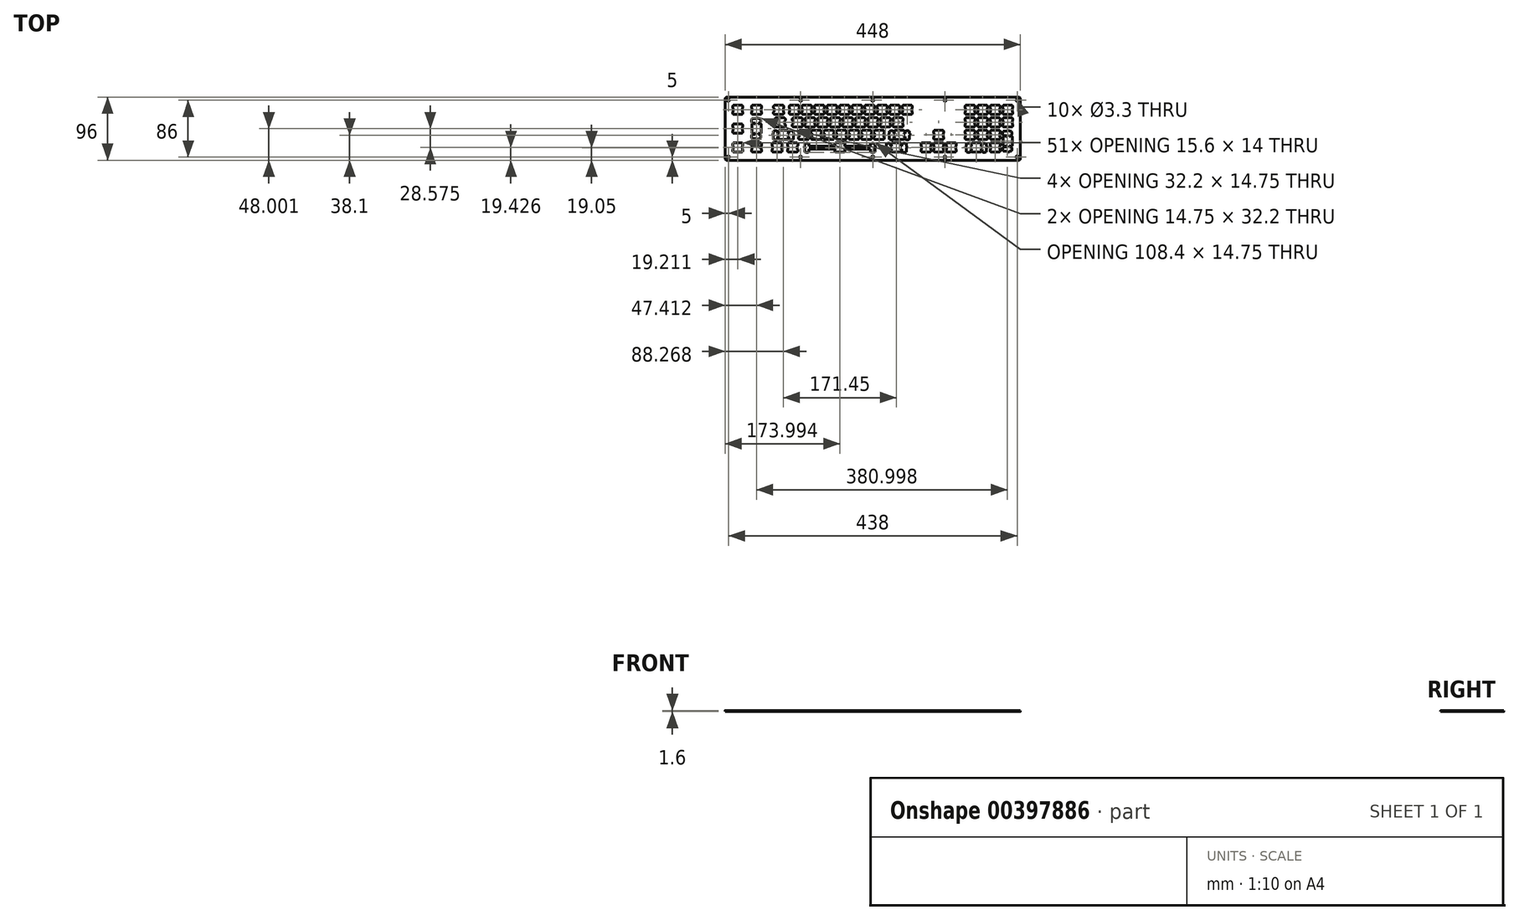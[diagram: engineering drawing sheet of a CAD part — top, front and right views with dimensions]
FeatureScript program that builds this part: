
annotation { "Feature Type Name" : "Feature", "Feature Type Description" : "" }
export const myFeature = defineFeature(function(context is Context, id is Id, definition is map)
    precondition{}
    {
        {
            var Q0;
            Q0=qCreatedBy(makeId("Top.planeOp"),FACE);
            var sketch = newSketch(context, id + "F0", { "sketchPlane" : qUnion([Q0])});
            skLineSegment(sketch, "E0", {"start": v(-224.31, 48.1) * mm, "end": v(224.31, 48.1) * mm});
            skLineSegment(sketch, "E1", {"start": v(224.31, 48.1) * mm, "end": v(224.31, -48.1) * mm});
            skLineSegment(sketch, "E2", {"start": v(224.31, -48.1) * mm, "end": v(-224.31, -48.1) * mm});
            skLineSegment(sketch, "E3", {"start": v(-224.31, -48.1) * mm, "end": v(-224.31, 48.1) * mm});
            skLineSegment(sketch, "E4", {"start": v(-57, -21.57) * mm, "end": v(-57, -22.58) * mm});
            skLineSegment(sketch, "E5", {"start": v(-57, -22.58) * mm, "end": v(-57.8, -22.58) * mm});
            skLineSegment(sketch, "E6", {"start": v(-57.8, -22.58) * mm, "end": v(-57.8, -25.67) * mm});
            skLineSegment(sketch, "E7", {"start": v(-57.8, -25.67) * mm, "end": v(-57, -25.67) * mm});
            skLineSegment(sketch, "E8", {"start": v(-57, -25.67) * mm, "end": v(-57, -26.28) * mm});
            skLineSegment(sketch, "E9", {"start": v(-57, -26.28) * mm, "end": v(-96.68, -26.28) * mm});
            skLineSegment(sketch, "E10", {"start": v(-96.68, -26.28) * mm, "end": v(-96.68, -23.05) * mm});
            skLineSegment(sketch, "E11", {"start": v(-96.68, -23.05) * mm, "end": v(-98.36, -23.05) * mm});
            skLineSegment(sketch, "E12", {"start": v(-98.36, -23.05) * mm, "end": v(-98.36, -22.12) * mm});
            skLineSegment(sketch, "E13", {"start": v(-98.36, -22.12) * mm, "end": v(-101.66, -22.12) * mm});
            skLineSegment(sketch, "E14", {"start": v(-101.66, -22.12) * mm, "end": v(-101.66, -23.05) * mm});
            skLineSegment(sketch, "E15", {"start": v(-101.66, -23.05) * mm, "end": v(-103.33, -23.05) * mm});
            skLineSegment(sketch, "E16", {"start": v(-103.33, -23.05) * mm, "end": v(-103.33, -26.28) * mm});
            skLineSegment(sketch, "E17", {"start": v(-103.33, -26.28) * mm, "end": v(-104.2, -26.28) * mm});
            skLineSegment(sketch, "E18", {"start": v(-104.2, -26.28) * mm, "end": v(-104.2, -29.08) * mm});
            skLineSegment(sketch, "E19", {"start": v(-104.2, -29.08) * mm, "end": v(-103.33, -29.08) * mm});
            skLineSegment(sketch, "E20", {"start": v(-103.33, -29.08) * mm, "end": v(-103.33, -35.35) * mm});
            skLineSegment(sketch, "E21", {"start": v(-103.33, -35.35) * mm, "end": v(-101.66, -35.35) * mm});
            skLineSegment(sketch, "E22", {"start": v(-101.66, -35.35) * mm, "end": v(-101.66, -36.33) * mm});
            skLineSegment(sketch, "E23", {"start": v(-101.66, -36.33) * mm, "end": v(-98.36, -36.33) * mm});
            skLineSegment(sketch, "E24", {"start": v(-98.36, -36.33) * mm, "end": v(-98.36, -35.35) * mm});
            skLineSegment(sketch, "E25", {"start": v(-98.36, -35.35) * mm, "end": v(-96.68, -35.35) * mm});
            skLineSegment(sketch, "E26", {"start": v(-96.68, -35.35) * mm, "end": v(-96.68, -30.88) * mm});
            skLineSegment(sketch, "E27", {"start": v(-96.68, -30.88) * mm, "end": v(-57, -30.88) * mm});
            skLineSegment(sketch, "E28", {"start": v(-57, -30.88) * mm, "end": v(-57, -31.47) * mm});
            skLineSegment(sketch, "E29", {"start": v(-57, -31.47) * mm, "end": v(-57.8, -31.47) * mm});
            skLineSegment(sketch, "E30", {"start": v(-57.8, -31.47) * mm, "end": v(-57.8, -34.58) * mm});
            skLineSegment(sketch, "E31", {"start": v(-57.8, -34.58) * mm, "end": v(-57, -34.58) * mm});
            skLineSegment(sketch, "E32", {"start": v(-57, -34.58) * mm, "end": v(-57, -35.57) * mm});
            skLineSegment(sketch, "E33", {"start": v(-57, -35.57) * mm, "end": v(-43, -35.57) * mm});
            skLineSegment(sketch, "E34", {"start": v(-43, -35.57) * mm, "end": v(-43, -34.58) * mm});
            skLineSegment(sketch, "E35", {"start": v(-43, -34.58) * mm, "end": v(-42.2, -34.58) * mm});
            skLineSegment(sketch, "E36", {"start": v(-42.2, -34.58) * mm, "end": v(-42.2, -31.47) * mm});
            skLineSegment(sketch, "E37", {"start": v(-42.2, -31.47) * mm, "end": v(-43, -31.47) * mm});
            skLineSegment(sketch, "E38", {"start": v(-43, -31.47) * mm, "end": v(-43, -30.88) * mm});
            skLineSegment(sketch, "E39", {"start": v(-43, -30.88) * mm, "end": v(-3.33, -30.88) * mm});
            skLineSegment(sketch, "E40", {"start": v(-3.33, -30.88) * mm, "end": v(-3.33, -35.35) * mm});
            skLineSegment(sketch, "E41", {"start": v(-3.33, -35.35) * mm, "end": v(-1.66, -35.35) * mm});
            skLineSegment(sketch, "E42", {"start": v(-1.66, -35.35) * mm, "end": v(-1.66, -36.33) * mm});
            skLineSegment(sketch, "E43", {"start": v(-1.66, -36.33) * mm, "end": v(1.64, -36.33) * mm});
            skLineSegment(sketch, "E44", {"start": v(1.64, -36.33) * mm, "end": v(1.64, -35.35) * mm});
            skLineSegment(sketch, "E45", {"start": v(1.64, -35.35) * mm, "end": v(3.32, -35.35) * mm});
            skLineSegment(sketch, "E46", {"start": v(3.32, -35.35) * mm, "end": v(3.32, -29.08) * mm});
            skLineSegment(sketch, "E47", {"start": v(3.32, -29.08) * mm, "end": v(4.2, -29.08) * mm});
            skLineSegment(sketch, "E48", {"start": v(4.2, -29.08) * mm, "end": v(4.2, -26.28) * mm});
            skLineSegment(sketch, "E49", {"start": v(4.2, -26.28) * mm, "end": v(3.32, -26.28) * mm});
            skLineSegment(sketch, "E50", {"start": v(3.32, -26.28) * mm, "end": v(3.32, -23.05) * mm});
            skLineSegment(sketch, "E51", {"start": v(3.32, -23.05) * mm, "end": v(1.64, -23.05) * mm});
            skLineSegment(sketch, "E52", {"start": v(1.64, -23.05) * mm, "end": v(1.64, -22.12) * mm});
            skLineSegment(sketch, "E53", {"start": v(1.64, -22.12) * mm, "end": v(-1.66, -22.12) * mm});
            skLineSegment(sketch, "E54", {"start": v(-1.66, -22.12) * mm, "end": v(-1.66, -23.05) * mm});
            skLineSegment(sketch, "E55", {"start": v(-1.66, -23.05) * mm, "end": v(-3.33, -23.05) * mm});
            skLineSegment(sketch, "E56", {"start": v(-3.33, -23.05) * mm, "end": v(-3.33, -26.28) * mm});
            skLineSegment(sketch, "E57", {"start": v(-3.33, -26.28) * mm, "end": v(-43, -26.28) * mm});
            skLineSegment(sketch, "E58", {"start": v(-43, -26.28) * mm, "end": v(-43, -25.67) * mm});
            skLineSegment(sketch, "E59", {"start": v(-43, -25.67) * mm, "end": v(-42.2, -25.67) * mm});
            skLineSegment(sketch, "E60", {"start": v(-42.2, -25.67) * mm, "end": v(-42.2, -22.58) * mm});
            skLineSegment(sketch, "E61", {"start": v(-42.2, -22.58) * mm, "end": v(-43, -22.58) * mm});
            skLineSegment(sketch, "E62", {"start": v(-43, -22.58) * mm, "end": v(-43, -21.57) * mm});
            skLineSegment(sketch, "E63", {"start": v(-43, -21.57) * mm, "end": v(-57, -21.57) * mm});
            skLineSegment(sketch, "E64", {"start": v(28.72, -21.57) * mm, "end": v(28.72, -22.58) * mm});
            skLineSegment(sketch, "E65", {"start": v(28.72, -22.58) * mm, "end": v(27.92, -22.58) * mm});
            skLineSegment(sketch, "E66", {"start": v(27.92, -22.58) * mm, "end": v(27.92, -25.67) * mm});
            skLineSegment(sketch, "E67", {"start": v(27.92, -25.67) * mm, "end": v(28.72, -25.67) * mm});
            skLineSegment(sketch, "E68", {"start": v(28.72, -25.67) * mm, "end": v(28.72, -26.28) * mm});
            skLineSegment(sketch, "E69", {"start": v(28.72, -26.28) * mm, "end": v(27.14, -26.28) * mm});
            skLineSegment(sketch, "E70", {"start": v(27.14, -26.28) * mm, "end": v(27.14, -23.05) * mm});
            skLineSegment(sketch, "E71", {"start": v(27.14, -23.05) * mm, "end": v(25.47, -23.05) * mm});
            skLineSegment(sketch, "E72", {"start": v(25.47, -23.05) * mm, "end": v(25.47, -22.12) * mm});
            skLineSegment(sketch, "E73", {"start": v(25.47, -22.12) * mm, "end": v(22.17, -22.12) * mm});
            skLineSegment(sketch, "E74", {"start": v(22.17, -22.12) * mm, "end": v(22.17, -23.05) * mm});
            skLineSegment(sketch, "E75", {"start": v(22.17, -23.05) * mm, "end": v(20.5, -23.05) * mm});
            skLineSegment(sketch, "E76", {"start": v(20.5, -23.05) * mm, "end": v(20.5, -26.28) * mm});
            skLineSegment(sketch, "E77", {"start": v(20.5, -26.28) * mm, "end": v(19.62, -26.28) * mm});
            skLineSegment(sketch, "E78", {"start": v(19.62, -26.28) * mm, "end": v(19.62, -29.08) * mm});
            skLineSegment(sketch, "E79", {"start": v(19.62, -29.08) * mm, "end": v(20.5, -29.08) * mm});
            skLineSegment(sketch, "E80", {"start": v(20.5, -29.08) * mm, "end": v(20.5, -35.35) * mm});
            skLineSegment(sketch, "E81", {"start": v(20.5, -35.35) * mm, "end": v(22.17, -35.35) * mm});
            skLineSegment(sketch, "E82", {"start": v(22.17, -35.35) * mm, "end": v(22.17, -36.33) * mm});
            skLineSegment(sketch, "E83", {"start": v(22.17, -36.33) * mm, "end": v(25.47, -36.33) * mm});
            skLineSegment(sketch, "E84", {"start": v(25.47, -36.33) * mm, "end": v(25.47, -35.35) * mm});
            skLineSegment(sketch, "E85", {"start": v(25.47, -35.35) * mm, "end": v(27.14, -35.35) * mm});
            skLineSegment(sketch, "E86", {"start": v(27.14, -35.35) * mm, "end": v(27.14, -30.88) * mm});
            skLineSegment(sketch, "E87", {"start": v(27.14, -30.88) * mm, "end": v(28.72, -30.88) * mm});
            skLineSegment(sketch, "E88", {"start": v(28.72, -30.88) * mm, "end": v(28.72, -31.47) * mm});
            skLineSegment(sketch, "E89", {"start": v(28.72, -31.47) * mm, "end": v(27.92, -31.47) * mm});
            skLineSegment(sketch, "E90", {"start": v(27.92, -31.47) * mm, "end": v(27.92, -34.58) * mm});
            skLineSegment(sketch, "E91", {"start": v(27.92, -34.58) * mm, "end": v(28.72, -34.58) * mm});
            skLineSegment(sketch, "E92", {"start": v(28.72, -34.58) * mm, "end": v(28.72, -35.57) * mm});
            skLineSegment(sketch, "E93", {"start": v(28.72, -35.57) * mm, "end": v(42.72, -35.57) * mm});
            skLineSegment(sketch, "E94", {"start": v(42.72, -35.57) * mm, "end": v(42.72, -34.58) * mm});
            skLineSegment(sketch, "E95", {"start": v(42.72, -34.58) * mm, "end": v(43.52, -34.58) * mm});
            skLineSegment(sketch, "E96", {"start": v(43.52, -34.58) * mm, "end": v(43.52, -31.47) * mm});
            skLineSegment(sketch, "E97", {"start": v(43.52, -31.47) * mm, "end": v(42.72, -31.47) * mm});
            skLineSegment(sketch, "E98", {"start": v(42.72, -31.47) * mm, "end": v(42.72, -30.88) * mm});
            skLineSegment(sketch, "E99", {"start": v(42.72, -30.88) * mm, "end": v(44.3, -30.88) * mm});
            skLineSegment(sketch, "E100", {"start": v(44.3, -30.88) * mm, "end": v(44.3, -35.35) * mm});
            skLineSegment(sketch, "E101", {"start": v(44.3, -35.35) * mm, "end": v(45.97, -35.35) * mm});
            skLineSegment(sketch, "E102", {"start": v(45.97, -35.35) * mm, "end": v(45.97, -36.33) * mm});
            skLineSegment(sketch, "E103", {"start": v(45.97, -36.33) * mm, "end": v(49.27, -36.33) * mm});
            skLineSegment(sketch, "E104", {"start": v(49.27, -36.33) * mm, "end": v(49.27, -35.35) * mm});
            skLineSegment(sketch, "E105", {"start": v(49.27, -35.35) * mm, "end": v(50.94, -35.35) * mm});
            skLineSegment(sketch, "E106", {"start": v(50.94, -35.35) * mm, "end": v(50.94, -29.08) * mm});
            skLineSegment(sketch, "E107", {"start": v(50.94, -29.08) * mm, "end": v(51.82, -29.08) * mm});
            skLineSegment(sketch, "E108", {"start": v(51.82, -29.08) * mm, "end": v(51.82, -26.28) * mm});
            skLineSegment(sketch, "E109", {"start": v(51.82, -26.28) * mm, "end": v(50.94, -26.28) * mm});
            skLineSegment(sketch, "E110", {"start": v(50.94, -26.28) * mm, "end": v(50.94, -23.05) * mm});
            skLineSegment(sketch, "E111", {"start": v(50.94, -23.05) * mm, "end": v(49.27, -23.05) * mm});
            skLineSegment(sketch, "E112", {"start": v(49.27, -23.05) * mm, "end": v(49.27, -22.12) * mm});
            skLineSegment(sketch, "E113", {"start": v(49.27, -22.12) * mm, "end": v(45.97, -22.12) * mm});
            skLineSegment(sketch, "E114", {"start": v(45.97, -22.12) * mm, "end": v(45.97, -23.05) * mm});
            skLineSegment(sketch, "E115", {"start": v(45.97, -23.05) * mm, "end": v(44.3, -23.05) * mm});
            skLineSegment(sketch, "E116", {"start": v(44.3, -23.05) * mm, "end": v(44.3, -26.28) * mm});
            skLineSegment(sketch, "E117", {"start": v(44.3, -26.28) * mm, "end": v(42.72, -26.28) * mm});
            skLineSegment(sketch, "E118", {"start": v(42.72, -26.28) * mm, "end": v(42.72, -25.67) * mm});
            skLineSegment(sketch, "E119", {"start": v(42.72, -25.67) * mm, "end": v(43.52, -25.67) * mm});
            skLineSegment(sketch, "E120", {"start": v(43.52, -25.67) * mm, "end": v(43.52, -22.58) * mm});
            skLineSegment(sketch, "E121", {"start": v(43.52, -22.58) * mm, "end": v(42.72, -22.58) * mm});
            skLineSegment(sketch, "E122", {"start": v(42.72, -22.58) * mm, "end": v(42.72, -21.57) * mm});
            skLineSegment(sketch, "E123", {"start": v(42.72, -21.57) * mm, "end": v(28.72, -21.57) * mm});
            skLineSegment(sketch, "E124", {"start": v(150.16, -21.57) * mm, "end": v(150.16, -22.58) * mm});
            skLineSegment(sketch, "E125", {"start": v(150.16, -22.58) * mm, "end": v(149.36, -22.58) * mm});
            skLineSegment(sketch, "E126", {"start": v(149.36, -22.58) * mm, "end": v(149.36, -25.67) * mm});
            skLineSegment(sketch, "E127", {"start": v(149.36, -25.67) * mm, "end": v(150.16, -25.67) * mm});
            skLineSegment(sketch, "E128", {"start": v(150.16, -25.67) * mm, "end": v(150.16, -26.28) * mm});
            skLineSegment(sketch, "E129", {"start": v(150.16, -26.28) * mm, "end": v(148.59, -26.28) * mm});
            skLineSegment(sketch, "E130", {"start": v(148.59, -26.28) * mm, "end": v(148.59, -23.05) * mm});
            skLineSegment(sketch, "E131", {"start": v(148.59, -23.05) * mm, "end": v(146.91, -23.05) * mm});
            skLineSegment(sketch, "E132", {"start": v(146.91, -23.05) * mm, "end": v(146.91, -22.12) * mm});
            skLineSegment(sketch, "E133", {"start": v(146.91, -22.12) * mm, "end": v(143.61, -22.12) * mm});
            skLineSegment(sketch, "E134", {"start": v(143.61, -22.12) * mm, "end": v(143.61, -23.05) * mm});
            skLineSegment(sketch, "E135", {"start": v(143.61, -23.05) * mm, "end": v(141.94, -23.05) * mm});
            skLineSegment(sketch, "E136", {"start": v(141.94, -23.05) * mm, "end": v(141.94, -26.28) * mm});
            skLineSegment(sketch, "E137", {"start": v(141.94, -26.28) * mm, "end": v(141.06, -26.28) * mm});
            skLineSegment(sketch, "E138", {"start": v(141.06, -26.28) * mm, "end": v(141.06, -29.08) * mm});
            skLineSegment(sketch, "E139", {"start": v(141.06, -29.08) * mm, "end": v(141.94, -29.08) * mm});
            skLineSegment(sketch, "E140", {"start": v(141.94, -29.08) * mm, "end": v(141.94, -35.35) * mm});
            skLineSegment(sketch, "E141", {"start": v(141.94, -35.35) * mm, "end": v(143.61, -35.35) * mm});
            skLineSegment(sketch, "E142", {"start": v(143.61, -35.35) * mm, "end": v(143.61, -36.33) * mm});
            skLineSegment(sketch, "E143", {"start": v(143.61, -36.33) * mm, "end": v(146.91, -36.33) * mm});
            skLineSegment(sketch, "E144", {"start": v(146.91, -36.33) * mm, "end": v(146.91, -35.35) * mm});
            skLineSegment(sketch, "E145", {"start": v(146.91, -35.35) * mm, "end": v(148.59, -35.35) * mm});
            skLineSegment(sketch, "E146", {"start": v(148.59, -35.35) * mm, "end": v(148.59, -30.88) * mm});
            skLineSegment(sketch, "E147", {"start": v(148.59, -30.88) * mm, "end": v(150.16, -30.88) * mm});
            skLineSegment(sketch, "E148", {"start": v(150.16, -30.88) * mm, "end": v(150.16, -31.47) * mm});
            skLineSegment(sketch, "E149", {"start": v(150.16, -31.47) * mm, "end": v(149.36, -31.47) * mm});
            skLineSegment(sketch, "E150", {"start": v(149.36, -31.47) * mm, "end": v(149.36, -34.58) * mm});
            skLineSegment(sketch, "E151", {"start": v(149.36, -34.58) * mm, "end": v(150.16, -34.58) * mm});
            skLineSegment(sketch, "E152", {"start": v(150.16, -34.58) * mm, "end": v(150.16, -35.57) * mm});
            skLineSegment(sketch, "E153", {"start": v(150.16, -35.57) * mm, "end": v(164.16, -35.57) * mm});
            skLineSegment(sketch, "E154", {"start": v(164.16, -35.57) * mm, "end": v(164.16, -34.58) * mm});
            skLineSegment(sketch, "E155", {"start": v(164.16, -34.58) * mm, "end": v(164.96, -34.58) * mm});
            skLineSegment(sketch, "E156", {"start": v(164.96, -34.58) * mm, "end": v(164.96, -31.47) * mm});
            skLineSegment(sketch, "E157", {"start": v(164.96, -31.47) * mm, "end": v(164.16, -31.47) * mm});
            skLineSegment(sketch, "E158", {"start": v(164.16, -31.47) * mm, "end": v(164.16, -30.88) * mm});
            skLineSegment(sketch, "E159", {"start": v(164.16, -30.88) * mm, "end": v(165.74, -30.88) * mm});
            skLineSegment(sketch, "E160", {"start": v(165.74, -30.88) * mm, "end": v(165.74, -35.35) * mm});
            skLineSegment(sketch, "E161", {"start": v(165.74, -35.35) * mm, "end": v(167.41, -35.35) * mm});
            skLineSegment(sketch, "E162", {"start": v(167.41, -35.35) * mm, "end": v(167.41, -36.33) * mm});
            skLineSegment(sketch, "E163", {"start": v(167.41, -36.33) * mm, "end": v(170.71, -36.33) * mm});
            skLineSegment(sketch, "E164", {"start": v(170.71, -36.33) * mm, "end": v(170.71, -35.35) * mm});
            skLineSegment(sketch, "E165", {"start": v(170.71, -35.35) * mm, "end": v(172.39, -35.35) * mm});
            skLineSegment(sketch, "E166", {"start": v(172.39, -35.35) * mm, "end": v(172.39, -29.08) * mm});
            skLineSegment(sketch, "E167", {"start": v(172.39, -29.08) * mm, "end": v(173.26, -29.08) * mm});
            skLineSegment(sketch, "E168", {"start": v(173.26, -29.08) * mm, "end": v(173.26, -26.28) * mm});
            skLineSegment(sketch, "E169", {"start": v(173.26, -26.28) * mm, "end": v(172.39, -26.28) * mm});
            skLineSegment(sketch, "E170", {"start": v(172.39, -26.28) * mm, "end": v(172.39, -23.05) * mm});
            skLineSegment(sketch, "E171", {"start": v(172.39, -23.05) * mm, "end": v(170.71, -23.05) * mm});
            skLineSegment(sketch, "E172", {"start": v(170.71, -23.05) * mm, "end": v(170.71, -22.12) * mm});
            skLineSegment(sketch, "E173", {"start": v(170.71, -22.12) * mm, "end": v(167.41, -22.12) * mm});
            skLineSegment(sketch, "E174", {"start": v(167.41, -22.12) * mm, "end": v(167.41, -23.05) * mm});
            skLineSegment(sketch, "E175", {"start": v(167.41, -23.05) * mm, "end": v(165.74, -23.05) * mm});
            skLineSegment(sketch, "E176", {"start": v(165.74, -23.05) * mm, "end": v(165.74, -26.28) * mm});
            skLineSegment(sketch, "E177", {"start": v(165.74, -26.28) * mm, "end": v(164.16, -26.28) * mm});
            skLineSegment(sketch, "E178", {"start": v(164.16, -26.28) * mm, "end": v(164.16, -25.67) * mm});
            skLineSegment(sketch, "E179", {"start": v(164.16, -25.67) * mm, "end": v(164.96, -25.67) * mm});
            skLineSegment(sketch, "E180", {"start": v(164.96, -25.67) * mm, "end": v(164.96, -22.58) * mm});
            skLineSegment(sketch, "E181", {"start": v(164.96, -22.58) * mm, "end": v(164.16, -22.58) * mm});
            skLineSegment(sketch, "E182", {"start": v(164.16, -22.58) * mm, "end": v(164.16, -21.57) * mm});
            skLineSegment(sketch, "E183", {"start": v(164.16, -21.57) * mm, "end": v(150.16, -21.57) * mm});
            skLineSegment(sketch, "E184", {"start": v(-211.79, -21.57) * mm, "end": v(-211.79, -22.58) * mm});
            skLineSegment(sketch, "E185", {"start": v(-211.79, -22.58) * mm, "end": v(-212.59, -22.58) * mm});
            skLineSegment(sketch, "E186", {"start": v(-212.59, -22.58) * mm, "end": v(-212.59, -25.67) * mm});
            skLineSegment(sketch, "E187", {"start": v(-212.59, -25.67) * mm, "end": v(-211.79, -25.67) * mm});
            skLineSegment(sketch, "E188", {"start": v(-211.79, -25.67) * mm, "end": v(-211.79, -31.47) * mm});
            skLineSegment(sketch, "E189", {"start": v(-211.79, -31.47) * mm, "end": v(-212.59, -31.47) * mm});
            skLineSegment(sketch, "E190", {"start": v(-212.59, -31.47) * mm, "end": v(-212.59, -34.58) * mm});
            skLineSegment(sketch, "E191", {"start": v(-212.59, -34.58) * mm, "end": v(-211.79, -34.58) * mm});
            skLineSegment(sketch, "E192", {"start": v(-211.79, -34.58) * mm, "end": v(-211.79, -35.57) * mm});
            skLineSegment(sketch, "E193", {"start": v(-211.79, -35.57) * mm, "end": v(-197.79, -35.57) * mm});
            skLineSegment(sketch, "E194", {"start": v(-197.79, -35.57) * mm, "end": v(-197.79, -34.58) * mm});
            skLineSegment(sketch, "E195", {"start": v(-197.79, -34.58) * mm, "end": v(-197, -34.58) * mm});
            skLineSegment(sketch, "E196", {"start": v(-197, -34.58) * mm, "end": v(-197, -31.47) * mm});
            skLineSegment(sketch, "E197", {"start": v(-197, -31.47) * mm, "end": v(-197.79, -31.47) * mm});
            skLineSegment(sketch, "E198", {"start": v(-197.79, -31.47) * mm, "end": v(-197.79, -25.67) * mm});
            skLineSegment(sketch, "E199", {"start": v(-197.79, -25.67) * mm, "end": v(-197, -25.67) * mm});
            skLineSegment(sketch, "E200", {"start": v(-197, -25.67) * mm, "end": v(-197, -22.58) * mm});
            skLineSegment(sketch, "E201", {"start": v(-197, -22.58) * mm, "end": v(-197.79, -22.58) * mm});
            skLineSegment(sketch, "E202", {"start": v(-197.79, -22.58) * mm, "end": v(-197.79, -21.57) * mm});
            skLineSegment(sketch, "E203", {"start": v(-197.79, -21.57) * mm, "end": v(-211.79, -21.57) * mm});
            skLineSegment(sketch, "E204", {"start": v(-183.21, -21.57) * mm, "end": v(-183.21, -22.58) * mm});
            skLineSegment(sketch, "E205", {"start": v(-183.21, -22.58) * mm, "end": v(-184.01, -22.58) * mm});
            skLineSegment(sketch, "E206", {"start": v(-184.01, -22.58) * mm, "end": v(-184.01, -25.67) * mm});
            skLineSegment(sketch, "E207", {"start": v(-184.01, -25.67) * mm, "end": v(-183.21, -25.67) * mm});
            skLineSegment(sketch, "E208", {"start": v(-183.21, -25.67) * mm, "end": v(-183.21, -31.47) * mm});
            skLineSegment(sketch, "E209", {"start": v(-183.21, -31.47) * mm, "end": v(-184.01, -31.47) * mm});
            skLineSegment(sketch, "E210", {"start": v(-184.01, -31.47) * mm, "end": v(-184.01, -34.58) * mm});
            skLineSegment(sketch, "E211", {"start": v(-184.01, -34.58) * mm, "end": v(-183.21, -34.58) * mm});
            skLineSegment(sketch, "E212", {"start": v(-183.21, -34.58) * mm, "end": v(-183.21, -35.57) * mm});
            skLineSegment(sketch, "E213", {"start": v(-183.21, -35.57) * mm, "end": v(-169.21, -35.57) * mm});
            skLineSegment(sketch, "E214", {"start": v(-169.21, -35.57) * mm, "end": v(-169.21, -34.58) * mm});
            skLineSegment(sketch, "E215", {"start": v(-169.21, -34.58) * mm, "end": v(-168.41, -34.58) * mm});
            skLineSegment(sketch, "E216", {"start": v(-168.41, -34.58) * mm, "end": v(-168.41, -31.47) * mm});
            skLineSegment(sketch, "E217", {"start": v(-168.41, -31.47) * mm, "end": v(-169.21, -31.47) * mm});
            skLineSegment(sketch, "E218", {"start": v(-169.21, -31.47) * mm, "end": v(-169.21, -25.67) * mm});
            skLineSegment(sketch, "E219", {"start": v(-169.21, -25.67) * mm, "end": v(-168.41, -25.67) * mm});
            skLineSegment(sketch, "E220", {"start": v(-168.41, -25.67) * mm, "end": v(-168.41, -22.58) * mm});
            skLineSegment(sketch, "E221", {"start": v(-168.41, -22.58) * mm, "end": v(-169.21, -22.58) * mm});
            skLineSegment(sketch, "E222", {"start": v(-169.21, -22.58) * mm, "end": v(-169.21, -21.57) * mm});
            skLineSegment(sketch, "E223", {"start": v(-169.21, -21.57) * mm, "end": v(-183.21, -21.57) * mm});
            skLineSegment(sketch, "E224", {"start": v(-152.26, -21.57) * mm, "end": v(-152.26, -22.58) * mm});
            skLineSegment(sketch, "E225", {"start": v(-152.26, -22.58) * mm, "end": v(-153.06, -22.58) * mm});
            skLineSegment(sketch, "E226", {"start": v(-153.06, -22.58) * mm, "end": v(-153.06, -25.67) * mm});
            skLineSegment(sketch, "E227", {"start": v(-153.06, -25.67) * mm, "end": v(-152.26, -25.67) * mm});
            skLineSegment(sketch, "E228", {"start": v(-152.26, -25.67) * mm, "end": v(-152.26, -31.47) * mm});
            skLineSegment(sketch, "E229", {"start": v(-152.26, -31.47) * mm, "end": v(-153.06, -31.47) * mm});
            skLineSegment(sketch, "E230", {"start": v(-153.06, -31.47) * mm, "end": v(-153.06, -34.58) * mm});
            skLineSegment(sketch, "E231", {"start": v(-153.06, -34.58) * mm, "end": v(-152.26, -34.58) * mm});
            skLineSegment(sketch, "E232", {"start": v(-152.26, -34.58) * mm, "end": v(-152.26, -35.57) * mm});
            skLineSegment(sketch, "E233", {"start": v(-152.26, -35.57) * mm, "end": v(-138.26, -35.57) * mm});
            skLineSegment(sketch, "E234", {"start": v(-138.26, -35.57) * mm, "end": v(-138.26, -34.58) * mm});
            skLineSegment(sketch, "E235", {"start": v(-138.26, -34.58) * mm, "end": v(-137.46, -34.58) * mm});
            skLineSegment(sketch, "E236", {"start": v(-137.46, -34.58) * mm, "end": v(-137.46, -31.47) * mm});
            skLineSegment(sketch, "E237", {"start": v(-137.46, -31.47) * mm, "end": v(-138.26, -31.47) * mm});
            skLineSegment(sketch, "E238", {"start": v(-138.26, -31.47) * mm, "end": v(-138.26, -25.67) * mm});
            skLineSegment(sketch, "E239", {"start": v(-138.26, -25.67) * mm, "end": v(-137.46, -25.67) * mm});
            skLineSegment(sketch, "E240", {"start": v(-137.46, -25.67) * mm, "end": v(-137.46, -22.58) * mm});
            skLineSegment(sketch, "E241", {"start": v(-137.46, -22.58) * mm, "end": v(-138.26, -22.58) * mm});
            skLineSegment(sketch, "E242", {"start": v(-138.26, -22.58) * mm, "end": v(-138.26, -21.57) * mm});
            skLineSegment(sketch, "E243", {"start": v(-138.26, -21.57) * mm, "end": v(-152.26, -21.57) * mm});
            skLineSegment(sketch, "E244", {"start": v(-128.45, -21.57) * mm, "end": v(-128.45, -22.58) * mm});
            skLineSegment(sketch, "E245", {"start": v(-128.45, -22.58) * mm, "end": v(-129.24, -22.58) * mm});
            skLineSegment(sketch, "E246", {"start": v(-129.24, -22.58) * mm, "end": v(-129.24, -25.67) * mm});
            skLineSegment(sketch, "E247", {"start": v(-129.24, -25.67) * mm, "end": v(-128.45, -25.67) * mm});
            skLineSegment(sketch, "E248", {"start": v(-128.45, -25.67) * mm, "end": v(-128.45, -31.47) * mm});
            skLineSegment(sketch, "E249", {"start": v(-128.45, -31.47) * mm, "end": v(-129.24, -31.47) * mm});
            skLineSegment(sketch, "E250", {"start": v(-129.24, -31.47) * mm, "end": v(-129.24, -34.58) * mm});
            skLineSegment(sketch, "E251", {"start": v(-129.24, -34.58) * mm, "end": v(-128.45, -34.58) * mm});
            skLineSegment(sketch, "E252", {"start": v(-128.45, -34.58) * mm, "end": v(-128.45, -35.57) * mm});
            skLineSegment(sketch, "E253", {"start": v(-128.45, -35.57) * mm, "end": v(-114.44, -35.57) * mm});
            skLineSegment(sketch, "E254", {"start": v(-114.44, -35.57) * mm, "end": v(-114.44, -34.58) * mm});
            skLineSegment(sketch, "E255", {"start": v(-114.44, -34.58) * mm, "end": v(-113.65, -34.58) * mm});
            skLineSegment(sketch, "E256", {"start": v(-113.65, -34.58) * mm, "end": v(-113.65, -31.47) * mm});
            skLineSegment(sketch, "E257", {"start": v(-113.65, -31.47) * mm, "end": v(-114.44, -31.47) * mm});
            skLineSegment(sketch, "E258", {"start": v(-114.44, -31.47) * mm, "end": v(-114.44, -25.67) * mm});
            skLineSegment(sketch, "E259", {"start": v(-114.44, -25.67) * mm, "end": v(-113.65, -25.67) * mm});
            skLineSegment(sketch, "E260", {"start": v(-113.65, -25.67) * mm, "end": v(-113.65, -22.58) * mm});
            skLineSegment(sketch, "E261", {"start": v(-113.65, -22.58) * mm, "end": v(-114.44, -22.58) * mm});
            skLineSegment(sketch, "E262", {"start": v(-114.44, -22.58) * mm, "end": v(-114.44, -21.57) * mm});
            skLineSegment(sketch, "E263", {"start": v(-114.44, -21.57) * mm, "end": v(-128.45, -21.57) * mm});
            skLineSegment(sketch, "E264", {"start": v(73.96, -21.57) * mm, "end": v(73.96, -22.58) * mm});
            skLineSegment(sketch, "E265", {"start": v(73.96, -22.58) * mm, "end": v(73.16, -22.58) * mm});
            skLineSegment(sketch, "E266", {"start": v(73.16, -22.58) * mm, "end": v(73.16, -25.67) * mm});
            skLineSegment(sketch, "E267", {"start": v(73.16, -25.67) * mm, "end": v(73.96, -25.67) * mm});
            skLineSegment(sketch, "E268", {"start": v(73.96, -25.67) * mm, "end": v(73.96, -31.47) * mm});
            skLineSegment(sketch, "E269", {"start": v(73.96, -31.47) * mm, "end": v(73.16, -31.47) * mm});
            skLineSegment(sketch, "E270", {"start": v(73.16, -31.47) * mm, "end": v(73.16, -34.58) * mm});
            skLineSegment(sketch, "E271", {"start": v(73.16, -34.58) * mm, "end": v(73.96, -34.58) * mm});
            skLineSegment(sketch, "E272", {"start": v(73.96, -34.58) * mm, "end": v(73.96, -35.57) * mm});
            skLineSegment(sketch, "E273", {"start": v(73.96, -35.57) * mm, "end": v(87.96, -35.57) * mm});
            skLineSegment(sketch, "E274", {"start": v(87.96, -35.57) * mm, "end": v(87.96, -34.58) * mm});
            skLineSegment(sketch, "E275", {"start": v(87.96, -34.58) * mm, "end": v(88.76, -34.58) * mm});
            skLineSegment(sketch, "E276", {"start": v(88.76, -34.58) * mm, "end": v(88.76, -31.47) * mm});
            skLineSegment(sketch, "E277", {"start": v(88.76, -31.47) * mm, "end": v(87.96, -31.47) * mm});
            skLineSegment(sketch, "E278", {"start": v(87.96, -31.47) * mm, "end": v(87.96, -25.67) * mm});
            skLineSegment(sketch, "E279", {"start": v(87.96, -25.67) * mm, "end": v(88.76, -25.67) * mm});
            skLineSegment(sketch, "E280", {"start": v(88.76, -25.67) * mm, "end": v(88.76, -22.58) * mm});
            skLineSegment(sketch, "E281", {"start": v(88.76, -22.58) * mm, "end": v(87.96, -22.58) * mm});
            skLineSegment(sketch, "E282", {"start": v(87.96, -22.58) * mm, "end": v(87.96, -21.57) * mm});
            skLineSegment(sketch, "E283", {"start": v(87.96, -21.57) * mm, "end": v(73.96, -21.57) * mm});
            skLineSegment(sketch, "E284", {"start": v(93.01, -21.57) * mm, "end": v(93.01, -22.58) * mm});
            skLineSegment(sketch, "E285", {"start": v(93.01, -22.58) * mm, "end": v(92.21, -22.58) * mm});
            skLineSegment(sketch, "E286", {"start": v(92.21, -22.58) * mm, "end": v(92.21, -25.67) * mm});
            skLineSegment(sketch, "E287", {"start": v(92.21, -25.67) * mm, "end": v(93.01, -25.67) * mm});
            skLineSegment(sketch, "E288", {"start": v(93.01, -25.67) * mm, "end": v(93.01, -31.47) * mm});
            skLineSegment(sketch, "E289", {"start": v(93.01, -31.47) * mm, "end": v(92.21, -31.47) * mm});
            skLineSegment(sketch, "E290", {"start": v(92.21, -31.47) * mm, "end": v(92.21, -34.58) * mm});
            skLineSegment(sketch, "E291", {"start": v(92.21, -34.58) * mm, "end": v(93.01, -34.58) * mm});
            skLineSegment(sketch, "E292", {"start": v(93.01, -34.58) * mm, "end": v(93.01, -35.57) * mm});
            skLineSegment(sketch, "E293", {"start": v(93.01, -35.57) * mm, "end": v(107.01, -35.57) * mm});
            skLineSegment(sketch, "E294", {"start": v(107.01, -35.57) * mm, "end": v(107.01, -34.58) * mm});
            skLineSegment(sketch, "E295", {"start": v(107.01, -34.58) * mm, "end": v(107.81, -34.58) * mm});
            skLineSegment(sketch, "E296", {"start": v(107.81, -34.58) * mm, "end": v(107.81, -31.47) * mm});
            skLineSegment(sketch, "E297", {"start": v(107.81, -31.47) * mm, "end": v(107.01, -31.47) * mm});
            skLineSegment(sketch, "E298", {"start": v(107.01, -31.47) * mm, "end": v(107.01, -25.67) * mm});
            skLineSegment(sketch, "E299", {"start": v(107.01, -25.67) * mm, "end": v(107.81, -25.67) * mm});
            skLineSegment(sketch, "E300", {"start": v(107.81, -25.67) * mm, "end": v(107.81, -22.58) * mm});
            skLineSegment(sketch, "E301", {"start": v(107.81, -22.58) * mm, "end": v(107.01, -22.58) * mm});
            skLineSegment(sketch, "E302", {"start": v(107.01, -22.58) * mm, "end": v(107.01, -21.57) * mm});
            skLineSegment(sketch, "E303", {"start": v(107.01, -21.57) * mm, "end": v(93.01, -21.57) * mm});
            skLineSegment(sketch, "E304", {"start": v(112.06, -21.57) * mm, "end": v(112.06, -22.58) * mm});
            skLineSegment(sketch, "E305", {"start": v(112.06, -22.58) * mm, "end": v(111.26, -22.58) * mm});
            skLineSegment(sketch, "E306", {"start": v(111.26, -22.58) * mm, "end": v(111.26, -25.67) * mm});
            skLineSegment(sketch, "E307", {"start": v(111.26, -25.67) * mm, "end": v(112.06, -25.67) * mm});
            skLineSegment(sketch, "E308", {"start": v(112.06, -25.67) * mm, "end": v(112.06, -31.47) * mm});
            skLineSegment(sketch, "E309", {"start": v(112.06, -31.47) * mm, "end": v(111.26, -31.47) * mm});
            skLineSegment(sketch, "E310", {"start": v(111.26, -31.47) * mm, "end": v(111.26, -34.58) * mm});
            skLineSegment(sketch, "E311", {"start": v(111.26, -34.58) * mm, "end": v(112.06, -34.58) * mm});
            skLineSegment(sketch, "E312", {"start": v(112.06, -34.58) * mm, "end": v(112.06, -35.57) * mm});
            skLineSegment(sketch, "E313", {"start": v(112.06, -35.57) * mm, "end": v(126.06, -35.57) * mm});
            skLineSegment(sketch, "E314", {"start": v(126.06, -35.57) * mm, "end": v(126.06, -34.58) * mm});
            skLineSegment(sketch, "E315", {"start": v(126.06, -34.58) * mm, "end": v(126.86, -34.58) * mm});
            skLineSegment(sketch, "E316", {"start": v(126.86, -34.58) * mm, "end": v(126.86, -31.47) * mm});
            skLineSegment(sketch, "E317", {"start": v(126.86, -31.47) * mm, "end": v(126.06, -31.47) * mm});
            skLineSegment(sketch, "E318", {"start": v(126.06, -31.47) * mm, "end": v(126.06, -25.67) * mm});
            skLineSegment(sketch, "E319", {"start": v(126.06, -25.67) * mm, "end": v(126.86, -25.67) * mm});
            skLineSegment(sketch, "E320", {"start": v(126.86, -25.67) * mm, "end": v(126.86, -22.58) * mm});
            skLineSegment(sketch, "E321", {"start": v(126.86, -22.58) * mm, "end": v(126.06, -22.58) * mm});
            skLineSegment(sketch, "E322", {"start": v(126.06, -22.58) * mm, "end": v(126.06, -21.57) * mm});
            skLineSegment(sketch, "E323", {"start": v(126.06, -21.57) * mm, "end": v(112.06, -21.57) * mm});
            skLineSegment(sketch, "E324", {"start": v(178.74, -21.57) * mm, "end": v(178.74, -22.58) * mm});
            skLineSegment(sketch, "E325", {"start": v(178.74, -22.58) * mm, "end": v(177.94, -22.58) * mm});
            skLineSegment(sketch, "E326", {"start": v(177.94, -22.58) * mm, "end": v(177.94, -25.67) * mm});
            skLineSegment(sketch, "E327", {"start": v(177.94, -25.67) * mm, "end": v(178.74, -25.67) * mm});
            skLineSegment(sketch, "E328", {"start": v(178.74, -25.67) * mm, "end": v(178.74, -31.47) * mm});
            skLineSegment(sketch, "E329", {"start": v(178.74, -31.47) * mm, "end": v(177.94, -31.47) * mm});
            skLineSegment(sketch, "E330", {"start": v(177.94, -31.47) * mm, "end": v(177.94, -34.58) * mm});
            skLineSegment(sketch, "E331", {"start": v(177.94, -34.58) * mm, "end": v(178.74, -34.58) * mm});
            skLineSegment(sketch, "E332", {"start": v(178.74, -34.58) * mm, "end": v(178.74, -35.57) * mm});
            skLineSegment(sketch, "E333", {"start": v(178.74, -35.57) * mm, "end": v(192.74, -35.57) * mm});
            skLineSegment(sketch, "E334", {"start": v(192.74, -35.57) * mm, "end": v(192.74, -34.58) * mm});
            skLineSegment(sketch, "E335", {"start": v(192.74, -34.58) * mm, "end": v(193.54, -34.58) * mm});
            skLineSegment(sketch, "E336", {"start": v(193.54, -34.58) * mm, "end": v(193.54, -31.47) * mm});
            skLineSegment(sketch, "E337", {"start": v(193.54, -31.47) * mm, "end": v(192.74, -31.47) * mm});
            skLineSegment(sketch, "E338", {"start": v(192.74, -31.47) * mm, "end": v(192.74, -25.67) * mm});
            skLineSegment(sketch, "E339", {"start": v(192.74, -25.67) * mm, "end": v(193.54, -25.67) * mm});
            skLineSegment(sketch, "E340", {"start": v(193.54, -25.67) * mm, "end": v(193.54, -22.58) * mm});
            skLineSegment(sketch, "E341", {"start": v(193.54, -22.58) * mm, "end": v(192.74, -22.58) * mm});
            skLineSegment(sketch, "E342", {"start": v(192.74, -22.58) * mm, "end": v(192.74, -21.57) * mm});
            skLineSegment(sketch, "E343", {"start": v(192.74, -21.57) * mm, "end": v(178.74, -21.57) * mm});
            skLineSegment(sketch, "E344", {"start": v(204.29, -2.95) * mm, "end": v(204.29, -3.82) * mm});
            skLineSegment(sketch, "E345", {"start": v(204.29, -3.82) * mm, "end": v(198.02, -3.82) * mm});
            skLineSegment(sketch, "E346", {"start": v(198.02, -3.82) * mm, "end": v(198.02, -5.5) * mm});
            skLineSegment(sketch, "E347", {"start": v(198.02, -5.5) * mm, "end": v(197.04, -5.5) * mm});
            skLineSegment(sketch, "E348", {"start": v(197.04, -5.5) * mm, "end": v(197.04, -8.8) * mm});
            skLineSegment(sketch, "E349", {"start": v(197.04, -8.8) * mm, "end": v(198.02, -8.8) * mm});
            skLineSegment(sketch, "E350", {"start": v(198.02, -8.8) * mm, "end": v(198.02, -10.47) * mm});
            skLineSegment(sketch, "E351", {"start": v(198.02, -10.47) * mm, "end": v(202.49, -10.47) * mm});
            skLineSegment(sketch, "E352", {"start": v(202.49, -10.47) * mm, "end": v(202.49, -12.05) * mm});
            skLineSegment(sketch, "E353", {"start": v(202.49, -12.05) * mm, "end": v(201.89, -12.05) * mm});
            skLineSegment(sketch, "E354", {"start": v(201.89, -12.05) * mm, "end": v(201.89, -11.25) * mm});
            skLineSegment(sketch, "E355", {"start": v(201.89, -11.25) * mm, "end": v(198.79, -11.25) * mm});
            skLineSegment(sketch, "E356", {"start": v(198.79, -11.25) * mm, "end": v(198.79, -12.05) * mm});
            skLineSegment(sketch, "E357", {"start": v(198.79, -12.05) * mm, "end": v(197.79, -12.05) * mm});
            skLineSegment(sketch, "E358", {"start": v(197.79, -12.05) * mm, "end": v(197.79, -26.05) * mm});
            skLineSegment(sketch, "E359", {"start": v(197.79, -26.05) * mm, "end": v(198.79, -26.05) * mm});
            skLineSegment(sketch, "E360", {"start": v(198.79, -26.05) * mm, "end": v(198.79, -26.85) * mm});
            skLineSegment(sketch, "E361", {"start": v(198.79, -26.85) * mm, "end": v(201.89, -26.85) * mm});
            skLineSegment(sketch, "E362", {"start": v(201.89, -26.85) * mm, "end": v(201.89, -26.05) * mm});
            skLineSegment(sketch, "E363", {"start": v(201.89, -26.05) * mm, "end": v(202.49, -26.05) * mm});
            skLineSegment(sketch, "E364", {"start": v(202.49, -26.05) * mm, "end": v(202.49, -27.62) * mm});
            skLineSegment(sketch, "E365", {"start": v(202.49, -27.62) * mm, "end": v(198.02, -27.62) * mm});
            skLineSegment(sketch, "E366", {"start": v(198.02, -27.62) * mm, "end": v(198.02, -29.3) * mm});
            skLineSegment(sketch, "E367", {"start": v(198.02, -29.3) * mm, "end": v(197.04, -29.3) * mm});
            skLineSegment(sketch, "E368", {"start": v(197.04, -29.3) * mm, "end": v(197.04, -32.6) * mm});
            skLineSegment(sketch, "E369", {"start": v(197.04, -32.6) * mm, "end": v(198.02, -32.6) * mm});
            skLineSegment(sketch, "E370", {"start": v(198.02, -32.6) * mm, "end": v(198.02, -34.27) * mm});
            skLineSegment(sketch, "E371", {"start": v(198.02, -34.27) * mm, "end": v(204.29, -34.27) * mm});
            skLineSegment(sketch, "E372", {"start": v(204.29, -34.27) * mm, "end": v(204.29, -35.15) * mm});
            skLineSegment(sketch, "E373", {"start": v(204.29, -35.15) * mm, "end": v(207.09, -35.15) * mm});
            skLineSegment(sketch, "E374", {"start": v(207.09, -35.15) * mm, "end": v(207.09, -34.27) * mm});
            skLineSegment(sketch, "E375", {"start": v(207.09, -34.27) * mm, "end": v(210.32, -34.27) * mm});
            skLineSegment(sketch, "E376", {"start": v(210.32, -34.27) * mm, "end": v(210.32, -32.6) * mm});
            skLineSegment(sketch, "E377", {"start": v(210.32, -32.6) * mm, "end": v(211.24, -32.6) * mm});
            skLineSegment(sketch, "E378", {"start": v(211.24, -32.6) * mm, "end": v(211.24, -29.3) * mm});
            skLineSegment(sketch, "E379", {"start": v(211.24, -29.3) * mm, "end": v(210.32, -29.3) * mm});
            skLineSegment(sketch, "E380", {"start": v(210.32, -29.3) * mm, "end": v(210.32, -27.62) * mm});
            skLineSegment(sketch, "E381", {"start": v(210.32, -27.62) * mm, "end": v(207.09, -27.62) * mm});
            skLineSegment(sketch, "E382", {"start": v(207.09, -27.62) * mm, "end": v(207.09, -26.05) * mm});
            skLineSegment(sketch, "E383", {"start": v(207.09, -26.05) * mm, "end": v(207.69, -26.05) * mm});
            skLineSegment(sketch, "E384", {"start": v(207.69, -26.05) * mm, "end": v(207.69, -26.85) * mm});
            skLineSegment(sketch, "E385", {"start": v(207.69, -26.85) * mm, "end": v(210.79, -26.85) * mm});
            skLineSegment(sketch, "E386", {"start": v(210.79, -26.85) * mm, "end": v(210.79, -26.05) * mm});
            skLineSegment(sketch, "E387", {"start": v(210.79, -26.05) * mm, "end": v(211.79, -26.05) * mm});
            skLineSegment(sketch, "E388", {"start": v(211.79, -26.05) * mm, "end": v(211.79, -12.05) * mm});
            skLineSegment(sketch, "E389", {"start": v(211.79, -12.05) * mm, "end": v(210.79, -12.05) * mm});
            skLineSegment(sketch, "E390", {"start": v(210.79, -12.05) * mm, "end": v(210.79, -11.25) * mm});
            skLineSegment(sketch, "E391", {"start": v(210.79, -11.25) * mm, "end": v(207.69, -11.25) * mm});
            skLineSegment(sketch, "E392", {"start": v(207.69, -11.25) * mm, "end": v(207.69, -12.05) * mm});
            skLineSegment(sketch, "E393", {"start": v(207.69, -12.05) * mm, "end": v(207.09, -12.05) * mm});
            skLineSegment(sketch, "E394", {"start": v(207.09, -12.05) * mm, "end": v(207.09, -10.47) * mm});
            skLineSegment(sketch, "E395", {"start": v(207.09, -10.47) * mm, "end": v(210.32, -10.47) * mm});
            skLineSegment(sketch, "E396", {"start": v(210.32, -10.47) * mm, "end": v(210.32, -8.8) * mm});
            skLineSegment(sketch, "E397", {"start": v(210.32, -8.8) * mm, "end": v(211.24, -8.8) * mm});
            skLineSegment(sketch, "E398", {"start": v(211.24, -8.8) * mm, "end": v(211.24, -5.5) * mm});
            skLineSegment(sketch, "E399", {"start": v(211.24, -5.5) * mm, "end": v(210.32, -5.5) * mm});
            skLineSegment(sketch, "E400", {"start": v(210.32, -5.5) * mm, "end": v(210.32, -3.82) * mm});
            skLineSegment(sketch, "E401", {"start": v(210.32, -3.82) * mm, "end": v(207.09, -3.82) * mm});
            skLineSegment(sketch, "E402", {"start": v(207.09, -3.82) * mm, "end": v(207.09, -2.95) * mm});
            skLineSegment(sketch, "E403", {"start": v(207.09, -2.95) * mm, "end": v(204.29, -2.95) * mm});
            skLineSegment(sketch, "E404", {"start": v(-142.73, -2.52) * mm, "end": v(-142.73, -3.53) * mm});
            skLineSegment(sketch, "E405", {"start": v(-142.73, -3.53) * mm, "end": v(-143.53, -3.53) * mm});
            skLineSegment(sketch, "E406", {"start": v(-143.53, -3.53) * mm, "end": v(-143.53, -6.62) * mm});
            skLineSegment(sketch, "E407", {"start": v(-143.53, -6.62) * mm, "end": v(-142.73, -6.62) * mm});
            skLineSegment(sketch, "E408", {"start": v(-142.73, -6.62) * mm, "end": v(-142.73, -7.23) * mm});
            skLineSegment(sketch, "E409", {"start": v(-142.73, -7.23) * mm, "end": v(-144.3, -7.23) * mm});
            skLineSegment(sketch, "E410", {"start": v(-144.3, -7.23) * mm, "end": v(-144.3, -4) * mm});
            skLineSegment(sketch, "E411", {"start": v(-144.3, -4) * mm, "end": v(-145.98, -4) * mm});
            skLineSegment(sketch, "E412", {"start": v(-145.98, -4) * mm, "end": v(-145.98, -3.07) * mm});
            skLineSegment(sketch, "E413", {"start": v(-145.98, -3.07) * mm, "end": v(-149.28, -3.07) * mm});
            skLineSegment(sketch, "E414", {"start": v(-149.28, -3.07) * mm, "end": v(-149.28, -4) * mm});
            skLineSegment(sketch, "E415", {"start": v(-149.28, -4) * mm, "end": v(-150.96, -4) * mm});
            skLineSegment(sketch, "E416", {"start": v(-150.96, -4) * mm, "end": v(-150.96, -7.23) * mm});
            skLineSegment(sketch, "E417", {"start": v(-150.96, -7.23) * mm, "end": v(-151.83, -7.23) * mm});
            skLineSegment(sketch, "E418", {"start": v(-151.83, -7.23) * mm, "end": v(-151.83, -10.03) * mm});
            skLineSegment(sketch, "E419", {"start": v(-151.83, -10.03) * mm, "end": v(-150.96, -10.03) * mm});
            skLineSegment(sketch, "E420", {"start": v(-150.96, -10.03) * mm, "end": v(-150.96, -16.3) * mm});
            skLineSegment(sketch, "E421", {"start": v(-150.96, -16.3) * mm, "end": v(-149.28, -16.3) * mm});
            skLineSegment(sketch, "E422", {"start": v(-149.28, -16.3) * mm, "end": v(-149.28, -17.28) * mm});
            skLineSegment(sketch, "E423", {"start": v(-149.28, -17.28) * mm, "end": v(-145.98, -17.28) * mm});
            skLineSegment(sketch, "E424", {"start": v(-145.98, -17.28) * mm, "end": v(-145.98, -16.3) * mm});
            skLineSegment(sketch, "E425", {"start": v(-145.98, -16.3) * mm, "end": v(-144.3, -16.3) * mm});
            skLineSegment(sketch, "E426", {"start": v(-144.3, -16.3) * mm, "end": v(-144.3, -11.82) * mm});
            skLineSegment(sketch, "E427", {"start": v(-144.3, -11.82) * mm, "end": v(-142.73, -11.82) * mm});
            skLineSegment(sketch, "E428", {"start": v(-142.73, -11.82) * mm, "end": v(-142.73, -12.42) * mm});
            skLineSegment(sketch, "E429", {"start": v(-142.73, -12.42) * mm, "end": v(-143.53, -12.42) * mm});
            skLineSegment(sketch, "E430", {"start": v(-143.53, -12.42) * mm, "end": v(-143.53, -15.53) * mm});
            skLineSegment(sketch, "E431", {"start": v(-143.53, -15.53) * mm, "end": v(-142.73, -15.53) * mm});
            skLineSegment(sketch, "E432", {"start": v(-142.73, -15.53) * mm, "end": v(-142.73, -16.52) * mm});
            skLineSegment(sketch, "E433", {"start": v(-142.73, -16.52) * mm, "end": v(-128.73, -16.52) * mm});
            skLineSegment(sketch, "E434", {"start": v(-128.73, -16.52) * mm, "end": v(-128.73, -15.53) * mm});
            skLineSegment(sketch, "E435", {"start": v(-128.73, -15.53) * mm, "end": v(-127.93, -15.53) * mm});
            skLineSegment(sketch, "E436", {"start": v(-127.93, -15.53) * mm, "end": v(-127.93, -12.42) * mm});
            skLineSegment(sketch, "E437", {"start": v(-127.93, -12.42) * mm, "end": v(-128.73, -12.42) * mm});
            skLineSegment(sketch, "E438", {"start": v(-128.73, -12.42) * mm, "end": v(-128.73, -11.82) * mm});
            skLineSegment(sketch, "E439", {"start": v(-128.73, -11.82) * mm, "end": v(-127.16, -11.82) * mm});
            skLineSegment(sketch, "E440", {"start": v(-127.16, -11.82) * mm, "end": v(-127.16, -16.3) * mm});
            skLineSegment(sketch, "E441", {"start": v(-127.16, -16.3) * mm, "end": v(-125.48, -16.3) * mm});
            skLineSegment(sketch, "E442", {"start": v(-125.48, -16.3) * mm, "end": v(-125.48, -17.28) * mm});
            skLineSegment(sketch, "E443", {"start": v(-125.48, -17.28) * mm, "end": v(-122.18, -17.28) * mm});
            skLineSegment(sketch, "E444", {"start": v(-122.18, -17.28) * mm, "end": v(-122.18, -16.3) * mm});
            skLineSegment(sketch, "E445", {"start": v(-122.18, -16.3) * mm, "end": v(-120.5, -16.3) * mm});
            skLineSegment(sketch, "E446", {"start": v(-120.5, -16.3) * mm, "end": v(-120.5, -10.03) * mm});
            skLineSegment(sketch, "E447", {"start": v(-120.5, -10.03) * mm, "end": v(-119.63, -10.03) * mm});
            skLineSegment(sketch, "E448", {"start": v(-119.63, -10.03) * mm, "end": v(-119.63, -7.23) * mm});
            skLineSegment(sketch, "E449", {"start": v(-119.63, -7.23) * mm, "end": v(-120.5, -7.23) * mm});
            skLineSegment(sketch, "E450", {"start": v(-120.5, -7.23) * mm, "end": v(-120.5, -4) * mm});
            skLineSegment(sketch, "E451", {"start": v(-120.5, -4) * mm, "end": v(-122.18, -4) * mm});
            skLineSegment(sketch, "E452", {"start": v(-122.18, -4) * mm, "end": v(-122.18, -3.07) * mm});
            skLineSegment(sketch, "E453", {"start": v(-122.18, -3.07) * mm, "end": v(-125.48, -3.07) * mm});
            skLineSegment(sketch, "E454", {"start": v(-125.48, -3.07) * mm, "end": v(-125.48, -4) * mm});
            skLineSegment(sketch, "E455", {"start": v(-125.48, -4) * mm, "end": v(-127.16, -4) * mm});
            skLineSegment(sketch, "E456", {"start": v(-127.16, -4) * mm, "end": v(-127.16, -7.23) * mm});
            skLineSegment(sketch, "E457", {"start": v(-127.16, -7.23) * mm, "end": v(-128.73, -7.23) * mm});
            skLineSegment(sketch, "E458", {"start": v(-128.73, -7.23) * mm, "end": v(-128.73, -6.62) * mm});
            skLineSegment(sketch, "E459", {"start": v(-128.73, -6.62) * mm, "end": v(-127.93, -6.62) * mm});
            skLineSegment(sketch, "E460", {"start": v(-127.93, -6.62) * mm, "end": v(-127.93, -3.53) * mm});
            skLineSegment(sketch, "E461", {"start": v(-127.93, -3.53) * mm, "end": v(-128.73, -3.53) * mm});
            skLineSegment(sketch, "E462", {"start": v(-128.73, -3.53) * mm, "end": v(-128.73, -2.52) * mm});
            skLineSegment(sketch, "E463", {"start": v(-128.73, -2.52) * mm, "end": v(-142.73, -2.52) * mm});
            skLineSegment(sketch, "E464", {"start": v(33.48, -2.52) * mm, "end": v(33.48, -3.53) * mm});
            skLineSegment(sketch, "E465", {"start": v(33.48, -3.53) * mm, "end": v(32.68, -3.53) * mm});
            skLineSegment(sketch, "E466", {"start": v(32.68, -3.53) * mm, "end": v(32.68, -6.62) * mm});
            skLineSegment(sketch, "E467", {"start": v(32.68, -6.62) * mm, "end": v(33.48, -6.62) * mm});
            skLineSegment(sketch, "E468", {"start": v(33.48, -6.62) * mm, "end": v(33.48, -7.23) * mm});
            skLineSegment(sketch, "E469", {"start": v(33.48, -7.23) * mm, "end": v(31.9, -7.23) * mm});
            skLineSegment(sketch, "E470", {"start": v(31.9, -7.23) * mm, "end": v(31.9, -4) * mm});
            skLineSegment(sketch, "E471", {"start": v(31.9, -4) * mm, "end": v(30.23, -4) * mm});
            skLineSegment(sketch, "E472", {"start": v(30.23, -4) * mm, "end": v(30.23, -3.07) * mm});
            skLineSegment(sketch, "E473", {"start": v(30.23, -3.07) * mm, "end": v(26.93, -3.07) * mm});
            skLineSegment(sketch, "E474", {"start": v(26.93, -3.07) * mm, "end": v(26.93, -4) * mm});
            skLineSegment(sketch, "E475", {"start": v(26.93, -4) * mm, "end": v(25.26, -4) * mm});
            skLineSegment(sketch, "E476", {"start": v(25.26, -4) * mm, "end": v(25.26, -7.23) * mm});
            skLineSegment(sketch, "E477", {"start": v(25.26, -7.23) * mm, "end": v(24.38, -7.23) * mm});
            skLineSegment(sketch, "E478", {"start": v(24.38, -7.23) * mm, "end": v(24.38, -10.03) * mm});
            skLineSegment(sketch, "E479", {"start": v(24.38, -10.03) * mm, "end": v(25.26, -10.03) * mm});
            skLineSegment(sketch, "E480", {"start": v(25.26, -10.03) * mm, "end": v(25.26, -16.3) * mm});
            skLineSegment(sketch, "E481", {"start": v(25.26, -16.3) * mm, "end": v(26.93, -16.3) * mm});
            skLineSegment(sketch, "E482", {"start": v(26.93, -16.3) * mm, "end": v(26.93, -17.28) * mm});
            skLineSegment(sketch, "E483", {"start": v(26.93, -17.28) * mm, "end": v(30.23, -17.28) * mm});
            skLineSegment(sketch, "E484", {"start": v(30.23, -17.28) * mm, "end": v(30.23, -16.3) * mm});
            skLineSegment(sketch, "E485", {"start": v(30.23, -16.3) * mm, "end": v(31.9, -16.3) * mm});
            skLineSegment(sketch, "E486", {"start": v(31.9, -16.3) * mm, "end": v(31.9, -11.82) * mm});
            skLineSegment(sketch, "E487", {"start": v(31.9, -11.82) * mm, "end": v(33.48, -11.82) * mm});
            skLineSegment(sketch, "E488", {"start": v(33.48, -11.82) * mm, "end": v(33.48, -12.42) * mm});
            skLineSegment(sketch, "E489", {"start": v(33.48, -12.42) * mm, "end": v(32.68, -12.42) * mm});
            skLineSegment(sketch, "E490", {"start": v(32.68, -12.42) * mm, "end": v(32.68, -15.53) * mm});
            skLineSegment(sketch, "E491", {"start": v(32.68, -15.53) * mm, "end": v(33.48, -15.53) * mm});
            skLineSegment(sketch, "E492", {"start": v(33.48, -15.53) * mm, "end": v(33.48, -16.52) * mm});
            skLineSegment(sketch, "E493", {"start": v(33.48, -16.52) * mm, "end": v(47.48, -16.52) * mm});
            skLineSegment(sketch, "E494", {"start": v(47.48, -16.52) * mm, "end": v(47.48, -15.53) * mm});
            skLineSegment(sketch, "E495", {"start": v(47.48, -15.53) * mm, "end": v(48.28, -15.53) * mm});
            skLineSegment(sketch, "E496", {"start": v(48.28, -15.53) * mm, "end": v(48.28, -12.42) * mm});
            skLineSegment(sketch, "E497", {"start": v(48.28, -12.42) * mm, "end": v(47.48, -12.42) * mm});
            skLineSegment(sketch, "E498", {"start": v(47.48, -12.42) * mm, "end": v(47.48, -11.82) * mm});
            skLineSegment(sketch, "E499", {"start": v(47.48, -11.82) * mm, "end": v(49.06, -11.82) * mm});
            skLineSegment(sketch, "E500", {"start": v(49.06, -11.82) * mm, "end": v(49.06, -16.3) * mm});
            skLineSegment(sketch, "E501", {"start": v(49.06, -16.3) * mm, "end": v(50.73, -16.3) * mm});
            skLineSegment(sketch, "E502", {"start": v(50.73, -16.3) * mm, "end": v(50.73, -17.28) * mm});
            skLineSegment(sketch, "E503", {"start": v(50.73, -17.28) * mm, "end": v(54.03, -17.28) * mm});
            skLineSegment(sketch, "E504", {"start": v(54.03, -17.28) * mm, "end": v(54.03, -16.3) * mm});
            skLineSegment(sketch, "E505", {"start": v(54.03, -16.3) * mm, "end": v(55.7, -16.3) * mm});
            skLineSegment(sketch, "E506", {"start": v(55.7, -16.3) * mm, "end": v(55.7, -10.03) * mm});
            skLineSegment(sketch, "E507", {"start": v(55.7, -10.03) * mm, "end": v(56.58, -10.03) * mm});
            skLineSegment(sketch, "E508", {"start": v(56.58, -10.03) * mm, "end": v(56.58, -7.23) * mm});
            skLineSegment(sketch, "E509", {"start": v(56.58, -7.23) * mm, "end": v(55.7, -7.23) * mm});
            skLineSegment(sketch, "E510", {"start": v(55.7, -7.23) * mm, "end": v(55.7, -4) * mm});
            skLineSegment(sketch, "E511", {"start": v(55.7, -4) * mm, "end": v(54.03, -4) * mm});
            skLineSegment(sketch, "E512", {"start": v(54.03, -4) * mm, "end": v(54.03, -3.07) * mm});
            skLineSegment(sketch, "E513", {"start": v(54.03, -3.07) * mm, "end": v(50.73, -3.07) * mm});
            skLineSegment(sketch, "E514", {"start": v(50.73, -3.07) * mm, "end": v(50.73, -4) * mm});
            skLineSegment(sketch, "E515", {"start": v(50.73, -4) * mm, "end": v(49.06, -4) * mm});
            skLineSegment(sketch, "E516", {"start": v(49.06, -4) * mm, "end": v(49.06, -7.23) * mm});
            skLineSegment(sketch, "E517", {"start": v(49.06, -7.23) * mm, "end": v(47.48, -7.23) * mm});
            skLineSegment(sketch, "E518", {"start": v(47.48, -7.23) * mm, "end": v(47.48, -6.62) * mm});
            skLineSegment(sketch, "E519", {"start": v(47.48, -6.62) * mm, "end": v(48.28, -6.62) * mm});
            skLineSegment(sketch, "E520", {"start": v(48.28, -6.62) * mm, "end": v(48.28, -3.53) * mm});
            skLineSegment(sketch, "E521", {"start": v(48.28, -3.53) * mm, "end": v(47.48, -3.53) * mm});
            skLineSegment(sketch, "E522", {"start": v(47.48, -3.53) * mm, "end": v(47.48, -2.52) * mm});
            skLineSegment(sketch, "E523", {"start": v(47.48, -2.52) * mm, "end": v(33.48, -2.52) * mm});
            skLineSegment(sketch, "E524", {"start": v(-111.78, -2.52) * mm, "end": v(-111.78, -3.53) * mm});
            skLineSegment(sketch, "E525", {"start": v(-111.78, -3.53) * mm, "end": v(-112.58, -3.53) * mm});
            skLineSegment(sketch, "E526", {"start": v(-112.58, -3.53) * mm, "end": v(-112.58, -6.62) * mm});
            skLineSegment(sketch, "E527", {"start": v(-112.58, -6.62) * mm, "end": v(-111.78, -6.62) * mm});
            skLineSegment(sketch, "E528", {"start": v(-111.78, -6.62) * mm, "end": v(-111.78, -12.42) * mm});
            skLineSegment(sketch, "E529", {"start": v(-111.78, -12.42) * mm, "end": v(-112.58, -12.42) * mm});
            skLineSegment(sketch, "E530", {"start": v(-112.58, -12.42) * mm, "end": v(-112.58, -15.53) * mm});
            skLineSegment(sketch, "E531", {"start": v(-112.58, -15.53) * mm, "end": v(-111.78, -15.53) * mm});
            skLineSegment(sketch, "E532", {"start": v(-111.78, -15.53) * mm, "end": v(-111.78, -16.52) * mm});
            skLineSegment(sketch, "E533", {"start": v(-111.78, -16.52) * mm, "end": v(-97.78, -16.52) * mm});
            skLineSegment(sketch, "E534", {"start": v(-97.78, -16.52) * mm, "end": v(-97.78, -15.53) * mm});
            skLineSegment(sketch, "E535", {"start": v(-97.78, -15.53) * mm, "end": v(-96.98, -15.53) * mm});
            skLineSegment(sketch, "E536", {"start": v(-96.98, -15.53) * mm, "end": v(-96.98, -12.42) * mm});
            skLineSegment(sketch, "E537", {"start": v(-96.98, -12.42) * mm, "end": v(-97.78, -12.42) * mm});
            skLineSegment(sketch, "E538", {"start": v(-97.78, -12.42) * mm, "end": v(-97.78, -6.62) * mm});
            skLineSegment(sketch, "E539", {"start": v(-97.78, -6.62) * mm, "end": v(-96.98, -6.62) * mm});
            skLineSegment(sketch, "E540", {"start": v(-96.98, -6.62) * mm, "end": v(-96.98, -3.53) * mm});
            skLineSegment(sketch, "E541", {"start": v(-96.98, -3.53) * mm, "end": v(-97.78, -3.53) * mm});
            skLineSegment(sketch, "E542", {"start": v(-97.78, -3.53) * mm, "end": v(-97.78, -2.52) * mm});
            skLineSegment(sketch, "E543", {"start": v(-97.78, -2.52) * mm, "end": v(-111.78, -2.52) * mm});
            skLineSegment(sketch, "E544", {"start": v(-92.73, -2.52) * mm, "end": v(-92.73, -3.53) * mm});
            skLineSegment(sketch, "E545", {"start": v(-92.73, -3.53) * mm, "end": v(-93.53, -3.53) * mm});
            skLineSegment(sketch, "E546", {"start": v(-93.53, -3.53) * mm, "end": v(-93.53, -6.62) * mm});
            skLineSegment(sketch, "E547", {"start": v(-93.53, -6.62) * mm, "end": v(-92.73, -6.62) * mm});
            skLineSegment(sketch, "E548", {"start": v(-92.73, -6.62) * mm, "end": v(-92.73, -12.42) * mm});
            skLineSegment(sketch, "E549", {"start": v(-92.73, -12.42) * mm, "end": v(-93.53, -12.42) * mm});
            skLineSegment(sketch, "E550", {"start": v(-93.53, -12.42) * mm, "end": v(-93.53, -15.53) * mm});
            skLineSegment(sketch, "E551", {"start": v(-93.53, -15.53) * mm, "end": v(-92.73, -15.53) * mm});
            skLineSegment(sketch, "E552", {"start": v(-92.73, -15.53) * mm, "end": v(-92.73, -16.52) * mm});
            skLineSegment(sketch, "E553", {"start": v(-92.73, -16.52) * mm, "end": v(-78.73, -16.52) * mm});
            skLineSegment(sketch, "E554", {"start": v(-78.73, -16.52) * mm, "end": v(-78.73, -15.53) * mm});
            skLineSegment(sketch, "E555", {"start": v(-78.73, -15.53) * mm, "end": v(-77.93, -15.53) * mm});
            skLineSegment(sketch, "E556", {"start": v(-77.93, -15.53) * mm, "end": v(-77.93, -12.42) * mm});
            skLineSegment(sketch, "E557", {"start": v(-77.93, -12.42) * mm, "end": v(-78.73, -12.42) * mm});
            skLineSegment(sketch, "E558", {"start": v(-78.73, -12.42) * mm, "end": v(-78.73, -6.62) * mm});
            skLineSegment(sketch, "E559", {"start": v(-78.73, -6.62) * mm, "end": v(-77.93, -6.62) * mm});
            skLineSegment(sketch, "E560", {"start": v(-77.93, -6.62) * mm, "end": v(-77.93, -3.53) * mm});
            skLineSegment(sketch, "E561", {"start": v(-77.93, -3.53) * mm, "end": v(-78.73, -3.53) * mm});
            skLineSegment(sketch, "E562", {"start": v(-78.73, -3.53) * mm, "end": v(-78.73, -2.52) * mm});
            skLineSegment(sketch, "E563", {"start": v(-78.73, -2.52) * mm, "end": v(-92.73, -2.52) * mm});
            skLineSegment(sketch, "E564", {"start": v(-73.68, -2.52) * mm, "end": v(-73.68, -3.53) * mm});
            skLineSegment(sketch, "E565", {"start": v(-73.68, -3.53) * mm, "end": v(-74.48, -3.53) * mm});
            skLineSegment(sketch, "E566", {"start": v(-74.48, -3.53) * mm, "end": v(-74.48, -6.62) * mm});
            skLineSegment(sketch, "E567", {"start": v(-74.48, -6.62) * mm, "end": v(-73.68, -6.62) * mm});
            skLineSegment(sketch, "E568", {"start": v(-73.68, -6.62) * mm, "end": v(-73.68, -12.42) * mm});
            skLineSegment(sketch, "E569", {"start": v(-73.68, -12.42) * mm, "end": v(-74.48, -12.42) * mm});
            skLineSegment(sketch, "E570", {"start": v(-74.48, -12.42) * mm, "end": v(-74.48, -15.53) * mm});
            skLineSegment(sketch, "E571", {"start": v(-74.48, -15.53) * mm, "end": v(-73.68, -15.53) * mm});
            skLineSegment(sketch, "E572", {"start": v(-73.68, -15.53) * mm, "end": v(-73.68, -16.52) * mm});
            skLineSegment(sketch, "E573", {"start": v(-73.68, -16.52) * mm, "end": v(-59.68, -16.52) * mm});
            skLineSegment(sketch, "E574", {"start": v(-59.68, -16.52) * mm, "end": v(-59.68, -15.53) * mm});
            skLineSegment(sketch, "E575", {"start": v(-59.68, -15.53) * mm, "end": v(-58.88, -15.53) * mm});
            skLineSegment(sketch, "E576", {"start": v(-58.88, -15.53) * mm, "end": v(-58.88, -12.42) * mm});
            skLineSegment(sketch, "E577", {"start": v(-58.88, -12.42) * mm, "end": v(-59.68, -12.42) * mm});
            skLineSegment(sketch, "E578", {"start": v(-59.68, -12.42) * mm, "end": v(-59.68, -6.62) * mm});
            skLineSegment(sketch, "E579", {"start": v(-59.68, -6.62) * mm, "end": v(-58.88, -6.62) * mm});
            skLineSegment(sketch, "E580", {"start": v(-58.88, -6.62) * mm, "end": v(-58.88, -3.53) * mm});
            skLineSegment(sketch, "E581", {"start": v(-58.88, -3.53) * mm, "end": v(-59.68, -3.53) * mm});
            skLineSegment(sketch, "E582", {"start": v(-59.68, -3.53) * mm, "end": v(-59.68, -2.52) * mm});
            skLineSegment(sketch, "E583", {"start": v(-59.68, -2.52) * mm, "end": v(-73.68, -2.52) * mm});
            skLineSegment(sketch, "E584", {"start": v(-54.63, -2.52) * mm, "end": v(-54.63, -3.53) * mm});
            skLineSegment(sketch, "E585", {"start": v(-54.63, -3.53) * mm, "end": v(-55.43, -3.53) * mm});
            skLineSegment(sketch, "E586", {"start": v(-55.43, -3.53) * mm, "end": v(-55.43, -6.62) * mm});
            skLineSegment(sketch, "E587", {"start": v(-55.43, -6.62) * mm, "end": v(-54.63, -6.62) * mm});
            skLineSegment(sketch, "E588", {"start": v(-54.63, -6.62) * mm, "end": v(-54.63, -12.42) * mm});
            skLineSegment(sketch, "E589", {"start": v(-54.63, -12.42) * mm, "end": v(-55.43, -12.42) * mm});
            skLineSegment(sketch, "E590", {"start": v(-55.43, -12.42) * mm, "end": v(-55.43, -15.53) * mm});
            skLineSegment(sketch, "E591", {"start": v(-55.43, -15.53) * mm, "end": v(-54.63, -15.53) * mm});
            skLineSegment(sketch, "E592", {"start": v(-54.63, -15.53) * mm, "end": v(-54.63, -16.52) * mm});
            skLineSegment(sketch, "E593", {"start": v(-54.63, -16.52) * mm, "end": v(-40.63, -16.52) * mm});
            skLineSegment(sketch, "E594", {"start": v(-40.63, -16.52) * mm, "end": v(-40.63, -15.53) * mm});
            skLineSegment(sketch, "E595", {"start": v(-40.63, -15.53) * mm, "end": v(-39.83, -15.53) * mm});
            skLineSegment(sketch, "E596", {"start": v(-39.83, -15.53) * mm, "end": v(-39.83, -12.42) * mm});
            skLineSegment(sketch, "E597", {"start": v(-39.83, -12.42) * mm, "end": v(-40.63, -12.42) * mm});
            skLineSegment(sketch, "E598", {"start": v(-40.63, -12.42) * mm, "end": v(-40.63, -6.62) * mm});
            skLineSegment(sketch, "E599", {"start": v(-40.63, -6.62) * mm, "end": v(-39.83, -6.62) * mm});
            skLineSegment(sketch, "E600", {"start": v(-39.83, -6.62) * mm, "end": v(-39.83, -3.53) * mm});
            skLineSegment(sketch, "E601", {"start": v(-39.83, -3.53) * mm, "end": v(-40.63, -3.53) * mm});
            skLineSegment(sketch, "E602", {"start": v(-40.63, -3.53) * mm, "end": v(-40.63, -2.52) * mm});
            skLineSegment(sketch, "E603", {"start": v(-40.63, -2.52) * mm, "end": v(-54.63, -2.52) * mm});
            skLineSegment(sketch, "E604", {"start": v(-35.58, -2.52) * mm, "end": v(-35.58, -3.53) * mm});
            skLineSegment(sketch, "E605", {"start": v(-35.58, -3.53) * mm, "end": v(-36.38, -3.53) * mm});
            skLineSegment(sketch, "E606", {"start": v(-36.38, -3.53) * mm, "end": v(-36.38, -6.62) * mm});
            skLineSegment(sketch, "E607", {"start": v(-36.38, -6.62) * mm, "end": v(-35.58, -6.62) * mm});
            skLineSegment(sketch, "E608", {"start": v(-35.58, -6.62) * mm, "end": v(-35.58, -12.42) * mm});
            skLineSegment(sketch, "E609", {"start": v(-35.58, -12.42) * mm, "end": v(-36.38, -12.42) * mm});
            skLineSegment(sketch, "E610", {"start": v(-36.38, -12.42) * mm, "end": v(-36.38, -15.53) * mm});
            skLineSegment(sketch, "E611", {"start": v(-36.38, -15.53) * mm, "end": v(-35.58, -15.53) * mm});
            skLineSegment(sketch, "E612", {"start": v(-35.58, -15.53) * mm, "end": v(-35.58, -16.52) * mm});
            skLineSegment(sketch, "E613", {"start": v(-35.58, -16.52) * mm, "end": v(-21.58, -16.52) * mm});
            skLineSegment(sketch, "E614", {"start": v(-21.58, -16.52) * mm, "end": v(-21.58, -15.53) * mm});
            skLineSegment(sketch, "E615", {"start": v(-21.58, -15.53) * mm, "end": v(-20.78, -15.53) * mm});
            skLineSegment(sketch, "E616", {"start": v(-20.78, -15.53) * mm, "end": v(-20.78, -12.42) * mm});
            skLineSegment(sketch, "E617", {"start": v(-20.78, -12.42) * mm, "end": v(-21.58, -12.42) * mm});
            skLineSegment(sketch, "E618", {"start": v(-21.58, -12.42) * mm, "end": v(-21.58, -6.62) * mm});
            skLineSegment(sketch, "E619", {"start": v(-21.58, -6.62) * mm, "end": v(-20.78, -6.62) * mm});
            skLineSegment(sketch, "E620", {"start": v(-20.78, -6.62) * mm, "end": v(-20.78, -3.53) * mm});
            skLineSegment(sketch, "E621", {"start": v(-20.78, -3.53) * mm, "end": v(-21.58, -3.53) * mm});
            skLineSegment(sketch, "E622", {"start": v(-21.58, -3.53) * mm, "end": v(-21.58, -2.52) * mm});
            skLineSegment(sketch, "E623", {"start": v(-21.58, -2.52) * mm, "end": v(-35.58, -2.52) * mm});
            skLineSegment(sketch, "E624", {"start": v(-16.53, -2.52) * mm, "end": v(-16.53, -3.53) * mm});
            skLineSegment(sketch, "E625", {"start": v(-16.53, -3.53) * mm, "end": v(-17.33, -3.53) * mm});
            skLineSegment(sketch, "E626", {"start": v(-17.33, -3.53) * mm, "end": v(-17.33, -6.62) * mm});
            skLineSegment(sketch, "E627", {"start": v(-17.33, -6.62) * mm, "end": v(-16.53, -6.62) * mm});
            skLineSegment(sketch, "E628", {"start": v(-16.53, -6.62) * mm, "end": v(-16.53, -12.42) * mm});
            skLineSegment(sketch, "E629", {"start": v(-16.53, -12.42) * mm, "end": v(-17.33, -12.42) * mm});
            skLineSegment(sketch, "E630", {"start": v(-17.33, -12.42) * mm, "end": v(-17.33, -15.53) * mm});
            skLineSegment(sketch, "E631", {"start": v(-17.33, -15.53) * mm, "end": v(-16.53, -15.53) * mm});
            skLineSegment(sketch, "E632", {"start": v(-16.53, -15.53) * mm, "end": v(-16.53, -16.52) * mm});
            skLineSegment(sketch, "E633", {"start": v(-16.53, -16.52) * mm, "end": v(-2.53, -16.52) * mm});
            skLineSegment(sketch, "E634", {"start": v(-2.53, -16.52) * mm, "end": v(-2.53, -15.53) * mm});
            skLineSegment(sketch, "E635", {"start": v(-2.53, -15.53) * mm, "end": v(-1.73, -15.53) * mm});
            skLineSegment(sketch, "E636", {"start": v(-1.73, -15.53) * mm, "end": v(-1.73, -12.42) * mm});
            skLineSegment(sketch, "E637", {"start": v(-1.73, -12.42) * mm, "end": v(-2.53, -12.42) * mm});
            skLineSegment(sketch, "E638", {"start": v(-2.53, -12.42) * mm, "end": v(-2.53, -6.62) * mm});
            skLineSegment(sketch, "E639", {"start": v(-2.53, -6.62) * mm, "end": v(-1.73, -6.62) * mm});
            skLineSegment(sketch, "E640", {"start": v(-1.73, -6.62) * mm, "end": v(-1.73, -3.53) * mm});
            skLineSegment(sketch, "E641", {"start": v(-1.73, -3.53) * mm, "end": v(-2.53, -3.53) * mm});
            skLineSegment(sketch, "E642", {"start": v(-2.53, -3.53) * mm, "end": v(-2.53, -2.52) * mm});
            skLineSegment(sketch, "E643", {"start": v(-2.53, -2.52) * mm, "end": v(-16.53, -2.52) * mm});
            skLineSegment(sketch, "E644", {"start": v(2.52, -2.52) * mm, "end": v(2.52, -3.53) * mm});
            skLineSegment(sketch, "E645", {"start": v(2.52, -3.53) * mm, "end": v(1.72, -3.53) * mm});
            skLineSegment(sketch, "E646", {"start": v(1.72, -3.53) * mm, "end": v(1.72, -6.62) * mm});
            skLineSegment(sketch, "E647", {"start": v(1.72, -6.62) * mm, "end": v(2.52, -6.62) * mm});
            skLineSegment(sketch, "E648", {"start": v(2.52, -6.62) * mm, "end": v(2.52, -12.42) * mm});
            skLineSegment(sketch, "E649", {"start": v(2.52, -12.42) * mm, "end": v(1.72, -12.42) * mm});
            skLineSegment(sketch, "E650", {"start": v(1.72, -12.42) * mm, "end": v(1.72, -15.53) * mm});
            skLineSegment(sketch, "E651", {"start": v(1.72, -15.53) * mm, "end": v(2.52, -15.53) * mm});
            skLineSegment(sketch, "E652", {"start": v(2.52, -15.53) * mm, "end": v(2.52, -16.52) * mm});
            skLineSegment(sketch, "E653", {"start": v(2.52, -16.52) * mm, "end": v(16.52, -16.52) * mm});
            skLineSegment(sketch, "E654", {"start": v(16.52, -16.52) * mm, "end": v(16.52, -15.53) * mm});
            skLineSegment(sketch, "E655", {"start": v(16.52, -15.53) * mm, "end": v(17.32, -15.53) * mm});
            skLineSegment(sketch, "E656", {"start": v(17.32, -15.53) * mm, "end": v(17.32, -12.42) * mm});
            skLineSegment(sketch, "E657", {"start": v(17.32, -12.42) * mm, "end": v(16.52, -12.42) * mm});
            skLineSegment(sketch, "E658", {"start": v(16.52, -12.42) * mm, "end": v(16.52, -6.62) * mm});
            skLineSegment(sketch, "E659", {"start": v(16.52, -6.62) * mm, "end": v(17.32, -6.62) * mm});
            skLineSegment(sketch, "E660", {"start": v(17.32, -6.62) * mm, "end": v(17.32, -3.53) * mm});
            skLineSegment(sketch, "E661", {"start": v(17.32, -3.53) * mm, "end": v(16.52, -3.53) * mm});
            skLineSegment(sketch, "E662", {"start": v(16.52, -3.53) * mm, "end": v(16.52, -2.52) * mm});
            skLineSegment(sketch, "E663", {"start": v(16.52, -2.52) * mm, "end": v(2.52, -2.52) * mm});
            skLineSegment(sketch, "E664", {"start": v(93.01, -2.52) * mm, "end": v(93.01, -3.53) * mm});
            skLineSegment(sketch, "E665", {"start": v(93.01, -3.53) * mm, "end": v(92.21, -3.53) * mm});
            skLineSegment(sketch, "E666", {"start": v(92.21, -3.53) * mm, "end": v(92.21, -6.62) * mm});
            skLineSegment(sketch, "E667", {"start": v(92.21, -6.62) * mm, "end": v(93.01, -6.62) * mm});
            skLineSegment(sketch, "E668", {"start": v(93.01, -6.62) * mm, "end": v(93.01, -12.42) * mm});
            skLineSegment(sketch, "E669", {"start": v(93.01, -12.42) * mm, "end": v(92.21, -12.42) * mm});
            skLineSegment(sketch, "E670", {"start": v(92.21, -12.42) * mm, "end": v(92.21, -15.53) * mm});
            skLineSegment(sketch, "E671", {"start": v(92.21, -15.53) * mm, "end": v(93.01, -15.53) * mm});
            skLineSegment(sketch, "E672", {"start": v(93.01, -15.53) * mm, "end": v(93.01, -16.52) * mm});
            skLineSegment(sketch, "E673", {"start": v(93.01, -16.52) * mm, "end": v(107.01, -16.52) * mm});
            skLineSegment(sketch, "E674", {"start": v(107.01, -16.52) * mm, "end": v(107.01, -15.53) * mm});
            skLineSegment(sketch, "E675", {"start": v(107.01, -15.53) * mm, "end": v(107.81, -15.53) * mm});
            skLineSegment(sketch, "E676", {"start": v(107.81, -15.53) * mm, "end": v(107.81, -12.42) * mm});
            skLineSegment(sketch, "E677", {"start": v(107.81, -12.42) * mm, "end": v(107.01, -12.42) * mm});
            skLineSegment(sketch, "E678", {"start": v(107.01, -12.42) * mm, "end": v(107.01, -6.62) * mm});
            skLineSegment(sketch, "E679", {"start": v(107.01, -6.62) * mm, "end": v(107.81, -6.62) * mm});
            skLineSegment(sketch, "E680", {"start": v(107.81, -6.62) * mm, "end": v(107.81, -3.53) * mm});
            skLineSegment(sketch, "E681", {"start": v(107.81, -3.53) * mm, "end": v(107.01, -3.53) * mm});
            skLineSegment(sketch, "E682", {"start": v(107.01, -3.53) * mm, "end": v(107.01, -2.52) * mm});
            skLineSegment(sketch, "E683", {"start": v(107.01, -2.52) * mm, "end": v(93.01, -2.52) * mm});
            skLineSegment(sketch, "E684", {"start": v(140.64, -2.52) * mm, "end": v(140.64, -3.53) * mm});
            skLineSegment(sketch, "E685", {"start": v(140.64, -3.53) * mm, "end": v(139.84, -3.53) * mm});
            skLineSegment(sketch, "E686", {"start": v(139.84, -3.53) * mm, "end": v(139.84, -6.62) * mm});
            skLineSegment(sketch, "E687", {"start": v(139.84, -6.62) * mm, "end": v(140.64, -6.62) * mm});
            skLineSegment(sketch, "E688", {"start": v(140.64, -6.62) * mm, "end": v(140.64, -12.42) * mm});
            skLineSegment(sketch, "E689", {"start": v(140.64, -12.42) * mm, "end": v(139.84, -12.42) * mm});
            skLineSegment(sketch, "E690", {"start": v(139.84, -12.42) * mm, "end": v(139.84, -15.53) * mm});
            skLineSegment(sketch, "E691", {"start": v(139.84, -15.53) * mm, "end": v(140.64, -15.53) * mm});
            skLineSegment(sketch, "E692", {"start": v(140.64, -15.53) * mm, "end": v(140.64, -16.52) * mm});
            skLineSegment(sketch, "E693", {"start": v(140.64, -16.52) * mm, "end": v(154.64, -16.52) * mm});
            skLineSegment(sketch, "E694", {"start": v(154.64, -16.52) * mm, "end": v(154.64, -15.53) * mm});
            skLineSegment(sketch, "E695", {"start": v(154.64, -15.53) * mm, "end": v(155.44, -15.53) * mm});
            skLineSegment(sketch, "E696", {"start": v(155.44, -15.53) * mm, "end": v(155.44, -12.42) * mm});
            skLineSegment(sketch, "E697", {"start": v(155.44, -12.42) * mm, "end": v(154.64, -12.42) * mm});
            skLineSegment(sketch, "E698", {"start": v(154.64, -12.42) * mm, "end": v(154.64, -6.62) * mm});
            skLineSegment(sketch, "E699", {"start": v(154.64, -6.62) * mm, "end": v(155.44, -6.62) * mm});
            skLineSegment(sketch, "E700", {"start": v(155.44, -6.62) * mm, "end": v(155.44, -3.53) * mm});
            skLineSegment(sketch, "E701", {"start": v(155.44, -3.53) * mm, "end": v(154.64, -3.53) * mm});
            skLineSegment(sketch, "E702", {"start": v(154.64, -3.53) * mm, "end": v(154.64, -2.52) * mm});
            skLineSegment(sketch, "E703", {"start": v(154.64, -2.52) * mm, "end": v(140.64, -2.52) * mm});
            skLineSegment(sketch, "E704", {"start": v(159.69, -2.52) * mm, "end": v(159.69, -3.53) * mm});
            skLineSegment(sketch, "E705", {"start": v(159.69, -3.53) * mm, "end": v(158.89, -3.53) * mm});
            skLineSegment(sketch, "E706", {"start": v(158.89, -3.53) * mm, "end": v(158.89, -6.62) * mm});
            skLineSegment(sketch, "E707", {"start": v(158.89, -6.62) * mm, "end": v(159.69, -6.62) * mm});
            skLineSegment(sketch, "E708", {"start": v(159.69, -6.62) * mm, "end": v(159.69, -12.42) * mm});
            skLineSegment(sketch, "E709", {"start": v(159.69, -12.42) * mm, "end": v(158.89, -12.42) * mm});
            skLineSegment(sketch, "E710", {"start": v(158.89, -12.42) * mm, "end": v(158.89, -15.53) * mm});
            skLineSegment(sketch, "E711", {"start": v(158.89, -15.53) * mm, "end": v(159.69, -15.53) * mm});
            skLineSegment(sketch, "E712", {"start": v(159.69, -15.53) * mm, "end": v(159.69, -16.52) * mm});
            skLineSegment(sketch, "E713", {"start": v(159.69, -16.52) * mm, "end": v(173.69, -16.52) * mm});
            skLineSegment(sketch, "E714", {"start": v(173.69, -16.52) * mm, "end": v(173.69, -15.53) * mm});
            skLineSegment(sketch, "E715", {"start": v(173.69, -15.53) * mm, "end": v(174.49, -15.53) * mm});
            skLineSegment(sketch, "E716", {"start": v(174.49, -15.53) * mm, "end": v(174.49, -12.42) * mm});
            skLineSegment(sketch, "E717", {"start": v(174.49, -12.42) * mm, "end": v(173.69, -12.42) * mm});
            skLineSegment(sketch, "E718", {"start": v(173.69, -12.42) * mm, "end": v(173.69, -6.62) * mm});
            skLineSegment(sketch, "E719", {"start": v(173.69, -6.62) * mm, "end": v(174.49, -6.62) * mm});
            skLineSegment(sketch, "E720", {"start": v(174.49, -6.62) * mm, "end": v(174.49, -3.53) * mm});
            skLineSegment(sketch, "E721", {"start": v(174.49, -3.53) * mm, "end": v(173.69, -3.53) * mm});
            skLineSegment(sketch, "E722", {"start": v(173.69, -3.53) * mm, "end": v(173.69, -2.52) * mm});
            skLineSegment(sketch, "E723", {"start": v(173.69, -2.52) * mm, "end": v(159.69, -2.52) * mm});
            skLineSegment(sketch, "E724", {"start": v(178.74, -2.52) * mm, "end": v(178.74, -3.53) * mm});
            skLineSegment(sketch, "E725", {"start": v(178.74, -3.53) * mm, "end": v(177.94, -3.53) * mm});
            skLineSegment(sketch, "E726", {"start": v(177.94, -3.53) * mm, "end": v(177.94, -6.62) * mm});
            skLineSegment(sketch, "E727", {"start": v(177.94, -6.62) * mm, "end": v(178.74, -6.62) * mm});
            skLineSegment(sketch, "E728", {"start": v(178.74, -6.62) * mm, "end": v(178.74, -12.42) * mm});
            skLineSegment(sketch, "E729", {"start": v(178.74, -12.42) * mm, "end": v(177.94, -12.42) * mm});
            skLineSegment(sketch, "E730", {"start": v(177.94, -12.42) * mm, "end": v(177.94, -15.53) * mm});
            skLineSegment(sketch, "E731", {"start": v(177.94, -15.53) * mm, "end": v(178.74, -15.53) * mm});
            skLineSegment(sketch, "E732", {"start": v(178.74, -15.53) * mm, "end": v(178.74, -16.52) * mm});
            skLineSegment(sketch, "E733", {"start": v(178.74, -16.52) * mm, "end": v(192.74, -16.52) * mm});
            skLineSegment(sketch, "E734", {"start": v(192.74, -16.52) * mm, "end": v(192.74, -15.53) * mm});
            skLineSegment(sketch, "E735", {"start": v(192.74, -15.53) * mm, "end": v(193.54, -15.53) * mm});
            skLineSegment(sketch, "E736", {"start": v(193.54, -15.53) * mm, "end": v(193.54, -12.42) * mm});
            skLineSegment(sketch, "E737", {"start": v(193.54, -12.42) * mm, "end": v(192.74, -12.42) * mm});
            skLineSegment(sketch, "E738", {"start": v(192.74, -12.42) * mm, "end": v(192.74, -6.62) * mm});
            skLineSegment(sketch, "E739", {"start": v(192.74, -6.62) * mm, "end": v(193.54, -6.62) * mm});
            skLineSegment(sketch, "E740", {"start": v(193.54, -6.62) * mm, "end": v(193.54, -3.53) * mm});
            skLineSegment(sketch, "E741", {"start": v(193.54, -3.53) * mm, "end": v(192.74, -3.53) * mm});
            skLineSegment(sketch, "E742", {"start": v(192.74, -3.53) * mm, "end": v(192.74, -2.52) * mm});
            skLineSegment(sketch, "E743", {"start": v(192.74, -2.52) * mm, "end": v(178.74, -2.52) * mm});
            skLineSegment(sketch, "E744", {"start": v(-176.71, 16.1) * mm, "end": v(-176.71, 15.23) * mm});
            skLineSegment(sketch, "E745", {"start": v(-176.71, 15.23) * mm, "end": v(-182.98, 15.23) * mm});
            skLineSegment(sketch, "E746", {"start": v(-182.98, 15.23) * mm, "end": v(-182.98, 13.55) * mm});
            skLineSegment(sketch, "E747", {"start": v(-182.98, 13.55) * mm, "end": v(-183.96, 13.55) * mm});
            skLineSegment(sketch, "E748", {"start": v(-183.96, 13.55) * mm, "end": v(-183.96, 10.25) * mm});
            skLineSegment(sketch, "E749", {"start": v(-183.96, 10.25) * mm, "end": v(-182.98, 10.25) * mm});
            skLineSegment(sketch, "E750", {"start": v(-182.98, 10.25) * mm, "end": v(-182.98, 8.58) * mm});
            skLineSegment(sketch, "E751", {"start": v(-182.98, 8.58) * mm, "end": v(-178.51, 8.58) * mm});
            skLineSegment(sketch, "E752", {"start": v(-178.51, 8.58) * mm, "end": v(-178.51, 7) * mm});
            skLineSegment(sketch, "E753", {"start": v(-178.51, 7) * mm, "end": v(-179.11, 7) * mm});
            skLineSegment(sketch, "E754", {"start": v(-179.11, 7) * mm, "end": v(-179.11, 7.8) * mm});
            skLineSegment(sketch, "E755", {"start": v(-179.11, 7.8) * mm, "end": v(-182.21, 7.8) * mm});
            skLineSegment(sketch, "E756", {"start": v(-182.21, 7.8) * mm, "end": v(-182.21, 7) * mm});
            skLineSegment(sketch, "E757", {"start": v(-182.21, 7) * mm, "end": v(-183.21, 7) * mm});
            skLineSegment(sketch, "E758", {"start": v(-183.21, 7) * mm, "end": v(-183.21, -7) * mm});
            skLineSegment(sketch, "E759", {"start": v(-183.21, -7) * mm, "end": v(-182.21, -7) * mm});
            skLineSegment(sketch, "E760", {"start": v(-182.21, -7) * mm, "end": v(-182.21, -7.8) * mm});
            skLineSegment(sketch, "E761", {"start": v(-182.21, -7.8) * mm, "end": v(-179.11, -7.8) * mm});
            skLineSegment(sketch, "E762", {"start": v(-179.11, -7.8) * mm, "end": v(-179.11, -7) * mm});
            skLineSegment(sketch, "E763", {"start": v(-179.11, -7) * mm, "end": v(-178.51, -7) * mm});
            skLineSegment(sketch, "E764", {"start": v(-178.51, -7) * mm, "end": v(-178.51, -8.57) * mm});
            skLineSegment(sketch, "E765", {"start": v(-178.51, -8.57) * mm, "end": v(-182.98, -8.57) * mm});
            skLineSegment(sketch, "E766", {"start": v(-182.98, -8.57) * mm, "end": v(-182.98, -10.25) * mm});
            skLineSegment(sketch, "E767", {"start": v(-182.98, -10.25) * mm, "end": v(-183.96, -10.25) * mm});
            skLineSegment(sketch, "E768", {"start": v(-183.96, -10.25) * mm, "end": v(-183.96, -13.55) * mm});
            skLineSegment(sketch, "E769", {"start": v(-183.96, -13.55) * mm, "end": v(-182.98, -13.55) * mm});
            skLineSegment(sketch, "E770", {"start": v(-182.98, -13.55) * mm, "end": v(-182.98, -15.22) * mm});
            skLineSegment(sketch, "E771", {"start": v(-182.98, -15.22) * mm, "end": v(-176.71, -15.22) * mm});
            skLineSegment(sketch, "E772", {"start": v(-176.71, -15.22) * mm, "end": v(-176.71, -16.1) * mm});
            skLineSegment(sketch, "E773", {"start": v(-176.71, -16.1) * mm, "end": v(-173.91, -16.1) * mm});
            skLineSegment(sketch, "E774", {"start": v(-173.91, -16.1) * mm, "end": v(-173.91, -15.22) * mm});
            skLineSegment(sketch, "E775", {"start": v(-173.91, -15.22) * mm, "end": v(-170.68, -15.22) * mm});
            skLineSegment(sketch, "E776", {"start": v(-170.68, -15.22) * mm, "end": v(-170.68, -13.55) * mm});
            skLineSegment(sketch, "E777", {"start": v(-170.68, -13.55) * mm, "end": v(-169.76, -13.55) * mm});
            skLineSegment(sketch, "E778", {"start": v(-169.76, -13.55) * mm, "end": v(-169.76, -10.25) * mm});
            skLineSegment(sketch, "E779", {"start": v(-169.76, -10.25) * mm, "end": v(-170.68, -10.25) * mm});
            skLineSegment(sketch, "E780", {"start": v(-170.68, -10.25) * mm, "end": v(-170.68, -8.57) * mm});
            skLineSegment(sketch, "E781", {"start": v(-170.68, -8.57) * mm, "end": v(-173.91, -8.57) * mm});
            skLineSegment(sketch, "E782", {"start": v(-173.91, -8.57) * mm, "end": v(-173.91, -7) * mm});
            skLineSegment(sketch, "E783", {"start": v(-173.91, -7) * mm, "end": v(-173.31, -7) * mm});
            skLineSegment(sketch, "E784", {"start": v(-173.31, -7) * mm, "end": v(-173.31, -7.8) * mm});
            skLineSegment(sketch, "E785", {"start": v(-173.31, -7.8) * mm, "end": v(-170.21, -7.8) * mm});
            skLineSegment(sketch, "E786", {"start": v(-170.21, -7.8) * mm, "end": v(-170.21, -7) * mm});
            skLineSegment(sketch, "E787", {"start": v(-170.21, -7) * mm, "end": v(-169.21, -7) * mm});
            skLineSegment(sketch, "E788", {"start": v(-169.21, -7) * mm, "end": v(-169.21, 7) * mm});
            skLineSegment(sketch, "E789", {"start": v(-169.21, 7) * mm, "end": v(-170.21, 7) * mm});
            skLineSegment(sketch, "E790", {"start": v(-170.21, 7) * mm, "end": v(-170.21, 7.8) * mm});
            skLineSegment(sketch, "E791", {"start": v(-170.21, 7.8) * mm, "end": v(-173.31, 7.8) * mm});
            skLineSegment(sketch, "E792", {"start": v(-173.31, 7.8) * mm, "end": v(-173.31, 7) * mm});
            skLineSegment(sketch, "E793", {"start": v(-173.31, 7) * mm, "end": v(-173.91, 7) * mm});
            skLineSegment(sketch, "E794", {"start": v(-173.91, 7) * mm, "end": v(-173.91, 8.58) * mm});
            skLineSegment(sketch, "E795", {"start": v(-173.91, 8.58) * mm, "end": v(-170.68, 8.58) * mm});
            skLineSegment(sketch, "E796", {"start": v(-170.68, 8.58) * mm, "end": v(-170.68, 10.25) * mm});
            skLineSegment(sketch, "E797", {"start": v(-170.68, 10.25) * mm, "end": v(-169.76, 10.25) * mm});
            skLineSegment(sketch, "E798", {"start": v(-169.76, 10.25) * mm, "end": v(-169.76, 13.55) * mm});
            skLineSegment(sketch, "E799", {"start": v(-169.76, 13.55) * mm, "end": v(-170.68, 13.55) * mm});
            skLineSegment(sketch, "E800", {"start": v(-170.68, 13.55) * mm, "end": v(-170.68, 15.23) * mm});
            skLineSegment(sketch, "E801", {"start": v(-170.68, 15.23) * mm, "end": v(-173.91, 15.23) * mm});
            skLineSegment(sketch, "E802", {"start": v(-173.91, 15.23) * mm, "end": v(-173.91, 16.1) * mm});
            skLineSegment(sketch, "E803", {"start": v(-173.91, 16.1) * mm, "end": v(-176.71, 16.1) * mm});
            skLineSegment(sketch, "E804", {"start": v(-211.79, 7) * mm, "end": v(-211.79, 6) * mm});
            skLineSegment(sketch, "E805", {"start": v(-211.79, 6) * mm, "end": v(-212.59, 6) * mm});
            skLineSegment(sketch, "E806", {"start": v(-212.59, 6) * mm, "end": v(-212.59, 2.9) * mm});
            skLineSegment(sketch, "E807", {"start": v(-212.59, 2.9) * mm, "end": v(-211.79, 2.9) * mm});
            skLineSegment(sketch, "E808", {"start": v(-211.79, 2.9) * mm, "end": v(-211.79, -2.9) * mm});
            skLineSegment(sketch, "E809", {"start": v(-211.79, -2.9) * mm, "end": v(-212.59, -2.9) * mm});
            skLineSegment(sketch, "E810", {"start": v(-212.59, -2.9) * mm, "end": v(-212.59, -6) * mm});
            skLineSegment(sketch, "E811", {"start": v(-212.59, -6) * mm, "end": v(-211.79, -6) * mm});
            skLineSegment(sketch, "E812", {"start": v(-211.79, -6) * mm, "end": v(-211.79, -7) * mm});
            skLineSegment(sketch, "E813", {"start": v(-211.79, -7) * mm, "end": v(-197.79, -7) * mm});
            skLineSegment(sketch, "E814", {"start": v(-197.79, -7) * mm, "end": v(-197.79, -6) * mm});
            skLineSegment(sketch, "E815", {"start": v(-197.79, -6) * mm, "end": v(-197, -6) * mm});
            skLineSegment(sketch, "E816", {"start": v(-197, -6) * mm, "end": v(-197, -2.9) * mm});
            skLineSegment(sketch, "E817", {"start": v(-197, -2.9) * mm, "end": v(-197.79, -2.9) * mm});
            skLineSegment(sketch, "E818", {"start": v(-197.79, -2.9) * mm, "end": v(-197.79, 2.9) * mm});
            skLineSegment(sketch, "E819", {"start": v(-197.79, 2.9) * mm, "end": v(-197, 2.9) * mm});
            skLineSegment(sketch, "E820", {"start": v(-197, 2.9) * mm, "end": v(-197, 6) * mm});
            skLineSegment(sketch, "E821", {"start": v(-197, 6) * mm, "end": v(-197.79, 6) * mm});
            skLineSegment(sketch, "E822", {"start": v(-197.79, 6) * mm, "end": v(-197.79, 7) * mm});
            skLineSegment(sketch, "E823", {"start": v(-197.79, 7) * mm, "end": v(-211.79, 7) * mm});
            skLineSegment(sketch, "E824", {"start": v(-147.5, 16.53) * mm, "end": v(-147.5, 15.52) * mm});
            skLineSegment(sketch, "E825", {"start": v(-147.5, 15.52) * mm, "end": v(-148.3, 15.52) * mm});
            skLineSegment(sketch, "E826", {"start": v(-148.3, 15.52) * mm, "end": v(-148.3, 12.43) * mm});
            skLineSegment(sketch, "E827", {"start": v(-148.3, 12.43) * mm, "end": v(-147.5, 12.43) * mm});
            skLineSegment(sketch, "E828", {"start": v(-147.5, 12.43) * mm, "end": v(-147.5, 6.63) * mm});
            skLineSegment(sketch, "E829", {"start": v(-147.5, 6.63) * mm, "end": v(-148.3, 6.63) * mm});
            skLineSegment(sketch, "E830", {"start": v(-148.3, 6.63) * mm, "end": v(-148.3, 3.52) * mm});
            skLineSegment(sketch, "E831", {"start": v(-148.3, 3.52) * mm, "end": v(-147.5, 3.52) * mm});
            skLineSegment(sketch, "E832", {"start": v(-147.5, 3.52) * mm, "end": v(-147.5, 2.53) * mm});
            skLineSegment(sketch, "E833", {"start": v(-147.5, 2.53) * mm, "end": v(-133.5, 2.53) * mm});
            skLineSegment(sketch, "E834", {"start": v(-133.5, 2.53) * mm, "end": v(-133.5, 3.52) * mm});
            skLineSegment(sketch, "E835", {"start": v(-133.5, 3.52) * mm, "end": v(-132.7, 3.52) * mm});
            skLineSegment(sketch, "E836", {"start": v(-132.7, 3.52) * mm, "end": v(-132.7, 6.63) * mm});
            skLineSegment(sketch, "E837", {"start": v(-132.7, 6.63) * mm, "end": v(-133.5, 6.63) * mm});
            skLineSegment(sketch, "E838", {"start": v(-133.5, 6.63) * mm, "end": v(-133.5, 12.43) * mm});
            skLineSegment(sketch, "E839", {"start": v(-133.5, 12.43) * mm, "end": v(-132.7, 12.43) * mm});
            skLineSegment(sketch, "E840", {"start": v(-132.7, 12.43) * mm, "end": v(-132.7, 15.52) * mm});
            skLineSegment(sketch, "E841", {"start": v(-132.7, 15.52) * mm, "end": v(-133.5, 15.52) * mm});
            skLineSegment(sketch, "E842", {"start": v(-133.5, 15.52) * mm, "end": v(-133.5, 16.53) * mm});
            skLineSegment(sketch, "E843", {"start": v(-133.5, 16.53) * mm, "end": v(-147.5, 16.53) * mm});
            skLineSegment(sketch, "E844", {"start": v(-121.3, 16.53) * mm, "end": v(-121.3, 15.52) * mm});
            skLineSegment(sketch, "E845", {"start": v(-121.3, 15.52) * mm, "end": v(-122.1, 15.52) * mm});
            skLineSegment(sketch, "E846", {"start": v(-122.1, 15.52) * mm, "end": v(-122.1, 12.43) * mm});
            skLineSegment(sketch, "E847", {"start": v(-122.1, 12.43) * mm, "end": v(-121.3, 12.43) * mm});
            skLineSegment(sketch, "E848", {"start": v(-121.3, 12.43) * mm, "end": v(-121.3, 6.63) * mm});
            skLineSegment(sketch, "E849", {"start": v(-121.3, 6.63) * mm, "end": v(-122.1, 6.63) * mm});
            skLineSegment(sketch, "E850", {"start": v(-122.1, 6.63) * mm, "end": v(-122.1, 3.52) * mm});
            skLineSegment(sketch, "E851", {"start": v(-122.1, 3.52) * mm, "end": v(-121.3, 3.52) * mm});
            skLineSegment(sketch, "E852", {"start": v(-121.3, 3.52) * mm, "end": v(-121.3, 2.53) * mm});
            skLineSegment(sketch, "E853", {"start": v(-121.3, 2.53) * mm, "end": v(-107.3, 2.53) * mm});
            skLineSegment(sketch, "E854", {"start": v(-107.3, 2.53) * mm, "end": v(-107.3, 3.52) * mm});
            skLineSegment(sketch, "E855", {"start": v(-107.3, 3.52) * mm, "end": v(-106.5, 3.52) * mm});
            skLineSegment(sketch, "E856", {"start": v(-106.5, 3.52) * mm, "end": v(-106.5, 6.63) * mm});
            skLineSegment(sketch, "E857", {"start": v(-106.5, 6.63) * mm, "end": v(-107.3, 6.63) * mm});
            skLineSegment(sketch, "E858", {"start": v(-107.3, 6.63) * mm, "end": v(-107.3, 12.43) * mm});
            skLineSegment(sketch, "E859", {"start": v(-107.3, 12.43) * mm, "end": v(-106.5, 12.43) * mm});
            skLineSegment(sketch, "E860", {"start": v(-106.5, 12.43) * mm, "end": v(-106.5, 15.52) * mm});
            skLineSegment(sketch, "E861", {"start": v(-106.5, 15.52) * mm, "end": v(-107.3, 15.52) * mm});
            skLineSegment(sketch, "E862", {"start": v(-107.3, 15.52) * mm, "end": v(-107.3, 16.53) * mm});
            skLineSegment(sketch, "E863", {"start": v(-107.3, 16.53) * mm, "end": v(-121.3, 16.53) * mm});
            skLineSegment(sketch, "E864", {"start": v(-102.25, 16.53) * mm, "end": v(-102.25, 15.52) * mm});
            skLineSegment(sketch, "E865", {"start": v(-102.25, 15.52) * mm, "end": v(-103.05, 15.52) * mm});
            skLineSegment(sketch, "E866", {"start": v(-103.05, 15.52) * mm, "end": v(-103.05, 12.43) * mm});
            skLineSegment(sketch, "E867", {"start": v(-103.05, 12.43) * mm, "end": v(-102.25, 12.43) * mm});
            skLineSegment(sketch, "E868", {"start": v(-102.25, 12.43) * mm, "end": v(-102.25, 6.63) * mm});
            skLineSegment(sketch, "E869", {"start": v(-102.25, 6.63) * mm, "end": v(-103.05, 6.63) * mm});
            skLineSegment(sketch, "E870", {"start": v(-103.05, 6.63) * mm, "end": v(-103.05, 3.52) * mm});
            skLineSegment(sketch, "E871", {"start": v(-103.05, 3.52) * mm, "end": v(-102.25, 3.52) * mm});
            skLineSegment(sketch, "E872", {"start": v(-102.25, 3.52) * mm, "end": v(-102.25, 2.53) * mm});
            skLineSegment(sketch, "E873", {"start": v(-102.25, 2.53) * mm, "end": v(-88.25, 2.53) * mm});
            skLineSegment(sketch, "E874", {"start": v(-88.25, 2.53) * mm, "end": v(-88.25, 3.52) * mm});
            skLineSegment(sketch, "E875", {"start": v(-88.25, 3.52) * mm, "end": v(-87.45, 3.52) * mm});
            skLineSegment(sketch, "E876", {"start": v(-87.45, 3.52) * mm, "end": v(-87.45, 6.63) * mm});
            skLineSegment(sketch, "E877", {"start": v(-87.45, 6.63) * mm, "end": v(-88.25, 6.63) * mm});
            skLineSegment(sketch, "E878", {"start": v(-88.25, 6.63) * mm, "end": v(-88.25, 12.43) * mm});
            skLineSegment(sketch, "E879", {"start": v(-88.25, 12.43) * mm, "end": v(-87.45, 12.43) * mm});
            skLineSegment(sketch, "E880", {"start": v(-87.45, 12.43) * mm, "end": v(-87.45, 15.52) * mm});
            skLineSegment(sketch, "E881", {"start": v(-87.45, 15.52) * mm, "end": v(-88.25, 15.52) * mm});
            skLineSegment(sketch, "E882", {"start": v(-88.25, 15.52) * mm, "end": v(-88.25, 16.53) * mm});
            skLineSegment(sketch, "E883", {"start": v(-88.25, 16.53) * mm, "end": v(-102.25, 16.53) * mm});
            skLineSegment(sketch, "E884", {"start": v(-83.2, 16.53) * mm, "end": v(-83.2, 15.52) * mm});
            skLineSegment(sketch, "E885", {"start": v(-83.2, 15.52) * mm, "end": v(-84, 15.52) * mm});
            skLineSegment(sketch, "E886", {"start": v(-84, 15.52) * mm, "end": v(-84, 12.43) * mm});
            skLineSegment(sketch, "E887", {"start": v(-84, 12.43) * mm, "end": v(-83.2, 12.43) * mm});
            skLineSegment(sketch, "E888", {"start": v(-83.2, 12.43) * mm, "end": v(-83.2, 6.63) * mm});
            skLineSegment(sketch, "E889", {"start": v(-83.2, 6.63) * mm, "end": v(-84, 6.63) * mm});
            skLineSegment(sketch, "E890", {"start": v(-84, 6.63) * mm, "end": v(-84, 3.52) * mm});
            skLineSegment(sketch, "E891", {"start": v(-84, 3.52) * mm, "end": v(-83.2, 3.52) * mm});
            skLineSegment(sketch, "E892", {"start": v(-83.2, 3.52) * mm, "end": v(-83.2, 2.53) * mm});
            skLineSegment(sketch, "E893", {"start": v(-83.2, 2.53) * mm, "end": v(-69.2, 2.53) * mm});
            skLineSegment(sketch, "E894", {"start": v(-69.2, 2.53) * mm, "end": v(-69.2, 3.52) * mm});
            skLineSegment(sketch, "E895", {"start": v(-69.2, 3.52) * mm, "end": v(-68.4, 3.52) * mm});
            skLineSegment(sketch, "E896", {"start": v(-68.4, 3.52) * mm, "end": v(-68.4, 6.63) * mm});
            skLineSegment(sketch, "E897", {"start": v(-68.4, 6.63) * mm, "end": v(-69.2, 6.63) * mm});
            skLineSegment(sketch, "E898", {"start": v(-69.2, 6.63) * mm, "end": v(-69.2, 12.43) * mm});
            skLineSegment(sketch, "E899", {"start": v(-69.2, 12.43) * mm, "end": v(-68.4, 12.43) * mm});
            skLineSegment(sketch, "E900", {"start": v(-68.4, 12.43) * mm, "end": v(-68.4, 15.52) * mm});
            skLineSegment(sketch, "E901", {"start": v(-68.4, 15.52) * mm, "end": v(-69.2, 15.52) * mm});
            skLineSegment(sketch, "E902", {"start": v(-69.2, 15.52) * mm, "end": v(-69.2, 16.53) * mm});
            skLineSegment(sketch, "E903", {"start": v(-69.2, 16.53) * mm, "end": v(-83.2, 16.53) * mm});
            skLineSegment(sketch, "E904", {"start": v(-64.15, 16.53) * mm, "end": v(-64.15, 15.52) * mm});
            skLineSegment(sketch, "E905", {"start": v(-64.15, 15.52) * mm, "end": v(-64.95, 15.52) * mm});
            skLineSegment(sketch, "E906", {"start": v(-64.95, 15.52) * mm, "end": v(-64.95, 12.43) * mm});
            skLineSegment(sketch, "E907", {"start": v(-64.95, 12.43) * mm, "end": v(-64.15, 12.43) * mm});
            skLineSegment(sketch, "E908", {"start": v(-64.15, 12.43) * mm, "end": v(-64.15, 6.63) * mm});
            skLineSegment(sketch, "E909", {"start": v(-64.15, 6.63) * mm, "end": v(-64.95, 6.63) * mm});
            skLineSegment(sketch, "E910", {"start": v(-64.95, 6.63) * mm, "end": v(-64.95, 3.52) * mm});
            skLineSegment(sketch, "E911", {"start": v(-64.95, 3.52) * mm, "end": v(-64.15, 3.52) * mm});
            skLineSegment(sketch, "E912", {"start": v(-64.15, 3.52) * mm, "end": v(-64.15, 2.53) * mm});
            skLineSegment(sketch, "E913", {"start": v(-64.15, 2.53) * mm, "end": v(-50.15, 2.53) * mm});
            skLineSegment(sketch, "E914", {"start": v(-50.15, 2.53) * mm, "end": v(-50.15, 3.52) * mm});
            skLineSegment(sketch, "E915", {"start": v(-50.15, 3.52) * mm, "end": v(-49.35, 3.52) * mm});
            skLineSegment(sketch, "E916", {"start": v(-49.35, 3.52) * mm, "end": v(-49.35, 6.63) * mm});
            skLineSegment(sketch, "E917", {"start": v(-49.35, 6.63) * mm, "end": v(-50.15, 6.63) * mm});
            skLineSegment(sketch, "E918", {"start": v(-50.15, 6.63) * mm, "end": v(-50.15, 12.43) * mm});
            skLineSegment(sketch, "E919", {"start": v(-50.15, 12.43) * mm, "end": v(-49.35, 12.43) * mm});
            skLineSegment(sketch, "E920", {"start": v(-49.35, 12.43) * mm, "end": v(-49.35, 15.52) * mm});
            skLineSegment(sketch, "E921", {"start": v(-49.35, 15.52) * mm, "end": v(-50.15, 15.52) * mm});
            skLineSegment(sketch, "E922", {"start": v(-50.15, 15.52) * mm, "end": v(-50.15, 16.53) * mm});
            skLineSegment(sketch, "E923", {"start": v(-50.15, 16.53) * mm, "end": v(-64.15, 16.53) * mm});
            skLineSegment(sketch, "E924", {"start": v(-45.1, 16.53) * mm, "end": v(-45.1, 15.52) * mm});
            skLineSegment(sketch, "E925", {"start": v(-45.1, 15.52) * mm, "end": v(-45.9, 15.52) * mm});
            skLineSegment(sketch, "E926", {"start": v(-45.9, 15.52) * mm, "end": v(-45.9, 12.43) * mm});
            skLineSegment(sketch, "E927", {"start": v(-45.9, 12.43) * mm, "end": v(-45.1, 12.43) * mm});
            skLineSegment(sketch, "E928", {"start": v(-45.1, 12.43) * mm, "end": v(-45.1, 6.63) * mm});
            skLineSegment(sketch, "E929", {"start": v(-45.1, 6.63) * mm, "end": v(-45.9, 6.63) * mm});
            skLineSegment(sketch, "E930", {"start": v(-45.9, 6.63) * mm, "end": v(-45.9, 3.52) * mm});
            skLineSegment(sketch, "E931", {"start": v(-45.9, 3.52) * mm, "end": v(-45.1, 3.52) * mm});
            skLineSegment(sketch, "E932", {"start": v(-45.1, 3.52) * mm, "end": v(-45.1, 2.53) * mm});
            skLineSegment(sketch, "E933", {"start": v(-45.1, 2.53) * mm, "end": v(-31.1, 2.53) * mm});
            skLineSegment(sketch, "E934", {"start": v(-31.1, 2.53) * mm, "end": v(-31.1, 3.52) * mm});
            skLineSegment(sketch, "E935", {"start": v(-31.1, 3.52) * mm, "end": v(-30.3, 3.52) * mm});
            skLineSegment(sketch, "E936", {"start": v(-30.3, 3.52) * mm, "end": v(-30.3, 6.63) * mm});
            skLineSegment(sketch, "E937", {"start": v(-30.3, 6.63) * mm, "end": v(-31.1, 6.63) * mm});
            skLineSegment(sketch, "E938", {"start": v(-31.1, 6.63) * mm, "end": v(-31.1, 12.43) * mm});
            skLineSegment(sketch, "E939", {"start": v(-31.1, 12.43) * mm, "end": v(-30.3, 12.43) * mm});
            skLineSegment(sketch, "E940", {"start": v(-30.3, 12.43) * mm, "end": v(-30.3, 15.52) * mm});
            skLineSegment(sketch, "E941", {"start": v(-30.3, 15.52) * mm, "end": v(-31.1, 15.52) * mm});
            skLineSegment(sketch, "E942", {"start": v(-31.1, 15.52) * mm, "end": v(-31.1, 16.53) * mm});
            skLineSegment(sketch, "E943", {"start": v(-31.1, 16.53) * mm, "end": v(-45.1, 16.53) * mm});
            skLineSegment(sketch, "E944", {"start": v(-26.05, 16.53) * mm, "end": v(-26.05, 15.52) * mm});
            skLineSegment(sketch, "E945", {"start": v(-26.05, 15.52) * mm, "end": v(-26.85, 15.52) * mm});
            skLineSegment(sketch, "E946", {"start": v(-26.85, 15.52) * mm, "end": v(-26.85, 12.43) * mm});
            skLineSegment(sketch, "E947", {"start": v(-26.85, 12.43) * mm, "end": v(-26.05, 12.43) * mm});
            skLineSegment(sketch, "E948", {"start": v(-26.05, 12.43) * mm, "end": v(-26.05, 6.63) * mm});
            skLineSegment(sketch, "E949", {"start": v(-26.05, 6.63) * mm, "end": v(-26.85, 6.63) * mm});
            skLineSegment(sketch, "E950", {"start": v(-26.85, 6.63) * mm, "end": v(-26.85, 3.52) * mm});
            skLineSegment(sketch, "E951", {"start": v(-26.85, 3.52) * mm, "end": v(-26.05, 3.52) * mm});
            skLineSegment(sketch, "E952", {"start": v(-26.05, 3.52) * mm, "end": v(-26.05, 2.53) * mm});
            skLineSegment(sketch, "E953", {"start": v(-26.05, 2.53) * mm, "end": v(-12.05, 2.53) * mm});
            skLineSegment(sketch, "E954", {"start": v(-12.05, 2.53) * mm, "end": v(-12.05, 3.52) * mm});
            skLineSegment(sketch, "E955", {"start": v(-12.05, 3.52) * mm, "end": v(-11.25, 3.52) * mm});
            skLineSegment(sketch, "E956", {"start": v(-11.25, 3.52) * mm, "end": v(-11.25, 6.63) * mm});
            skLineSegment(sketch, "E957", {"start": v(-11.25, 6.63) * mm, "end": v(-12.05, 6.63) * mm});
            skLineSegment(sketch, "E958", {"start": v(-12.05, 6.63) * mm, "end": v(-12.05, 12.43) * mm});
            skLineSegment(sketch, "E959", {"start": v(-12.05, 12.43) * mm, "end": v(-11.25, 12.43) * mm});
            skLineSegment(sketch, "E960", {"start": v(-11.25, 12.43) * mm, "end": v(-11.25, 15.52) * mm});
            skLineSegment(sketch, "E961", {"start": v(-11.25, 15.52) * mm, "end": v(-12.05, 15.52) * mm});
            skLineSegment(sketch, "E962", {"start": v(-12.05, 15.52) * mm, "end": v(-12.05, 16.53) * mm});
            skLineSegment(sketch, "E963", {"start": v(-12.05, 16.53) * mm, "end": v(-26.05, 16.53) * mm});
            skLineSegment(sketch, "E964", {"start": v(-7, 16.53) * mm, "end": v(-7, 15.52) * mm});
            skLineSegment(sketch, "E965", {"start": v(-7, 15.52) * mm, "end": v(-7.8, 15.52) * mm});
            skLineSegment(sketch, "E966", {"start": v(-7.8, 15.52) * mm, "end": v(-7.8, 12.43) * mm});
            skLineSegment(sketch, "E967", {"start": v(-7.8, 12.43) * mm, "end": v(-7, 12.43) * mm});
            skLineSegment(sketch, "E968", {"start": v(-7, 12.43) * mm, "end": v(-7, 6.63) * mm});
            skLineSegment(sketch, "E969", {"start": v(-7, 6.63) * mm, "end": v(-7.8, 6.63) * mm});
            skLineSegment(sketch, "E970", {"start": v(-7.8, 6.63) * mm, "end": v(-7.8, 3.52) * mm});
            skLineSegment(sketch, "E971", {"start": v(-7.8, 3.52) * mm, "end": v(-7, 3.52) * mm});
            skLineSegment(sketch, "E972", {"start": v(-7, 3.52) * mm, "end": v(-7, 2.53) * mm});
            skLineSegment(sketch, "E973", {"start": v(-7, 2.53) * mm, "end": v(7, 2.53) * mm});
            skLineSegment(sketch, "E974", {"start": v(7, 2.53) * mm, "end": v(7, 3.52) * mm});
            skLineSegment(sketch, "E975", {"start": v(7, 3.52) * mm, "end": v(7.8, 3.52) * mm});
            skLineSegment(sketch, "E976", {"start": v(7.8, 3.52) * mm, "end": v(7.8, 6.63) * mm});
            skLineSegment(sketch, "E977", {"start": v(7.8, 6.63) * mm, "end": v(7, 6.63) * mm});
            skLineSegment(sketch, "E978", {"start": v(7, 6.63) * mm, "end": v(7, 12.43) * mm});
            skLineSegment(sketch, "E979", {"start": v(7, 12.43) * mm, "end": v(7.8, 12.43) * mm});
            skLineSegment(sketch, "E980", {"start": v(7.8, 12.43) * mm, "end": v(7.8, 15.52) * mm});
            skLineSegment(sketch, "E981", {"start": v(7.8, 15.52) * mm, "end": v(7, 15.52) * mm});
            skLineSegment(sketch, "E982", {"start": v(7, 15.52) * mm, "end": v(7, 16.53) * mm});
            skLineSegment(sketch, "E983", {"start": v(7, 16.53) * mm, "end": v(-7, 16.53) * mm});
            skLineSegment(sketch, "E984", {"start": v(12.05, 16.53) * mm, "end": v(12.05, 15.52) * mm});
            skLineSegment(sketch, "E985", {"start": v(12.05, 15.52) * mm, "end": v(11.25, 15.52) * mm});
            skLineSegment(sketch, "E986", {"start": v(11.25, 15.52) * mm, "end": v(11.25, 12.43) * mm});
            skLineSegment(sketch, "E987", {"start": v(11.25, 12.43) * mm, "end": v(12.05, 12.43) * mm});
            skLineSegment(sketch, "E988", {"start": v(12.05, 12.43) * mm, "end": v(12.05, 6.63) * mm});
            skLineSegment(sketch, "E989", {"start": v(12.05, 6.63) * mm, "end": v(11.25, 6.63) * mm});
            skLineSegment(sketch, "E990", {"start": v(11.25, 6.63) * mm, "end": v(11.25, 3.52) * mm});
            skLineSegment(sketch, "E991", {"start": v(11.25, 3.52) * mm, "end": v(12.05, 3.52) * mm});
            skLineSegment(sketch, "E992", {"start": v(12.05, 3.52) * mm, "end": v(12.05, 2.53) * mm});
            skLineSegment(sketch, "E993", {"start": v(12.05, 2.53) * mm, "end": v(26.05, 2.53) * mm});
            skLineSegment(sketch, "E994", {"start": v(26.05, 2.53) * mm, "end": v(26.05, 3.52) * mm});
            skLineSegment(sketch, "E995", {"start": v(26.05, 3.52) * mm, "end": v(26.85, 3.52) * mm});
            skLineSegment(sketch, "E996", {"start": v(26.85, 3.52) * mm, "end": v(26.85, 6.63) * mm});
            skLineSegment(sketch, "E997", {"start": v(26.85, 6.63) * mm, "end": v(26.05, 6.63) * mm});
            skLineSegment(sketch, "E998", {"start": v(26.05, 6.63) * mm, "end": v(26.05, 12.43) * mm});
            skLineSegment(sketch, "E999", {"start": v(26.05, 12.43) * mm, "end": v(26.85, 12.43) * mm});
            skLineSegment(sketch, "E1000", {"start": v(26.85, 12.43) * mm, "end": v(26.85, 15.52) * mm});
            skLineSegment(sketch, "E1001", {"start": v(26.85, 15.52) * mm, "end": v(26.05, 15.52) * mm});
            skLineSegment(sketch, "E1002", {"start": v(26.05, 15.52) * mm, "end": v(26.05, 16.53) * mm});
            skLineSegment(sketch, "E1003", {"start": v(26.05, 16.53) * mm, "end": v(12.05, 16.53) * mm});
            skLineSegment(sketch, "E1004", {"start": v(31.1, 16.53) * mm, "end": v(31.1, 15.52) * mm});
            skLineSegment(sketch, "E1005", {"start": v(31.1, 15.52) * mm, "end": v(30.3, 15.52) * mm});
            skLineSegment(sketch, "E1006", {"start": v(30.3, 15.52) * mm, "end": v(30.3, 12.43) * mm});
            skLineSegment(sketch, "E1007", {"start": v(30.3, 12.43) * mm, "end": v(31.1, 12.43) * mm});
            skLineSegment(sketch, "E1008", {"start": v(31.1, 12.43) * mm, "end": v(31.1, 6.63) * mm});
            skLineSegment(sketch, "E1009", {"start": v(31.1, 6.63) * mm, "end": v(30.3, 6.63) * mm});
            skLineSegment(sketch, "E1010", {"start": v(30.3, 6.63) * mm, "end": v(30.3, 3.52) * mm});
            skLineSegment(sketch, "E1011", {"start": v(30.3, 3.52) * mm, "end": v(31.1, 3.52) * mm});
            skLineSegment(sketch, "E1012", {"start": v(31.1, 3.52) * mm, "end": v(31.1, 2.53) * mm});
            skLineSegment(sketch, "E1013", {"start": v(31.1, 2.53) * mm, "end": v(45.1, 2.53) * mm});
            skLineSegment(sketch, "E1014", {"start": v(45.1, 2.53) * mm, "end": v(45.1, 3.52) * mm});
            skLineSegment(sketch, "E1015", {"start": v(45.1, 3.52) * mm, "end": v(45.9, 3.52) * mm});
            skLineSegment(sketch, "E1016", {"start": v(45.9, 3.52) * mm, "end": v(45.9, 6.63) * mm});
            skLineSegment(sketch, "E1017", {"start": v(45.9, 6.63) * mm, "end": v(45.1, 6.63) * mm});
            skLineSegment(sketch, "E1018", {"start": v(45.1, 6.63) * mm, "end": v(45.1, 12.43) * mm});
            skLineSegment(sketch, "E1019", {"start": v(45.1, 12.43) * mm, "end": v(45.9, 12.43) * mm});
            skLineSegment(sketch, "E1020", {"start": v(45.9, 12.43) * mm, "end": v(45.9, 15.52) * mm});
            skLineSegment(sketch, "E1021", {"start": v(45.9, 15.52) * mm, "end": v(45.1, 15.52) * mm});
            skLineSegment(sketch, "E1022", {"start": v(45.1, 15.52) * mm, "end": v(45.1, 16.53) * mm});
            skLineSegment(sketch, "E1023", {"start": v(45.1, 16.53) * mm, "end": v(31.1, 16.53) * mm});
            skLineSegment(sketch, "E1024", {"start": v(140.64, 16.53) * mm, "end": v(140.64, 15.52) * mm});
            skLineSegment(sketch, "E1025", {"start": v(140.64, 15.52) * mm, "end": v(139.84, 15.52) * mm});
            skLineSegment(sketch, "E1026", {"start": v(139.84, 15.52) * mm, "end": v(139.84, 12.43) * mm});
            skLineSegment(sketch, "E1027", {"start": v(139.84, 12.43) * mm, "end": v(140.64, 12.43) * mm});
            skLineSegment(sketch, "E1028", {"start": v(140.64, 12.43) * mm, "end": v(140.64, 6.63) * mm});
            skLineSegment(sketch, "E1029", {"start": v(140.64, 6.63) * mm, "end": v(139.84, 6.63) * mm});
            skLineSegment(sketch, "E1030", {"start": v(139.84, 6.63) * mm, "end": v(139.84, 3.52) * mm});
            skLineSegment(sketch, "E1031", {"start": v(139.84, 3.52) * mm, "end": v(140.64, 3.52) * mm});
            skLineSegment(sketch, "E1032", {"start": v(140.64, 3.52) * mm, "end": v(140.64, 2.53) * mm});
            skLineSegment(sketch, "E1033", {"start": v(140.64, 2.53) * mm, "end": v(154.64, 2.53) * mm});
            skLineSegment(sketch, "E1034", {"start": v(154.64, 2.53) * mm, "end": v(154.64, 3.52) * mm});
            skLineSegment(sketch, "E1035", {"start": v(154.64, 3.52) * mm, "end": v(155.44, 3.52) * mm});
            skLineSegment(sketch, "E1036", {"start": v(155.44, 3.52) * mm, "end": v(155.44, 6.63) * mm});
            skLineSegment(sketch, "E1037", {"start": v(155.44, 6.63) * mm, "end": v(154.64, 6.63) * mm});
            skLineSegment(sketch, "E1038", {"start": v(154.64, 6.63) * mm, "end": v(154.64, 12.43) * mm});
            skLineSegment(sketch, "E1039", {"start": v(154.64, 12.43) * mm, "end": v(155.44, 12.43) * mm});
            skLineSegment(sketch, "E1040", {"start": v(155.44, 12.43) * mm, "end": v(155.44, 15.52) * mm});
            skLineSegment(sketch, "E1041", {"start": v(155.44, 15.52) * mm, "end": v(154.64, 15.52) * mm});
            skLineSegment(sketch, "E1042", {"start": v(154.64, 15.52) * mm, "end": v(154.64, 16.53) * mm});
            skLineSegment(sketch, "E1043", {"start": v(154.64, 16.53) * mm, "end": v(140.64, 16.53) * mm});
            skLineSegment(sketch, "E1044", {"start": v(159.69, 16.53) * mm, "end": v(159.69, 15.52) * mm});
            skLineSegment(sketch, "E1045", {"start": v(159.69, 15.52) * mm, "end": v(158.89, 15.52) * mm});
            skLineSegment(sketch, "E1046", {"start": v(158.89, 15.52) * mm, "end": v(158.89, 12.43) * mm});
            skLineSegment(sketch, "E1047", {"start": v(158.89, 12.43) * mm, "end": v(159.69, 12.43) * mm});
            skLineSegment(sketch, "E1048", {"start": v(159.69, 12.43) * mm, "end": v(159.69, 6.63) * mm});
            skLineSegment(sketch, "E1049", {"start": v(159.69, 6.63) * mm, "end": v(158.89, 6.63) * mm});
            skLineSegment(sketch, "E1050", {"start": v(158.89, 6.63) * mm, "end": v(158.89, 3.52) * mm});
            skLineSegment(sketch, "E1051", {"start": v(158.89, 3.52) * mm, "end": v(159.69, 3.52) * mm});
            skLineSegment(sketch, "E1052", {"start": v(159.69, 3.52) * mm, "end": v(159.69, 2.53) * mm});
            skLineSegment(sketch, "E1053", {"start": v(159.69, 2.53) * mm, "end": v(173.69, 2.53) * mm});
            skLineSegment(sketch, "E1054", {"start": v(173.69, 2.53) * mm, "end": v(173.69, 3.52) * mm});
            skLineSegment(sketch, "E1055", {"start": v(173.69, 3.52) * mm, "end": v(174.49, 3.52) * mm});
            skLineSegment(sketch, "E1056", {"start": v(174.49, 3.52) * mm, "end": v(174.49, 6.63) * mm});
            skLineSegment(sketch, "E1057", {"start": v(174.49, 6.63) * mm, "end": v(173.69, 6.63) * mm});
            skLineSegment(sketch, "E1058", {"start": v(173.69, 6.63) * mm, "end": v(173.69, 12.43) * mm});
            skLineSegment(sketch, "E1059", {"start": v(173.69, 12.43) * mm, "end": v(174.49, 12.43) * mm});
            skLineSegment(sketch, "E1060", {"start": v(174.49, 12.43) * mm, "end": v(174.49, 15.52) * mm});
            skLineSegment(sketch, "E1061", {"start": v(174.49, 15.52) * mm, "end": v(173.69, 15.52) * mm});
            skLineSegment(sketch, "E1062", {"start": v(173.69, 15.52) * mm, "end": v(173.69, 16.53) * mm});
            skLineSegment(sketch, "E1063", {"start": v(173.69, 16.53) * mm, "end": v(159.69, 16.53) * mm});
            skLineSegment(sketch, "E1064", {"start": v(178.74, 16.53) * mm, "end": v(178.74, 15.52) * mm});
            skLineSegment(sketch, "E1065", {"start": v(178.74, 15.52) * mm, "end": v(177.94, 15.52) * mm});
            skLineSegment(sketch, "E1066", {"start": v(177.94, 15.52) * mm, "end": v(177.94, 12.43) * mm});
            skLineSegment(sketch, "E1067", {"start": v(177.94, 12.43) * mm, "end": v(178.74, 12.43) * mm});
            skLineSegment(sketch, "E1068", {"start": v(178.74, 12.43) * mm, "end": v(178.74, 6.63) * mm});
            skLineSegment(sketch, "E1069", {"start": v(178.74, 6.63) * mm, "end": v(177.94, 6.63) * mm});
            skLineSegment(sketch, "E1070", {"start": v(177.94, 6.63) * mm, "end": v(177.94, 3.52) * mm});
            skLineSegment(sketch, "E1071", {"start": v(177.94, 3.52) * mm, "end": v(178.74, 3.52) * mm});
            skLineSegment(sketch, "E1072", {"start": v(178.74, 3.52) * mm, "end": v(178.74, 2.53) * mm});
            skLineSegment(sketch, "E1073", {"start": v(178.74, 2.53) * mm, "end": v(192.74, 2.53) * mm});
            skLineSegment(sketch, "E1074", {"start": v(192.74, 2.53) * mm, "end": v(192.74, 3.52) * mm});
            skLineSegment(sketch, "E1075", {"start": v(192.74, 3.52) * mm, "end": v(193.54, 3.52) * mm});
            skLineSegment(sketch, "E1076", {"start": v(193.54, 3.52) * mm, "end": v(193.54, 6.63) * mm});
            skLineSegment(sketch, "E1077", {"start": v(193.54, 6.63) * mm, "end": v(192.74, 6.63) * mm});
            skLineSegment(sketch, "E1078", {"start": v(192.74, 6.63) * mm, "end": v(192.74, 12.43) * mm});
            skLineSegment(sketch, "E1079", {"start": v(192.74, 12.43) * mm, "end": v(193.54, 12.43) * mm});
            skLineSegment(sketch, "E1080", {"start": v(193.54, 12.43) * mm, "end": v(193.54, 15.52) * mm});
            skLineSegment(sketch, "E1081", {"start": v(193.54, 15.52) * mm, "end": v(192.74, 15.52) * mm});
            skLineSegment(sketch, "E1082", {"start": v(192.74, 15.52) * mm, "end": v(192.74, 16.53) * mm});
            skLineSegment(sketch, "E1083", {"start": v(192.74, 16.53) * mm, "end": v(178.74, 16.53) * mm});
            skLineSegment(sketch, "E1084", {"start": v(197.79, 16.53) * mm, "end": v(197.79, 15.52) * mm});
            skLineSegment(sketch, "E1085", {"start": v(197.79, 15.52) * mm, "end": v(196.99, 15.52) * mm});
            skLineSegment(sketch, "E1086", {"start": v(196.99, 15.52) * mm, "end": v(196.99, 12.43) * mm});
            skLineSegment(sketch, "E1087", {"start": v(196.99, 12.43) * mm, "end": v(197.79, 12.43) * mm});
            skLineSegment(sketch, "E1088", {"start": v(197.79, 12.43) * mm, "end": v(197.79, 6.63) * mm});
            skLineSegment(sketch, "E1089", {"start": v(197.79, 6.63) * mm, "end": v(196.99, 6.63) * mm});
            skLineSegment(sketch, "E1090", {"start": v(196.99, 6.63) * mm, "end": v(196.99, 3.52) * mm});
            skLineSegment(sketch, "E1091", {"start": v(196.99, 3.52) * mm, "end": v(197.79, 3.52) * mm});
            skLineSegment(sketch, "E1092", {"start": v(197.79, 3.52) * mm, "end": v(197.79, 2.53) * mm});
            skLineSegment(sketch, "E1093", {"start": v(197.79, 2.53) * mm, "end": v(211.79, 2.53) * mm});
            skLineSegment(sketch, "E1094", {"start": v(211.79, 2.53) * mm, "end": v(211.79, 3.52) * mm});
            skLineSegment(sketch, "E1095", {"start": v(211.79, 3.52) * mm, "end": v(212.59, 3.52) * mm});
            skLineSegment(sketch, "E1096", {"start": v(212.59, 3.52) * mm, "end": v(212.59, 6.63) * mm});
            skLineSegment(sketch, "E1097", {"start": v(212.59, 6.63) * mm, "end": v(211.79, 6.63) * mm});
            skLineSegment(sketch, "E1098", {"start": v(211.79, 6.63) * mm, "end": v(211.79, 12.43) * mm});
            skLineSegment(sketch, "E1099", {"start": v(211.79, 12.43) * mm, "end": v(212.59, 12.43) * mm});
            skLineSegment(sketch, "E1100", {"start": v(212.59, 12.43) * mm, "end": v(212.59, 15.52) * mm});
            skLineSegment(sketch, "E1101", {"start": v(212.59, 15.52) * mm, "end": v(211.79, 15.52) * mm});
            skLineSegment(sketch, "E1102", {"start": v(211.79, 15.52) * mm, "end": v(211.79, 16.53) * mm});
            skLineSegment(sketch, "E1103", {"start": v(211.79, 16.53) * mm, "end": v(197.79, 16.53) * mm});
            skLineSegment(sketch, "E1104", {"start": v(-211.79, 35.58) * mm, "end": v(-211.79, 34.57) * mm});
            skLineSegment(sketch, "E1105", {"start": v(-211.79, 34.57) * mm, "end": v(-212.59, 34.57) * mm});
            skLineSegment(sketch, "E1106", {"start": v(-212.59, 34.57) * mm, "end": v(-212.59, 31.48) * mm});
            skLineSegment(sketch, "E1107", {"start": v(-212.59, 31.48) * mm, "end": v(-211.79, 31.48) * mm});
            skLineSegment(sketch, "E1108", {"start": v(-211.79, 31.48) * mm, "end": v(-211.79, 25.68) * mm});
            skLineSegment(sketch, "E1109", {"start": v(-211.79, 25.68) * mm, "end": v(-212.59, 25.68) * mm});
            skLineSegment(sketch, "E1110", {"start": v(-212.59, 25.68) * mm, "end": v(-212.59, 22.57) * mm});
            skLineSegment(sketch, "E1111", {"start": v(-212.59, 22.57) * mm, "end": v(-211.79, 22.57) * mm});
            skLineSegment(sketch, "E1112", {"start": v(-211.79, 22.57) * mm, "end": v(-211.79, 21.58) * mm});
            skLineSegment(sketch, "E1113", {"start": v(-211.79, 21.58) * mm, "end": v(-197.79, 21.58) * mm});
            skLineSegment(sketch, "E1114", {"start": v(-197.79, 21.58) * mm, "end": v(-197.79, 22.57) * mm});
            skLineSegment(sketch, "E1115", {"start": v(-197.79, 22.57) * mm, "end": v(-197, 22.57) * mm});
            skLineSegment(sketch, "E1116", {"start": v(-197, 22.57) * mm, "end": v(-197, 25.68) * mm});
            skLineSegment(sketch, "E1117", {"start": v(-197, 25.68) * mm, "end": v(-197.79, 25.68) * mm});
            skLineSegment(sketch, "E1118", {"start": v(-197.79, 25.68) * mm, "end": v(-197.79, 31.48) * mm});
            skLineSegment(sketch, "E1119", {"start": v(-197.79, 31.48) * mm, "end": v(-197, 31.48) * mm});
            skLineSegment(sketch, "E1120", {"start": v(-197, 31.48) * mm, "end": v(-197, 34.57) * mm});
            skLineSegment(sketch, "E1121", {"start": v(-197, 34.57) * mm, "end": v(-197.79, 34.57) * mm});
            skLineSegment(sketch, "E1122", {"start": v(-197.79, 34.57) * mm, "end": v(-197.79, 35.58) * mm});
            skLineSegment(sketch, "E1123", {"start": v(-197.79, 35.58) * mm, "end": v(-211.79, 35.58) * mm});
            skLineSegment(sketch, "E1124", {"start": v(-183.21, 35.58) * mm, "end": v(-183.21, 34.57) * mm});
            skLineSegment(sketch, "E1125", {"start": v(-183.21, 34.57) * mm, "end": v(-184.01, 34.57) * mm});
            skLineSegment(sketch, "E1126", {"start": v(-184.01, 34.57) * mm, "end": v(-184.01, 31.48) * mm});
            skLineSegment(sketch, "E1127", {"start": v(-184.01, 31.48) * mm, "end": v(-183.21, 31.48) * mm});
            skLineSegment(sketch, "E1128", {"start": v(-183.21, 31.48) * mm, "end": v(-183.21, 25.68) * mm});
            skLineSegment(sketch, "E1129", {"start": v(-183.21, 25.68) * mm, "end": v(-184.01, 25.68) * mm});
            skLineSegment(sketch, "E1130", {"start": v(-184.01, 25.68) * mm, "end": v(-184.01, 22.57) * mm});
            skLineSegment(sketch, "E1131", {"start": v(-184.01, 22.57) * mm, "end": v(-183.21, 22.57) * mm});
            skLineSegment(sketch, "E1132", {"start": v(-183.21, 22.57) * mm, "end": v(-183.21, 21.58) * mm});
            skLineSegment(sketch, "E1133", {"start": v(-183.21, 21.58) * mm, "end": v(-169.21, 21.58) * mm});
            skLineSegment(sketch, "E1134", {"start": v(-169.21, 21.58) * mm, "end": v(-169.21, 22.57) * mm});
            skLineSegment(sketch, "E1135", {"start": v(-169.21, 22.57) * mm, "end": v(-168.41, 22.57) * mm});
            skLineSegment(sketch, "E1136", {"start": v(-168.41, 22.57) * mm, "end": v(-168.41, 25.68) * mm});
            skLineSegment(sketch, "E1137", {"start": v(-168.41, 25.68) * mm, "end": v(-169.21, 25.68) * mm});
            skLineSegment(sketch, "E1138", {"start": v(-169.21, 25.68) * mm, "end": v(-169.21, 31.48) * mm});
            skLineSegment(sketch, "E1139", {"start": v(-169.21, 31.48) * mm, "end": v(-168.41, 31.48) * mm});
            skLineSegment(sketch, "E1140", {"start": v(-168.41, 31.48) * mm, "end": v(-168.41, 34.57) * mm});
            skLineSegment(sketch, "E1141", {"start": v(-168.41, 34.57) * mm, "end": v(-169.21, 34.57) * mm});
            skLineSegment(sketch, "E1142", {"start": v(-169.21, 34.57) * mm, "end": v(-169.21, 35.58) * mm});
            skLineSegment(sketch, "E1143", {"start": v(-169.21, 35.58) * mm, "end": v(-183.21, 35.58) * mm});
            skLineSegment(sketch, "E1144", {"start": v(-149.87, 35.58) * mm, "end": v(-149.87, 34.57) * mm});
            skLineSegment(sketch, "E1145", {"start": v(-149.87, 34.57) * mm, "end": v(-150.68, 34.57) * mm});
            skLineSegment(sketch, "E1146", {"start": v(-150.68, 34.57) * mm, "end": v(-150.68, 31.48) * mm});
            skLineSegment(sketch, "E1147", {"start": v(-150.68, 31.48) * mm, "end": v(-149.87, 31.48) * mm});
            skLineSegment(sketch, "E1148", {"start": v(-149.87, 31.48) * mm, "end": v(-149.87, 25.68) * mm});
            skLineSegment(sketch, "E1149", {"start": v(-149.87, 25.68) * mm, "end": v(-150.68, 25.68) * mm});
            skLineSegment(sketch, "E1150", {"start": v(-150.68, 25.68) * mm, "end": v(-150.68, 22.57) * mm});
            skLineSegment(sketch, "E1151", {"start": v(-150.68, 22.57) * mm, "end": v(-149.87, 22.57) * mm});
            skLineSegment(sketch, "E1152", {"start": v(-149.87, 22.57) * mm, "end": v(-149.87, 21.58) * mm});
            skLineSegment(sketch, "E1153", {"start": v(-149.87, 21.58) * mm, "end": v(-135.88, 21.58) * mm});
            skLineSegment(sketch, "E1154", {"start": v(-135.88, 21.58) * mm, "end": v(-135.88, 22.57) * mm});
            skLineSegment(sketch, "E1155", {"start": v(-135.88, 22.57) * mm, "end": v(-135.07, 22.57) * mm});
            skLineSegment(sketch, "E1156", {"start": v(-135.07, 22.57) * mm, "end": v(-135.07, 25.68) * mm});
            skLineSegment(sketch, "E1157", {"start": v(-135.07, 25.68) * mm, "end": v(-135.88, 25.68) * mm});
            skLineSegment(sketch, "E1158", {"start": v(-135.88, 25.68) * mm, "end": v(-135.88, 31.48) * mm});
            skLineSegment(sketch, "E1159", {"start": v(-135.88, 31.48) * mm, "end": v(-135.07, 31.48) * mm});
            skLineSegment(sketch, "E1160", {"start": v(-135.07, 31.48) * mm, "end": v(-135.07, 34.57) * mm});
            skLineSegment(sketch, "E1161", {"start": v(-135.07, 34.57) * mm, "end": v(-135.88, 34.57) * mm});
            skLineSegment(sketch, "E1162", {"start": v(-135.88, 34.57) * mm, "end": v(-135.88, 35.58) * mm});
            skLineSegment(sketch, "E1163", {"start": v(-135.88, 35.58) * mm, "end": v(-149.87, 35.58) * mm});
            skLineSegment(sketch, "E1164", {"start": v(-126.06, 35.58) * mm, "end": v(-126.06, 34.57) * mm});
            skLineSegment(sketch, "E1165", {"start": v(-126.06, 34.57) * mm, "end": v(-126.86, 34.57) * mm});
            skLineSegment(sketch, "E1166", {"start": v(-126.86, 34.57) * mm, "end": v(-126.86, 31.48) * mm});
            skLineSegment(sketch, "E1167", {"start": v(-126.86, 31.48) * mm, "end": v(-126.06, 31.48) * mm});
            skLineSegment(sketch, "E1168", {"start": v(-126.06, 31.48) * mm, "end": v(-126.06, 25.68) * mm});
            skLineSegment(sketch, "E1169", {"start": v(-126.06, 25.68) * mm, "end": v(-126.86, 25.68) * mm});
            skLineSegment(sketch, "E1170", {"start": v(-126.86, 25.68) * mm, "end": v(-126.86, 22.57) * mm});
            skLineSegment(sketch, "E1171", {"start": v(-126.86, 22.57) * mm, "end": v(-126.06, 22.57) * mm});
            skLineSegment(sketch, "E1172", {"start": v(-126.06, 22.57) * mm, "end": v(-126.06, 21.58) * mm});
            skLineSegment(sketch, "E1173", {"start": v(-126.06, 21.58) * mm, "end": v(-112.06, 21.58) * mm});
            skLineSegment(sketch, "E1174", {"start": v(-112.06, 21.58) * mm, "end": v(-112.06, 22.57) * mm});
            skLineSegment(sketch, "E1175", {"start": v(-112.06, 22.57) * mm, "end": v(-111.26, 22.57) * mm});
            skLineSegment(sketch, "E1176", {"start": v(-111.26, 22.57) * mm, "end": v(-111.26, 25.68) * mm});
            skLineSegment(sketch, "E1177", {"start": v(-111.26, 25.68) * mm, "end": v(-112.06, 25.68) * mm});
            skLineSegment(sketch, "E1178", {"start": v(-112.06, 25.68) * mm, "end": v(-112.06, 31.48) * mm});
            skLineSegment(sketch, "E1179", {"start": v(-112.06, 31.48) * mm, "end": v(-111.26, 31.48) * mm});
            skLineSegment(sketch, "E1180", {"start": v(-111.26, 31.48) * mm, "end": v(-111.26, 34.57) * mm});
            skLineSegment(sketch, "E1181", {"start": v(-111.26, 34.57) * mm, "end": v(-112.06, 34.57) * mm});
            skLineSegment(sketch, "E1182", {"start": v(-112.06, 34.57) * mm, "end": v(-112.06, 35.58) * mm});
            skLineSegment(sketch, "E1183", {"start": v(-112.06, 35.58) * mm, "end": v(-126.06, 35.58) * mm});
            skLineSegment(sketch, "E1184", {"start": v(-107.01, 35.58) * mm, "end": v(-107.01, 34.57) * mm});
            skLineSegment(sketch, "E1185", {"start": v(-107.01, 34.57) * mm, "end": v(-107.81, 34.57) * mm});
            skLineSegment(sketch, "E1186", {"start": v(-107.81, 34.57) * mm, "end": v(-107.81, 31.48) * mm});
            skLineSegment(sketch, "E1187", {"start": v(-107.81, 31.48) * mm, "end": v(-107.01, 31.48) * mm});
            skLineSegment(sketch, "E1188", {"start": v(-107.01, 31.48) * mm, "end": v(-107.01, 25.68) * mm});
            skLineSegment(sketch, "E1189", {"start": v(-107.01, 25.68) * mm, "end": v(-107.81, 25.68) * mm});
            skLineSegment(sketch, "E1190", {"start": v(-107.81, 25.68) * mm, "end": v(-107.81, 22.57) * mm});
            skLineSegment(sketch, "E1191", {"start": v(-107.81, 22.57) * mm, "end": v(-107.01, 22.57) * mm});
            skLineSegment(sketch, "E1192", {"start": v(-107.01, 22.57) * mm, "end": v(-107.01, 21.58) * mm});
            skLineSegment(sketch, "E1193", {"start": v(-107.01, 21.58) * mm, "end": v(-93.01, 21.58) * mm});
            skLineSegment(sketch, "E1194", {"start": v(-93.01, 21.58) * mm, "end": v(-93.01, 22.57) * mm});
            skLineSegment(sketch, "E1195", {"start": v(-93.01, 22.57) * mm, "end": v(-92.21, 22.57) * mm});
            skLineSegment(sketch, "E1196", {"start": v(-92.21, 22.57) * mm, "end": v(-92.21, 25.68) * mm});
            skLineSegment(sketch, "E1197", {"start": v(-92.21, 25.68) * mm, "end": v(-93.01, 25.68) * mm});
            skLineSegment(sketch, "E1198", {"start": v(-93.01, 25.68) * mm, "end": v(-93.01, 31.48) * mm});
            skLineSegment(sketch, "E1199", {"start": v(-93.01, 31.48) * mm, "end": v(-92.21, 31.48) * mm});
            skLineSegment(sketch, "E1200", {"start": v(-92.21, 31.48) * mm, "end": v(-92.21, 34.57) * mm});
            skLineSegment(sketch, "E1201", {"start": v(-92.21, 34.57) * mm, "end": v(-93.01, 34.57) * mm});
            skLineSegment(sketch, "E1202", {"start": v(-93.01, 34.57) * mm, "end": v(-93.01, 35.58) * mm});
            skLineSegment(sketch, "E1203", {"start": v(-93.01, 35.58) * mm, "end": v(-107.01, 35.58) * mm});
            skLineSegment(sketch, "E1204", {"start": v(-87.96, 35.58) * mm, "end": v(-87.96, 34.57) * mm});
            skLineSegment(sketch, "E1205", {"start": v(-87.96, 34.57) * mm, "end": v(-88.76, 34.57) * mm});
            skLineSegment(sketch, "E1206", {"start": v(-88.76, 34.57) * mm, "end": v(-88.76, 31.48) * mm});
            skLineSegment(sketch, "E1207", {"start": v(-88.76, 31.48) * mm, "end": v(-87.96, 31.48) * mm});
            skLineSegment(sketch, "E1208", {"start": v(-87.96, 31.48) * mm, "end": v(-87.96, 25.68) * mm});
            skLineSegment(sketch, "E1209", {"start": v(-87.96, 25.68) * mm, "end": v(-88.76, 25.68) * mm});
            skLineSegment(sketch, "E1210", {"start": v(-88.76, 25.68) * mm, "end": v(-88.76, 22.57) * mm});
            skLineSegment(sketch, "E1211", {"start": v(-88.76, 22.57) * mm, "end": v(-87.96, 22.57) * mm});
            skLineSegment(sketch, "E1212", {"start": v(-87.96, 22.57) * mm, "end": v(-87.96, 21.58) * mm});
            skLineSegment(sketch, "E1213", {"start": v(-87.96, 21.58) * mm, "end": v(-73.96, 21.58) * mm});
            skLineSegment(sketch, "E1214", {"start": v(-73.96, 21.58) * mm, "end": v(-73.96, 22.57) * mm});
            skLineSegment(sketch, "E1215", {"start": v(-73.96, 22.57) * mm, "end": v(-73.16, 22.57) * mm});
            skLineSegment(sketch, "E1216", {"start": v(-73.16, 22.57) * mm, "end": v(-73.16, 25.68) * mm});
            skLineSegment(sketch, "E1217", {"start": v(-73.16, 25.68) * mm, "end": v(-73.96, 25.68) * mm});
            skLineSegment(sketch, "E1218", {"start": v(-73.96, 25.68) * mm, "end": v(-73.96, 31.48) * mm});
            skLineSegment(sketch, "E1219", {"start": v(-73.96, 31.48) * mm, "end": v(-73.16, 31.48) * mm});
            skLineSegment(sketch, "E1220", {"start": v(-73.16, 31.48) * mm, "end": v(-73.16, 34.57) * mm});
            skLineSegment(sketch, "E1221", {"start": v(-73.16, 34.57) * mm, "end": v(-73.96, 34.57) * mm});
            skLineSegment(sketch, "E1222", {"start": v(-73.96, 34.57) * mm, "end": v(-73.96, 35.58) * mm});
            skLineSegment(sketch, "E1223", {"start": v(-73.96, 35.58) * mm, "end": v(-87.96, 35.58) * mm});
            skLineSegment(sketch, "E1224", {"start": v(-68.91, 35.58) * mm, "end": v(-68.91, 34.57) * mm});
            skLineSegment(sketch, "E1225", {"start": v(-68.91, 34.57) * mm, "end": v(-69.71, 34.57) * mm});
            skLineSegment(sketch, "E1226", {"start": v(-69.71, 34.57) * mm, "end": v(-69.71, 31.48) * mm});
            skLineSegment(sketch, "E1227", {"start": v(-69.71, 31.48) * mm, "end": v(-68.91, 31.48) * mm});
            skLineSegment(sketch, "E1228", {"start": v(-68.91, 31.48) * mm, "end": v(-68.91, 25.68) * mm});
            skLineSegment(sketch, "E1229", {"start": v(-68.91, 25.68) * mm, "end": v(-69.71, 25.68) * mm});
            skLineSegment(sketch, "E1230", {"start": v(-69.71, 25.68) * mm, "end": v(-69.71, 22.57) * mm});
            skLineSegment(sketch, "E1231", {"start": v(-69.71, 22.57) * mm, "end": v(-68.91, 22.57) * mm});
            skLineSegment(sketch, "E1232", {"start": v(-68.91, 22.57) * mm, "end": v(-68.91, 21.58) * mm});
            skLineSegment(sketch, "E1233", {"start": v(-68.91, 21.58) * mm, "end": v(-54.91, 21.58) * mm});
            skLineSegment(sketch, "E1234", {"start": v(-54.91, 21.58) * mm, "end": v(-54.91, 22.57) * mm});
            skLineSegment(sketch, "E1235", {"start": v(-54.91, 22.57) * mm, "end": v(-54.11, 22.57) * mm});
            skLineSegment(sketch, "E1236", {"start": v(-54.11, 22.57) * mm, "end": v(-54.11, 25.68) * mm});
            skLineSegment(sketch, "E1237", {"start": v(-54.11, 25.68) * mm, "end": v(-54.91, 25.68) * mm});
            skLineSegment(sketch, "E1238", {"start": v(-54.91, 25.68) * mm, "end": v(-54.91, 31.48) * mm});
            skLineSegment(sketch, "E1239", {"start": v(-54.91, 31.48) * mm, "end": v(-54.11, 31.48) * mm});
            skLineSegment(sketch, "E1240", {"start": v(-54.11, 31.48) * mm, "end": v(-54.11, 34.57) * mm});
            skLineSegment(sketch, "E1241", {"start": v(-54.11, 34.57) * mm, "end": v(-54.91, 34.57) * mm});
            skLineSegment(sketch, "E1242", {"start": v(-54.91, 34.57) * mm, "end": v(-54.91, 35.58) * mm});
            skLineSegment(sketch, "E1243", {"start": v(-54.91, 35.58) * mm, "end": v(-68.91, 35.58) * mm});
            skLineSegment(sketch, "E1244", {"start": v(-49.86, 35.58) * mm, "end": v(-49.86, 34.57) * mm});
            skLineSegment(sketch, "E1245", {"start": v(-49.86, 34.57) * mm, "end": v(-50.66, 34.57) * mm});
            skLineSegment(sketch, "E1246", {"start": v(-50.66, 34.57) * mm, "end": v(-50.66, 31.48) * mm});
            skLineSegment(sketch, "E1247", {"start": v(-50.66, 31.48) * mm, "end": v(-49.86, 31.48) * mm});
            skLineSegment(sketch, "E1248", {"start": v(-49.86, 31.48) * mm, "end": v(-49.86, 25.68) * mm});
            skLineSegment(sketch, "E1249", {"start": v(-49.86, 25.68) * mm, "end": v(-50.66, 25.68) * mm});
            skLineSegment(sketch, "E1250", {"start": v(-50.66, 25.68) * mm, "end": v(-50.66, 22.57) * mm});
            skLineSegment(sketch, "E1251", {"start": v(-50.66, 22.57) * mm, "end": v(-49.86, 22.57) * mm});
            skLineSegment(sketch, "E1252", {"start": v(-49.86, 22.57) * mm, "end": v(-49.86, 21.58) * mm});
            skLineSegment(sketch, "E1253", {"start": v(-49.86, 21.58) * mm, "end": v(-35.86, 21.58) * mm});
            skLineSegment(sketch, "E1254", {"start": v(-35.86, 21.58) * mm, "end": v(-35.86, 22.57) * mm});
            skLineSegment(sketch, "E1255", {"start": v(-35.86, 22.57) * mm, "end": v(-35.06, 22.57) * mm});
            skLineSegment(sketch, "E1256", {"start": v(-35.06, 22.57) * mm, "end": v(-35.06, 25.68) * mm});
            skLineSegment(sketch, "E1257", {"start": v(-35.06, 25.68) * mm, "end": v(-35.86, 25.68) * mm});
            skLineSegment(sketch, "E1258", {"start": v(-35.86, 25.68) * mm, "end": v(-35.86, 31.48) * mm});
            skLineSegment(sketch, "E1259", {"start": v(-35.86, 31.48) * mm, "end": v(-35.06, 31.48) * mm});
            skLineSegment(sketch, "E1260", {"start": v(-35.06, 31.48) * mm, "end": v(-35.06, 34.57) * mm});
            skLineSegment(sketch, "E1261", {"start": v(-35.06, 34.57) * mm, "end": v(-35.86, 34.57) * mm});
            skLineSegment(sketch, "E1262", {"start": v(-35.86, 34.57) * mm, "end": v(-35.86, 35.58) * mm});
            skLineSegment(sketch, "E1263", {"start": v(-35.86, 35.58) * mm, "end": v(-49.86, 35.58) * mm});
            skLineSegment(sketch, "E1264", {"start": v(-30.81, 35.58) * mm, "end": v(-30.81, 34.57) * mm});
            skLineSegment(sketch, "E1265", {"start": v(-30.81, 34.57) * mm, "end": v(-31.61, 34.57) * mm});
            skLineSegment(sketch, "E1266", {"start": v(-31.61, 34.57) * mm, "end": v(-31.61, 31.48) * mm});
            skLineSegment(sketch, "E1267", {"start": v(-31.61, 31.48) * mm, "end": v(-30.81, 31.48) * mm});
            skLineSegment(sketch, "E1268", {"start": v(-30.81, 31.48) * mm, "end": v(-30.81, 25.68) * mm});
            skLineSegment(sketch, "E1269", {"start": v(-30.81, 25.68) * mm, "end": v(-31.61, 25.68) * mm});
            skLineSegment(sketch, "E1270", {"start": v(-31.61, 25.68) * mm, "end": v(-31.61, 22.57) * mm});
            skLineSegment(sketch, "E1271", {"start": v(-31.61, 22.57) * mm, "end": v(-30.81, 22.57) * mm});
            skLineSegment(sketch, "E1272", {"start": v(-30.81, 22.57) * mm, "end": v(-30.81, 21.58) * mm});
            skLineSegment(sketch, "E1273", {"start": v(-30.81, 21.58) * mm, "end": v(-16.81, 21.58) * mm});
            skLineSegment(sketch, "E1274", {"start": v(-16.81, 21.58) * mm, "end": v(-16.81, 22.57) * mm});
            skLineSegment(sketch, "E1275", {"start": v(-16.81, 22.57) * mm, "end": v(-16.01, 22.57) * mm});
            skLineSegment(sketch, "E1276", {"start": v(-16.01, 22.57) * mm, "end": v(-16.01, 25.68) * mm});
            skLineSegment(sketch, "E1277", {"start": v(-16.01, 25.68) * mm, "end": v(-16.81, 25.68) * mm});
            skLineSegment(sketch, "E1278", {"start": v(-16.81, 25.68) * mm, "end": v(-16.81, 31.48) * mm});
            skLineSegment(sketch, "E1279", {"start": v(-16.81, 31.48) * mm, "end": v(-16.01, 31.48) * mm});
            skLineSegment(sketch, "E1280", {"start": v(-16.01, 31.48) * mm, "end": v(-16.01, 34.57) * mm});
            skLineSegment(sketch, "E1281", {"start": v(-16.01, 34.57) * mm, "end": v(-16.81, 34.57) * mm});
            skLineSegment(sketch, "E1282", {"start": v(-16.81, 34.57) * mm, "end": v(-16.81, 35.58) * mm});
            skLineSegment(sketch, "E1283", {"start": v(-16.81, 35.58) * mm, "end": v(-30.81, 35.58) * mm});
            skLineSegment(sketch, "E1284", {"start": v(-11.76, 35.58) * mm, "end": v(-11.76, 34.57) * mm});
            skLineSegment(sketch, "E1285", {"start": v(-11.76, 34.57) * mm, "end": v(-12.56, 34.57) * mm});
            skLineSegment(sketch, "E1286", {"start": v(-12.56, 34.57) * mm, "end": v(-12.56, 31.48) * mm});
            skLineSegment(sketch, "E1287", {"start": v(-12.56, 31.48) * mm, "end": v(-11.76, 31.48) * mm});
            skLineSegment(sketch, "E1288", {"start": v(-11.76, 31.48) * mm, "end": v(-11.76, 25.68) * mm});
            skLineSegment(sketch, "E1289", {"start": v(-11.76, 25.68) * mm, "end": v(-12.56, 25.68) * mm});
            skLineSegment(sketch, "E1290", {"start": v(-12.56, 25.68) * mm, "end": v(-12.56, 22.57) * mm});
            skLineSegment(sketch, "E1291", {"start": v(-12.56, 22.57) * mm, "end": v(-11.76, 22.57) * mm});
            skLineSegment(sketch, "E1292", {"start": v(-11.76, 22.57) * mm, "end": v(-11.76, 21.58) * mm});
            skLineSegment(sketch, "E1293", {"start": v(-11.76, 21.58) * mm, "end": v(2.24, 21.58) * mm});
            skLineSegment(sketch, "E1294", {"start": v(2.24, 21.58) * mm, "end": v(2.24, 22.57) * mm});
            skLineSegment(sketch, "E1295", {"start": v(2.24, 22.57) * mm, "end": v(3.04, 22.57) * mm});
            skLineSegment(sketch, "E1296", {"start": v(3.04, 22.57) * mm, "end": v(3.04, 25.68) * mm});
            skLineSegment(sketch, "E1297", {"start": v(3.04, 25.68) * mm, "end": v(2.24, 25.68) * mm});
            skLineSegment(sketch, "E1298", {"start": v(2.24, 25.68) * mm, "end": v(2.24, 31.48) * mm});
            skLineSegment(sketch, "E1299", {"start": v(2.24, 31.48) * mm, "end": v(3.04, 31.48) * mm});
            skLineSegment(sketch, "E1300", {"start": v(3.04, 31.48) * mm, "end": v(3.04, 34.57) * mm});
            skLineSegment(sketch, "E1301", {"start": v(3.04, 34.57) * mm, "end": v(2.24, 34.57) * mm});
            skLineSegment(sketch, "E1302", {"start": v(2.24, 34.57) * mm, "end": v(2.24, 35.58) * mm});
            skLineSegment(sketch, "E1303", {"start": v(2.24, 35.58) * mm, "end": v(-11.76, 35.58) * mm});
            skLineSegment(sketch, "E1304", {"start": v(7.29, 35.58) * mm, "end": v(7.29, 34.57) * mm});
            skLineSegment(sketch, "E1305", {"start": v(7.29, 34.57) * mm, "end": v(6.49, 34.57) * mm});
            skLineSegment(sketch, "E1306", {"start": v(6.49, 34.57) * mm, "end": v(6.49, 31.48) * mm});
            skLineSegment(sketch, "E1307", {"start": v(6.49, 31.48) * mm, "end": v(7.29, 31.48) * mm});
            skLineSegment(sketch, "E1308", {"start": v(7.29, 31.48) * mm, "end": v(7.29, 25.68) * mm});
            skLineSegment(sketch, "E1309", {"start": v(7.29, 25.68) * mm, "end": v(6.49, 25.68) * mm});
            skLineSegment(sketch, "E1310", {"start": v(6.49, 25.68) * mm, "end": v(6.49, 22.57) * mm});
            skLineSegment(sketch, "E1311", {"start": v(6.49, 22.57) * mm, "end": v(7.29, 22.57) * mm});
            skLineSegment(sketch, "E1312", {"start": v(7.29, 22.57) * mm, "end": v(7.29, 21.58) * mm});
            skLineSegment(sketch, "E1313", {"start": v(7.29, 21.58) * mm, "end": v(21.29, 21.58) * mm});
            skLineSegment(sketch, "E1314", {"start": v(21.29, 21.58) * mm, "end": v(21.29, 22.57) * mm});
            skLineSegment(sketch, "E1315", {"start": v(21.29, 22.57) * mm, "end": v(22.09, 22.57) * mm});
            skLineSegment(sketch, "E1316", {"start": v(22.09, 22.57) * mm, "end": v(22.09, 25.68) * mm});
            skLineSegment(sketch, "E1317", {"start": v(22.09, 25.68) * mm, "end": v(21.29, 25.68) * mm});
            skLineSegment(sketch, "E1318", {"start": v(21.29, 25.68) * mm, "end": v(21.29, 31.48) * mm});
            skLineSegment(sketch, "E1319", {"start": v(21.29, 31.48) * mm, "end": v(22.09, 31.48) * mm});
            skLineSegment(sketch, "E1320", {"start": v(22.09, 31.48) * mm, "end": v(22.09, 34.57) * mm});
            skLineSegment(sketch, "E1321", {"start": v(22.09, 34.57) * mm, "end": v(21.29, 34.57) * mm});
            skLineSegment(sketch, "E1322", {"start": v(21.29, 34.57) * mm, "end": v(21.29, 35.58) * mm});
            skLineSegment(sketch, "E1323", {"start": v(21.29, 35.58) * mm, "end": v(7.29, 35.58) * mm});
            skLineSegment(sketch, "E1324", {"start": v(26.34, 35.58) * mm, "end": v(26.34, 34.57) * mm});
            skLineSegment(sketch, "E1325", {"start": v(26.34, 34.57) * mm, "end": v(25.54, 34.57) * mm});
            skLineSegment(sketch, "E1326", {"start": v(25.54, 34.57) * mm, "end": v(25.54, 31.48) * mm});
            skLineSegment(sketch, "E1327", {"start": v(25.54, 31.48) * mm, "end": v(26.34, 31.48) * mm});
            skLineSegment(sketch, "E1328", {"start": v(26.34, 31.48) * mm, "end": v(26.34, 25.68) * mm});
            skLineSegment(sketch, "E1329", {"start": v(26.34, 25.68) * mm, "end": v(25.54, 25.68) * mm});
            skLineSegment(sketch, "E1330", {"start": v(25.54, 25.68) * mm, "end": v(25.54, 22.57) * mm});
            skLineSegment(sketch, "E1331", {"start": v(25.54, 22.57) * mm, "end": v(26.34, 22.57) * mm});
            skLineSegment(sketch, "E1332", {"start": v(26.34, 22.57) * mm, "end": v(26.34, 21.58) * mm});
            skLineSegment(sketch, "E1333", {"start": v(26.34, 21.58) * mm, "end": v(40.34, 21.58) * mm});
            skLineSegment(sketch, "E1334", {"start": v(40.34, 21.58) * mm, "end": v(40.34, 22.57) * mm});
            skLineSegment(sketch, "E1335", {"start": v(40.34, 22.57) * mm, "end": v(41.14, 22.57) * mm});
            skLineSegment(sketch, "E1336", {"start": v(41.14, 22.57) * mm, "end": v(41.14, 25.68) * mm});
            skLineSegment(sketch, "E1337", {"start": v(41.14, 25.68) * mm, "end": v(40.34, 25.68) * mm});
            skLineSegment(sketch, "E1338", {"start": v(40.34, 25.68) * mm, "end": v(40.34, 31.48) * mm});
            skLineSegment(sketch, "E1339", {"start": v(40.34, 31.48) * mm, "end": v(41.14, 31.48) * mm});
            skLineSegment(sketch, "E1340", {"start": v(41.14, 31.48) * mm, "end": v(41.14, 34.57) * mm});
            skLineSegment(sketch, "E1341", {"start": v(41.14, 34.57) * mm, "end": v(40.34, 34.57) * mm});
            skLineSegment(sketch, "E1342", {"start": v(40.34, 34.57) * mm, "end": v(40.34, 35.58) * mm});
            skLineSegment(sketch, "E1343", {"start": v(40.34, 35.58) * mm, "end": v(26.34, 35.58) * mm});
            skLineSegment(sketch, "E1344", {"start": v(45.39, 35.58) * mm, "end": v(45.39, 34.57) * mm});
            skLineSegment(sketch, "E1345", {"start": v(45.39, 34.57) * mm, "end": v(44.59, 34.57) * mm});
            skLineSegment(sketch, "E1346", {"start": v(44.59, 34.57) * mm, "end": v(44.59, 31.48) * mm});
            skLineSegment(sketch, "E1347", {"start": v(44.59, 31.48) * mm, "end": v(45.39, 31.48) * mm});
            skLineSegment(sketch, "E1348", {"start": v(45.39, 31.48) * mm, "end": v(45.39, 25.68) * mm});
            skLineSegment(sketch, "E1349", {"start": v(45.39, 25.68) * mm, "end": v(44.59, 25.68) * mm});
            skLineSegment(sketch, "E1350", {"start": v(44.59, 25.68) * mm, "end": v(44.59, 22.57) * mm});
            skLineSegment(sketch, "E1351", {"start": v(44.59, 22.57) * mm, "end": v(45.39, 22.57) * mm});
            skLineSegment(sketch, "E1352", {"start": v(45.39, 22.57) * mm, "end": v(45.39, 21.58) * mm});
            skLineSegment(sketch, "E1353", {"start": v(45.39, 21.58) * mm, "end": v(59.39, 21.58) * mm});
            skLineSegment(sketch, "E1354", {"start": v(59.39, 21.58) * mm, "end": v(59.39, 22.57) * mm});
            skLineSegment(sketch, "E1355", {"start": v(59.39, 22.57) * mm, "end": v(60.19, 22.57) * mm});
            skLineSegment(sketch, "E1356", {"start": v(60.19, 22.57) * mm, "end": v(60.19, 25.68) * mm});
            skLineSegment(sketch, "E1357", {"start": v(60.19, 25.68) * mm, "end": v(59.39, 25.68) * mm});
            skLineSegment(sketch, "E1358", {"start": v(59.39, 25.68) * mm, "end": v(59.39, 31.48) * mm});
            skLineSegment(sketch, "E1359", {"start": v(59.39, 31.48) * mm, "end": v(60.19, 31.48) * mm});
            skLineSegment(sketch, "E1360", {"start": v(60.19, 31.48) * mm, "end": v(60.19, 34.57) * mm});
            skLineSegment(sketch, "E1361", {"start": v(60.19, 34.57) * mm, "end": v(59.39, 34.57) * mm});
            skLineSegment(sketch, "E1362", {"start": v(59.39, 34.57) * mm, "end": v(59.39, 35.58) * mm});
            skLineSegment(sketch, "E1363", {"start": v(59.39, 35.58) * mm, "end": v(45.39, 35.58) * mm});
            skLineSegment(sketch, "E1364", {"start": v(140.64, 35.58) * mm, "end": v(140.64, 34.57) * mm});
            skLineSegment(sketch, "E1365", {"start": v(140.64, 34.57) * mm, "end": v(139.84, 34.57) * mm});
            skLineSegment(sketch, "E1366", {"start": v(139.84, 34.57) * mm, "end": v(139.84, 31.48) * mm});
            skLineSegment(sketch, "E1367", {"start": v(139.84, 31.48) * mm, "end": v(140.64, 31.48) * mm});
            skLineSegment(sketch, "E1368", {"start": v(140.64, 31.48) * mm, "end": v(140.64, 25.68) * mm});
            skLineSegment(sketch, "E1369", {"start": v(140.64, 25.68) * mm, "end": v(139.84, 25.68) * mm});
            skLineSegment(sketch, "E1370", {"start": v(139.84, 25.68) * mm, "end": v(139.84, 22.57) * mm});
            skLineSegment(sketch, "E1371", {"start": v(139.84, 22.57) * mm, "end": v(140.64, 22.57) * mm});
            skLineSegment(sketch, "E1372", {"start": v(140.64, 22.57) * mm, "end": v(140.64, 21.58) * mm});
            skLineSegment(sketch, "E1373", {"start": v(140.64, 21.58) * mm, "end": v(154.64, 21.58) * mm});
            skLineSegment(sketch, "E1374", {"start": v(154.64, 21.58) * mm, "end": v(154.64, 22.57) * mm});
            skLineSegment(sketch, "E1375", {"start": v(154.64, 22.57) * mm, "end": v(155.44, 22.57) * mm});
            skLineSegment(sketch, "E1376", {"start": v(155.44, 22.57) * mm, "end": v(155.44, 25.68) * mm});
            skLineSegment(sketch, "E1377", {"start": v(155.44, 25.68) * mm, "end": v(154.64, 25.68) * mm});
            skLineSegment(sketch, "E1378", {"start": v(154.64, 25.68) * mm, "end": v(154.64, 31.48) * mm});
            skLineSegment(sketch, "E1379", {"start": v(154.64, 31.48) * mm, "end": v(155.44, 31.48) * mm});
            skLineSegment(sketch, "E1380", {"start": v(155.44, 31.48) * mm, "end": v(155.44, 34.57) * mm});
            skLineSegment(sketch, "E1381", {"start": v(155.44, 34.57) * mm, "end": v(154.64, 34.57) * mm});
            skLineSegment(sketch, "E1382", {"start": v(154.64, 34.57) * mm, "end": v(154.64, 35.58) * mm});
            skLineSegment(sketch, "E1383", {"start": v(154.64, 35.58) * mm, "end": v(140.64, 35.58) * mm});
            skLineSegment(sketch, "E1384", {"start": v(159.69, 35.58) * mm, "end": v(159.69, 34.57) * mm});
            skLineSegment(sketch, "E1385", {"start": v(159.69, 34.57) * mm, "end": v(158.89, 34.57) * mm});
            skLineSegment(sketch, "E1386", {"start": v(158.89, 34.57) * mm, "end": v(158.89, 31.48) * mm});
            skLineSegment(sketch, "E1387", {"start": v(158.89, 31.48) * mm, "end": v(159.69, 31.48) * mm});
            skLineSegment(sketch, "E1388", {"start": v(159.69, 31.48) * mm, "end": v(159.69, 25.68) * mm});
            skLineSegment(sketch, "E1389", {"start": v(159.69, 25.68) * mm, "end": v(158.89, 25.68) * mm});
            skLineSegment(sketch, "E1390", {"start": v(158.89, 25.68) * mm, "end": v(158.89, 22.57) * mm});
            skLineSegment(sketch, "E1391", {"start": v(158.89, 22.57) * mm, "end": v(159.69, 22.57) * mm});
            skLineSegment(sketch, "E1392", {"start": v(159.69, 22.57) * mm, "end": v(159.69, 21.58) * mm});
            skLineSegment(sketch, "E1393", {"start": v(159.69, 21.58) * mm, "end": v(173.69, 21.58) * mm});
            skLineSegment(sketch, "E1394", {"start": v(173.69, 21.58) * mm, "end": v(173.69, 22.57) * mm});
            skLineSegment(sketch, "E1395", {"start": v(173.69, 22.57) * mm, "end": v(174.49, 22.57) * mm});
            skLineSegment(sketch, "E1396", {"start": v(174.49, 22.57) * mm, "end": v(174.49, 25.68) * mm});
            skLineSegment(sketch, "E1397", {"start": v(174.49, 25.68) * mm, "end": v(173.69, 25.68) * mm});
            skLineSegment(sketch, "E1398", {"start": v(173.69, 25.68) * mm, "end": v(173.69, 31.48) * mm});
            skLineSegment(sketch, "E1399", {"start": v(173.69, 31.48) * mm, "end": v(174.49, 31.48) * mm});
            skLineSegment(sketch, "E1400", {"start": v(174.49, 31.48) * mm, "end": v(174.49, 34.57) * mm});
            skLineSegment(sketch, "E1401", {"start": v(174.49, 34.57) * mm, "end": v(173.69, 34.57) * mm});
            skLineSegment(sketch, "E1402", {"start": v(173.69, 34.57) * mm, "end": v(173.69, 35.58) * mm});
            skLineSegment(sketch, "E1403", {"start": v(173.69, 35.58) * mm, "end": v(159.69, 35.58) * mm});
            skLineSegment(sketch, "E1404", {"start": v(178.74, 35.58) * mm, "end": v(178.74, 34.57) * mm});
            skLineSegment(sketch, "E1405", {"start": v(178.74, 34.57) * mm, "end": v(177.94, 34.57) * mm});
            skLineSegment(sketch, "E1406", {"start": v(177.94, 34.57) * mm, "end": v(177.94, 31.48) * mm});
            skLineSegment(sketch, "E1407", {"start": v(177.94, 31.48) * mm, "end": v(178.74, 31.48) * mm});
            skLineSegment(sketch, "E1408", {"start": v(178.74, 31.48) * mm, "end": v(178.74, 25.68) * mm});
            skLineSegment(sketch, "E1409", {"start": v(178.74, 25.68) * mm, "end": v(177.94, 25.68) * mm});
            skLineSegment(sketch, "E1410", {"start": v(177.94, 25.68) * mm, "end": v(177.94, 22.57) * mm});
            skLineSegment(sketch, "E1411", {"start": v(177.94, 22.57) * mm, "end": v(178.74, 22.57) * mm});
            skLineSegment(sketch, "E1412", {"start": v(178.74, 22.57) * mm, "end": v(178.74, 21.58) * mm});
            skLineSegment(sketch, "E1413", {"start": v(178.74, 21.58) * mm, "end": v(192.74, 21.58) * mm});
            skLineSegment(sketch, "E1414", {"start": v(192.74, 21.58) * mm, "end": v(192.74, 22.57) * mm});
            skLineSegment(sketch, "E1415", {"start": v(192.74, 22.57) * mm, "end": v(193.54, 22.57) * mm});
            skLineSegment(sketch, "E1416", {"start": v(193.54, 22.57) * mm, "end": v(193.54, 25.68) * mm});
            skLineSegment(sketch, "E1417", {"start": v(193.54, 25.68) * mm, "end": v(192.74, 25.68) * mm});
            skLineSegment(sketch, "E1418", {"start": v(192.74, 25.68) * mm, "end": v(192.74, 31.48) * mm});
            skLineSegment(sketch, "E1419", {"start": v(192.74, 31.48) * mm, "end": v(193.54, 31.48) * mm});
            skLineSegment(sketch, "E1420", {"start": v(193.54, 31.48) * mm, "end": v(193.54, 34.57) * mm});
            skLineSegment(sketch, "E1421", {"start": v(193.54, 34.57) * mm, "end": v(192.74, 34.57) * mm});
            skLineSegment(sketch, "E1422", {"start": v(192.74, 34.57) * mm, "end": v(192.74, 35.58) * mm});
            skLineSegment(sketch, "E1423", {"start": v(192.74, 35.58) * mm, "end": v(178.74, 35.58) * mm});
            skLineSegment(sketch, "E1424", {"start": v(197.79, 35.58) * mm, "end": v(197.79, 34.57) * mm});
            skLineSegment(sketch, "E1425", {"start": v(197.79, 34.57) * mm, "end": v(196.99, 34.57) * mm});
            skLineSegment(sketch, "E1426", {"start": v(196.99, 34.57) * mm, "end": v(196.99, 31.48) * mm});
            skLineSegment(sketch, "E1427", {"start": v(196.99, 31.48) * mm, "end": v(197.79, 31.48) * mm});
            skLineSegment(sketch, "E1428", {"start": v(197.79, 31.48) * mm, "end": v(197.79, 25.68) * mm});
            skLineSegment(sketch, "E1429", {"start": v(197.79, 25.68) * mm, "end": v(196.99, 25.68) * mm});
            skLineSegment(sketch, "E1430", {"start": v(196.99, 25.68) * mm, "end": v(196.99, 22.57) * mm});
            skLineSegment(sketch, "E1431", {"start": v(196.99, 22.57) * mm, "end": v(197.79, 22.57) * mm});
            skLineSegment(sketch, "E1432", {"start": v(197.79, 22.57) * mm, "end": v(197.79, 21.58) * mm});
            skLineSegment(sketch, "E1433", {"start": v(197.79, 21.58) * mm, "end": v(211.79, 21.58) * mm});
            skLineSegment(sketch, "E1434", {"start": v(211.79, 21.58) * mm, "end": v(211.79, 22.57) * mm});
            skLineSegment(sketch, "E1435", {"start": v(211.79, 22.57) * mm, "end": v(212.59, 22.57) * mm});
            skLineSegment(sketch, "E1436", {"start": v(212.59, 22.57) * mm, "end": v(212.59, 25.68) * mm});
            skLineSegment(sketch, "E1437", {"start": v(212.59, 25.68) * mm, "end": v(211.79, 25.68) * mm});
            skLineSegment(sketch, "E1438", {"start": v(211.79, 25.68) * mm, "end": v(211.79, 31.48) * mm});
            skLineSegment(sketch, "E1439", {"start": v(211.79, 31.48) * mm, "end": v(212.59, 31.48) * mm});
            skLineSegment(sketch, "E1440", {"start": v(212.59, 31.48) * mm, "end": v(212.59, 34.57) * mm});
            skLineSegment(sketch, "E1441", {"start": v(212.59, 34.57) * mm, "end": v(211.79, 34.57) * mm});
            skLineSegment(sketch, "E1442", {"start": v(211.79, 34.57) * mm, "end": v(211.79, 35.58) * mm});
            skLineSegment(sketch, "E1443", {"start": v(211.79, 35.58) * mm, "end": v(197.79, 35.58) * mm});
            skSolve(sketch);
        }
        {
            var Q0;
            Q0 = qSketchRegion(id + "F0", true);
            extrude(context, id + "F1", {"entities" : qUnion([Q0]), "depth" : 1.6 * mm});
        }
        {
            var Q0;
            Q0=makeQuery(id+"F1.opExtrude","CAP_FACE",FACE,{"disambiguationData":[OSD([sQuery(id+"F0.wireOp",EDGE,"E0"),sQuery(id+"F0.wireOp",EDGE,"E1"),sQuery(id+"F0.wireOp",EDGE,"E2"),sQuery(id+"F0.wireOp",EDGE,"E3"),sQuery(id+"F0.wireOp",EDGE,"E4"),sQuery(id+"F0.wireOp",EDGE,"E5"),sQuery(id+"F0.wireOp",EDGE,"E6"),sQuery(id+"F0.wireOp",EDGE,"E7"),sQuery(id+"F0.wireOp",EDGE,"E8"),sQuery(id+"F0.wireOp",EDGE,"E9"),sQuery(id+"F0.wireOp",EDGE,"E10"),sQuery(id+"F0.wireOp",EDGE,"E11"),sQuery(id+"F0.wireOp",EDGE,"E12"),sQuery(id+"F0.wireOp",EDGE,"E13"),sQuery(id+"F0.wireOp",EDGE,"E14"),sQuery(id+"F0.wireOp",EDGE,"E15"),sQuery(id+"F0.wireOp",EDGE,"E16"),sQuery(id+"F0.wireOp",EDGE,"E17"),sQuery(id+"F0.wireOp",EDGE,"E18"),sQuery(id+"F0.wireOp",EDGE,"E19"),sQuery(id+"F0.wireOp",EDGE,"E20"),sQuery(id+"F0.wireOp",EDGE,"E21"),sQuery(id+"F0.wireOp",EDGE,"E22"),sQuery(id+"F0.wireOp",EDGE,"E23"),sQuery(id+"F0.wireOp",EDGE,"E24"),sQuery(id+"F0.wireOp",EDGE,"E25"),sQuery(id+"F0.wireOp",EDGE,"E26"),sQuery(id+"F0.wireOp",EDGE,"E27"),sQuery(id+"F0.wireOp",EDGE,"E28"),sQuery(id+"F0.wireOp",EDGE,"E29"),sQuery(id+"F0.wireOp",EDGE,"E30"),sQuery(id+"F0.wireOp",EDGE,"E31"),sQuery(id+"F0.wireOp",EDGE,"E32"),sQuery(id+"F0.wireOp",EDGE,"E33"),sQuery(id+"F0.wireOp",EDGE,"E34"),sQuery(id+"F0.wireOp",EDGE,"E35"),sQuery(id+"F0.wireOp",EDGE,"E36"),sQuery(id+"F0.wireOp",EDGE,"E37"),sQuery(id+"F0.wireOp",EDGE,"E38"),sQuery(id+"F0.wireOp",EDGE,"E39"),sQuery(id+"F0.wireOp",EDGE,"E40"),sQuery(id+"F0.wireOp",EDGE,"E41"),sQuery(id+"F0.wireOp",EDGE,"E42"),sQuery(id+"F0.wireOp",EDGE,"E43"),sQuery(id+"F0.wireOp",EDGE,"E44"),sQuery(id+"F0.wireOp",EDGE,"E45"),sQuery(id+"F0.wireOp",EDGE,"E46"),sQuery(id+"F0.wireOp",EDGE,"E47"),sQuery(id+"F0.wireOp",EDGE,"E48"),sQuery(id+"F0.wireOp",EDGE,"E49"),sQuery(id+"F0.wireOp",EDGE,"E50"),sQuery(id+"F0.wireOp",EDGE,"E51"),sQuery(id+"F0.wireOp",EDGE,"E52"),sQuery(id+"F0.wireOp",EDGE,"E53"),sQuery(id+"F0.wireOp",EDGE,"E54"),sQuery(id+"F0.wireOp",EDGE,"E55"),sQuery(id+"F0.wireOp",EDGE,"E56"),sQuery(id+"F0.wireOp",EDGE,"E57"),sQuery(id+"F0.wireOp",EDGE,"E58"),sQuery(id+"F0.wireOp",EDGE,"E59"),sQuery(id+"F0.wireOp",EDGE,"E60"),sQuery(id+"F0.wireOp",EDGE,"E61"),sQuery(id+"F0.wireOp",EDGE,"E62"),sQuery(id+"F0.wireOp",EDGE,"E63"),sQuery(id+"F0.wireOp",EDGE,"E64"),sQuery(id+"F0.wireOp",EDGE,"E65"),sQuery(id+"F0.wireOp",EDGE,"E66"),sQuery(id+"F0.wireOp",EDGE,"E67"),sQuery(id+"F0.wireOp",EDGE,"E68"),sQuery(id+"F0.wireOp",EDGE,"E69"),sQuery(id+"F0.wireOp",EDGE,"E70"),sQuery(id+"F0.wireOp",EDGE,"E71"),sQuery(id+"F0.wireOp",EDGE,"E72"),sQuery(id+"F0.wireOp",EDGE,"E73"),sQuery(id+"F0.wireOp",EDGE,"E74"),sQuery(id+"F0.wireOp",EDGE,"E75"),sQuery(id+"F0.wireOp",EDGE,"E76"),sQuery(id+"F0.wireOp",EDGE,"E77"),sQuery(id+"F0.wireOp",EDGE,"E78"),sQuery(id+"F0.wireOp",EDGE,"E79"),sQuery(id+"F0.wireOp",EDGE,"E80"),sQuery(id+"F0.wireOp",EDGE,"E81"),sQuery(id+"F0.wireOp",EDGE,"E82"),sQuery(id+"F0.wireOp",EDGE,"E83"),sQuery(id+"F0.wireOp",EDGE,"E84"),sQuery(id+"F0.wireOp",EDGE,"E85"),sQuery(id+"F0.wireOp",EDGE,"E86"),sQuery(id+"F0.wireOp",EDGE,"E87"),sQuery(id+"F0.wireOp",EDGE,"E88"),sQuery(id+"F0.wireOp",EDGE,"E89"),sQuery(id+"F0.wireOp",EDGE,"E90"),sQuery(id+"F0.wireOp",EDGE,"E91"),sQuery(id+"F0.wireOp",EDGE,"E92"),sQuery(id+"F0.wireOp",EDGE,"E93"),sQuery(id+"F0.wireOp",EDGE,"E94"),sQuery(id+"F0.wireOp",EDGE,"E95"),sQuery(id+"F0.wireOp",EDGE,"E96"),sQuery(id+"F0.wireOp",EDGE,"E97"),sQuery(id+"F0.wireOp",EDGE,"E98"),sQuery(id+"F0.wireOp",EDGE,"E99"),sQuery(id+"F0.wireOp",EDGE,"E100"),sQuery(id+"F0.wireOp",EDGE,"E101"),sQuery(id+"F0.wireOp",EDGE,"E102"),sQuery(id+"F0.wireOp",EDGE,"E103"),sQuery(id+"F0.wireOp",EDGE,"E104"),sQuery(id+"F0.wireOp",EDGE,"E105"),sQuery(id+"F0.wireOp",EDGE,"E106"),sQuery(id+"F0.wireOp",EDGE,"E107"),sQuery(id+"F0.wireOp",EDGE,"E108"),sQuery(id+"F0.wireOp",EDGE,"E109"),sQuery(id+"F0.wireOp",EDGE,"E110"),sQuery(id+"F0.wireOp",EDGE,"E111"),sQuery(id+"F0.wireOp",EDGE,"E112"),sQuery(id+"F0.wireOp",EDGE,"E113"),sQuery(id+"F0.wireOp",EDGE,"E114"),sQuery(id+"F0.wireOp",EDGE,"E115"),sQuery(id+"F0.wireOp",EDGE,"E116"),sQuery(id+"F0.wireOp",EDGE,"E117"),sQuery(id+"F0.wireOp",EDGE,"E118"),sQuery(id+"F0.wireOp",EDGE,"E119"),sQuery(id+"F0.wireOp",EDGE,"E120"),sQuery(id+"F0.wireOp",EDGE,"E121"),sQuery(id+"F0.wireOp",EDGE,"E122"),sQuery(id+"F0.wireOp",EDGE,"E123"),sQuery(id+"F0.wireOp",EDGE,"E124"),sQuery(id+"F0.wireOp",EDGE,"E125"),sQuery(id+"F0.wireOp",EDGE,"E126"),sQuery(id+"F0.wireOp",EDGE,"E127"),sQuery(id+"F0.wireOp",EDGE,"E128"),sQuery(id+"F0.wireOp",EDGE,"E129"),sQuery(id+"F0.wireOp",EDGE,"E130"),sQuery(id+"F0.wireOp",EDGE,"E131"),sQuery(id+"F0.wireOp",EDGE,"E132"),sQuery(id+"F0.wireOp",EDGE,"E133"),sQuery(id+"F0.wireOp",EDGE,"E134"),sQuery(id+"F0.wireOp",EDGE,"E135"),sQuery(id+"F0.wireOp",EDGE,"E136"),sQuery(id+"F0.wireOp",EDGE,"E137"),sQuery(id+"F0.wireOp",EDGE,"E138"),sQuery(id+"F0.wireOp",EDGE,"E139"),sQuery(id+"F0.wireOp",EDGE,"E140"),sQuery(id+"F0.wireOp",EDGE,"E141"),sQuery(id+"F0.wireOp",EDGE,"E142"),sQuery(id+"F0.wireOp",EDGE,"E143"),sQuery(id+"F0.wireOp",EDGE,"E144"),sQuery(id+"F0.wireOp",EDGE,"E145"),sQuery(id+"F0.wireOp",EDGE,"E146"),sQuery(id+"F0.wireOp",EDGE,"E147"),sQuery(id+"F0.wireOp",EDGE,"E148"),sQuery(id+"F0.wireOp",EDGE,"E149"),sQuery(id+"F0.wireOp",EDGE,"E150"),sQuery(id+"F0.wireOp",EDGE,"E151"),sQuery(id+"F0.wireOp",EDGE,"E152"),sQuery(id+"F0.wireOp",EDGE,"E153"),sQuery(id+"F0.wireOp",EDGE,"E154"),sQuery(id+"F0.wireOp",EDGE,"E155"),sQuery(id+"F0.wireOp",EDGE,"E156"),sQuery(id+"F0.wireOp",EDGE,"E157"),sQuery(id+"F0.wireOp",EDGE,"E158"),sQuery(id+"F0.wireOp",EDGE,"E159"),sQuery(id+"F0.wireOp",EDGE,"E160"),sQuery(id+"F0.wireOp",EDGE,"E161"),sQuery(id+"F0.wireOp",EDGE,"E162"),sQuery(id+"F0.wireOp",EDGE,"E163"),sQuery(id+"F0.wireOp",EDGE,"E164"),sQuery(id+"F0.wireOp",EDGE,"E165"),sQuery(id+"F0.wireOp",EDGE,"E166"),sQuery(id+"F0.wireOp",EDGE,"E167"),sQuery(id+"F0.wireOp",EDGE,"E168"),sQuery(id+"F0.wireOp",EDGE,"E169"),sQuery(id+"F0.wireOp",EDGE,"E170"),sQuery(id+"F0.wireOp",EDGE,"E171"),sQuery(id+"F0.wireOp",EDGE,"E172"),sQuery(id+"F0.wireOp",EDGE,"E173"),sQuery(id+"F0.wireOp",EDGE,"E174"),sQuery(id+"F0.wireOp",EDGE,"E175"),sQuery(id+"F0.wireOp",EDGE,"E176"),sQuery(id+"F0.wireOp",EDGE,"E177"),sQuery(id+"F0.wireOp",EDGE,"E178"),sQuery(id+"F0.wireOp",EDGE,"E179"),sQuery(id+"F0.wireOp",EDGE,"E180"),sQuery(id+"F0.wireOp",EDGE,"E181"),sQuery(id+"F0.wireOp",EDGE,"E182"),sQuery(id+"F0.wireOp",EDGE,"E183"),sQuery(id+"F0.wireOp",EDGE,"E184"),sQuery(id+"F0.wireOp",EDGE,"E185"),sQuery(id+"F0.wireOp",EDGE,"E186"),sQuery(id+"F0.wireOp",EDGE,"E187"),sQuery(id+"F0.wireOp",EDGE,"E188"),sQuery(id+"F0.wireOp",EDGE,"E189"),sQuery(id+"F0.wireOp",EDGE,"E190"),sQuery(id+"F0.wireOp",EDGE,"E191"),sQuery(id+"F0.wireOp",EDGE,"E192"),sQuery(id+"F0.wireOp",EDGE,"E193"),sQuery(id+"F0.wireOp",EDGE,"E194"),sQuery(id+"F0.wireOp",EDGE,"E195"),sQuery(id+"F0.wireOp",EDGE,"E196"),sQuery(id+"F0.wireOp",EDGE,"E197"),sQuery(id+"F0.wireOp",EDGE,"E198"),sQuery(id+"F0.wireOp",EDGE,"E199"),sQuery(id+"F0.wireOp",EDGE,"E200"),sQuery(id+"F0.wireOp",EDGE,"E201"),sQuery(id+"F0.wireOp",EDGE,"E202"),sQuery(id+"F0.wireOp",EDGE,"E203"),sQuery(id+"F0.wireOp",EDGE,"E204"),sQuery(id+"F0.wireOp",EDGE,"E205"),sQuery(id+"F0.wireOp",EDGE,"E206"),sQuery(id+"F0.wireOp",EDGE,"E207"),sQuery(id+"F0.wireOp",EDGE,"E208"),sQuery(id+"F0.wireOp",EDGE,"E209"),sQuery(id+"F0.wireOp",EDGE,"E210"),sQuery(id+"F0.wireOp",EDGE,"E211"),sQuery(id+"F0.wireOp",EDGE,"E212"),sQuery(id+"F0.wireOp",EDGE,"E213"),sQuery(id+"F0.wireOp",EDGE,"E214"),sQuery(id+"F0.wireOp",EDGE,"E215"),sQuery(id+"F0.wireOp",EDGE,"E216"),sQuery(id+"F0.wireOp",EDGE,"E217"),sQuery(id+"F0.wireOp",EDGE,"E218"),sQuery(id+"F0.wireOp",EDGE,"E219"),sQuery(id+"F0.wireOp",EDGE,"E220"),sQuery(id+"F0.wireOp",EDGE,"E221"),sQuery(id+"F0.wireOp",EDGE,"E222"),sQuery(id+"F0.wireOp",EDGE,"E223"),sQuery(id+"F0.wireOp",EDGE,"E224"),sQuery(id+"F0.wireOp",EDGE,"E225"),sQuery(id+"F0.wireOp",EDGE,"E226"),sQuery(id+"F0.wireOp",EDGE,"E227"),sQuery(id+"F0.wireOp",EDGE,"E228"),sQuery(id+"F0.wireOp",EDGE,"E229"),sQuery(id+"F0.wireOp",EDGE,"E230"),sQuery(id+"F0.wireOp",EDGE,"E231"),sQuery(id+"F0.wireOp",EDGE,"E232"),sQuery(id+"F0.wireOp",EDGE,"E233"),sQuery(id+"F0.wireOp",EDGE,"E234"),sQuery(id+"F0.wireOp",EDGE,"E235"),sQuery(id+"F0.wireOp",EDGE,"E236"),sQuery(id+"F0.wireOp",EDGE,"E237"),sQuery(id+"F0.wireOp",EDGE,"E238"),sQuery(id+"F0.wireOp",EDGE,"E239"),sQuery(id+"F0.wireOp",EDGE,"E240"),sQuery(id+"F0.wireOp",EDGE,"E241"),sQuery(id+"F0.wireOp",EDGE,"E242"),sQuery(id+"F0.wireOp",EDGE,"E243"),sQuery(id+"F0.wireOp",EDGE,"E244"),sQuery(id+"F0.wireOp",EDGE,"E245"),sQuery(id+"F0.wireOp",EDGE,"E246"),sQuery(id+"F0.wireOp",EDGE,"E247"),sQuery(id+"F0.wireOp",EDGE,"E248"),sQuery(id+"F0.wireOp",EDGE,"E249"),sQuery(id+"F0.wireOp",EDGE,"E250"),sQuery(id+"F0.wireOp",EDGE,"E251"),sQuery(id+"F0.wireOp",EDGE,"E252"),sQuery(id+"F0.wireOp",EDGE,"E253"),sQuery(id+"F0.wireOp",EDGE,"E254"),sQuery(id+"F0.wireOp",EDGE,"E255"),sQuery(id+"F0.wireOp",EDGE,"E256"),sQuery(id+"F0.wireOp",EDGE,"E257"),sQuery(id+"F0.wireOp",EDGE,"E258"),sQuery(id+"F0.wireOp",EDGE,"E259"),sQuery(id+"F0.wireOp",EDGE,"E260"),sQuery(id+"F0.wireOp",EDGE,"E261"),sQuery(id+"F0.wireOp",EDGE,"E262"),sQuery(id+"F0.wireOp",EDGE,"E263"),sQuery(id+"F0.wireOp",EDGE,"E264"),sQuery(id+"F0.wireOp",EDGE,"E265"),sQuery(id+"F0.wireOp",EDGE,"E266"),sQuery(id+"F0.wireOp",EDGE,"E267"),sQuery(id+"F0.wireOp",EDGE,"E268"),sQuery(id+"F0.wireOp",EDGE,"E269"),sQuery(id+"F0.wireOp",EDGE,"E270"),sQuery(id+"F0.wireOp",EDGE,"E271"),sQuery(id+"F0.wireOp",EDGE,"E272"),sQuery(id+"F0.wireOp",EDGE,"E273"),sQuery(id+"F0.wireOp",EDGE,"E274"),sQuery(id+"F0.wireOp",EDGE,"E275"),sQuery(id+"F0.wireOp",EDGE,"E276"),sQuery(id+"F0.wireOp",EDGE,"E277"),sQuery(id+"F0.wireOp",EDGE,"E278"),sQuery(id+"F0.wireOp",EDGE,"E279"),sQuery(id+"F0.wireOp",EDGE,"E280"),sQuery(id+"F0.wireOp",EDGE,"E281"),sQuery(id+"F0.wireOp",EDGE,"E282"),sQuery(id+"F0.wireOp",EDGE,"E283"),sQuery(id+"F0.wireOp",EDGE,"E284"),sQuery(id+"F0.wireOp",EDGE,"E285"),sQuery(id+"F0.wireOp",EDGE,"E286"),sQuery(id+"F0.wireOp",EDGE,"E287"),sQuery(id+"F0.wireOp",EDGE,"E288"),sQuery(id+"F0.wireOp",EDGE,"E289"),sQuery(id+"F0.wireOp",EDGE,"E290"),sQuery(id+"F0.wireOp",EDGE,"E291"),sQuery(id+"F0.wireOp",EDGE,"E292"),sQuery(id+"F0.wireOp",EDGE,"E293"),sQuery(id+"F0.wireOp",EDGE,"E294"),sQuery(id+"F0.wireOp",EDGE,"E295"),sQuery(id+"F0.wireOp",EDGE,"E296"),sQuery(id+"F0.wireOp",EDGE,"E297"),sQuery(id+"F0.wireOp",EDGE,"E298"),sQuery(id+"F0.wireOp",EDGE,"E299"),sQuery(id+"F0.wireOp",EDGE,"E300"),sQuery(id+"F0.wireOp",EDGE,"E301"),sQuery(id+"F0.wireOp",EDGE,"E302"),sQuery(id+"F0.wireOp",EDGE,"E303"),sQuery(id+"F0.wireOp",EDGE,"E304"),sQuery(id+"F0.wireOp",EDGE,"E305"),sQuery(id+"F0.wireOp",EDGE,"E306"),sQuery(id+"F0.wireOp",EDGE,"E307"),sQuery(id+"F0.wireOp",EDGE,"E308"),sQuery(id+"F0.wireOp",EDGE,"E309"),sQuery(id+"F0.wireOp",EDGE,"E310"),sQuery(id+"F0.wireOp",EDGE,"E311"),sQuery(id+"F0.wireOp",EDGE,"E312"),sQuery(id+"F0.wireOp",EDGE,"E313"),sQuery(id+"F0.wireOp",EDGE,"E314"),sQuery(id+"F0.wireOp",EDGE,"E315"),sQuery(id+"F0.wireOp",EDGE,"E316"),sQuery(id+"F0.wireOp",EDGE,"E317"),sQuery(id+"F0.wireOp",EDGE,"E318"),sQuery(id+"F0.wireOp",EDGE,"E319"),sQuery(id+"F0.wireOp",EDGE,"E320"),sQuery(id+"F0.wireOp",EDGE,"E321"),sQuery(id+"F0.wireOp",EDGE,"E322"),sQuery(id+"F0.wireOp",EDGE,"E323"),sQuery(id+"F0.wireOp",EDGE,"E324"),sQuery(id+"F0.wireOp",EDGE,"E325"),sQuery(id+"F0.wireOp",EDGE,"E326"),sQuery(id+"F0.wireOp",EDGE,"E327"),sQuery(id+"F0.wireOp",EDGE,"E328"),sQuery(id+"F0.wireOp",EDGE,"E329"),sQuery(id+"F0.wireOp",EDGE,"E330"),sQuery(id+"F0.wireOp",EDGE,"E331"),sQuery(id+"F0.wireOp",EDGE,"E332"),sQuery(id+"F0.wireOp",EDGE,"E333"),sQuery(id+"F0.wireOp",EDGE,"E334"),sQuery(id+"F0.wireOp",EDGE,"E335"),sQuery(id+"F0.wireOp",EDGE,"E336"),sQuery(id+"F0.wireOp",EDGE,"E337"),sQuery(id+"F0.wireOp",EDGE,"E338"),sQuery(id+"F0.wireOp",EDGE,"E339"),sQuery(id+"F0.wireOp",EDGE,"E340"),sQuery(id+"F0.wireOp",EDGE,"E341"),sQuery(id+"F0.wireOp",EDGE,"E342"),sQuery(id+"F0.wireOp",EDGE,"E343"),sQuery(id+"F0.wireOp",EDGE,"E344"),sQuery(id+"F0.wireOp",EDGE,"E345"),sQuery(id+"F0.wireOp",EDGE,"E346"),sQuery(id+"F0.wireOp",EDGE,"E347"),sQuery(id+"F0.wireOp",EDGE,"E348"),sQuery(id+"F0.wireOp",EDGE,"E349"),sQuery(id+"F0.wireOp",EDGE,"E350"),sQuery(id+"F0.wireOp",EDGE,"E351"),sQuery(id+"F0.wireOp",EDGE,"E352"),sQuery(id+"F0.wireOp",EDGE,"E353"),sQuery(id+"F0.wireOp",EDGE,"E354"),sQuery(id+"F0.wireOp",EDGE,"E355"),sQuery(id+"F0.wireOp",EDGE,"E356"),sQuery(id+"F0.wireOp",EDGE,"E357"),sQuery(id+"F0.wireOp",EDGE,"E358"),sQuery(id+"F0.wireOp",EDGE,"E359"),sQuery(id+"F0.wireOp",EDGE,"E360"),sQuery(id+"F0.wireOp",EDGE,"E361"),sQuery(id+"F0.wireOp",EDGE,"E362"),sQuery(id+"F0.wireOp",EDGE,"E363"),sQuery(id+"F0.wireOp",EDGE,"E364"),sQuery(id+"F0.wireOp",EDGE,"E365"),sQuery(id+"F0.wireOp",EDGE,"E366"),sQuery(id+"F0.wireOp",EDGE,"E367"),sQuery(id+"F0.wireOp",EDGE,"E368"),sQuery(id+"F0.wireOp",EDGE,"E369"),sQuery(id+"F0.wireOp",EDGE,"E370"),sQuery(id+"F0.wireOp",EDGE,"E371"),sQuery(id+"F0.wireOp",EDGE,"E372"),sQuery(id+"F0.wireOp",EDGE,"E373"),sQuery(id+"F0.wireOp",EDGE,"E374"),sQuery(id+"F0.wireOp",EDGE,"E375"),sQuery(id+"F0.wireOp",EDGE,"E376"),sQuery(id+"F0.wireOp",EDGE,"E377"),sQuery(id+"F0.wireOp",EDGE,"E378"),sQuery(id+"F0.wireOp",EDGE,"E379"),sQuery(id+"F0.wireOp",EDGE,"E380"),sQuery(id+"F0.wireOp",EDGE,"E381"),sQuery(id+"F0.wireOp",EDGE,"E382"),sQuery(id+"F0.wireOp",EDGE,"E383"),sQuery(id+"F0.wireOp",EDGE,"E384"),sQuery(id+"F0.wireOp",EDGE,"E385"),sQuery(id+"F0.wireOp",EDGE,"E386"),sQuery(id+"F0.wireOp",EDGE,"E387"),sQuery(id+"F0.wireOp",EDGE,"E388"),sQuery(id+"F0.wireOp",EDGE,"E389"),sQuery(id+"F0.wireOp",EDGE,"E390"),sQuery(id+"F0.wireOp",EDGE,"E391"),sQuery(id+"F0.wireOp",EDGE,"E392"),sQuery(id+"F0.wireOp",EDGE,"E393"),sQuery(id+"F0.wireOp",EDGE,"E394"),sQuery(id+"F0.wireOp",EDGE,"E395"),sQuery(id+"F0.wireOp",EDGE,"E396"),sQuery(id+"F0.wireOp",EDGE,"E397"),sQuery(id+"F0.wireOp",EDGE,"E398"),sQuery(id+"F0.wireOp",EDGE,"E399"),sQuery(id+"F0.wireOp",EDGE,"E400"),sQuery(id+"F0.wireOp",EDGE,"E401"),sQuery(id+"F0.wireOp",EDGE,"E402"),sQuery(id+"F0.wireOp",EDGE,"E403"),sQuery(id+"F0.wireOp",EDGE,"E404"),sQuery(id+"F0.wireOp",EDGE,"E405"),sQuery(id+"F0.wireOp",EDGE,"E406"),sQuery(id+"F0.wireOp",EDGE,"E407"),sQuery(id+"F0.wireOp",EDGE,"E408"),sQuery(id+"F0.wireOp",EDGE,"E409"),sQuery(id+"F0.wireOp",EDGE,"E410"),sQuery(id+"F0.wireOp",EDGE,"E411"),sQuery(id+"F0.wireOp",EDGE,"E412"),sQuery(id+"F0.wireOp",EDGE,"E413"),sQuery(id+"F0.wireOp",EDGE,"E414"),sQuery(id+"F0.wireOp",EDGE,"E415"),sQuery(id+"F0.wireOp",EDGE,"E416"),sQuery(id+"F0.wireOp",EDGE,"E417"),sQuery(id+"F0.wireOp",EDGE,"E418"),sQuery(id+"F0.wireOp",EDGE,"E419"),sQuery(id+"F0.wireOp",EDGE,"E420"),sQuery(id+"F0.wireOp",EDGE,"E421"),sQuery(id+"F0.wireOp",EDGE,"E422"),sQuery(id+"F0.wireOp",EDGE,"E423"),sQuery(id+"F0.wireOp",EDGE,"E424"),sQuery(id+"F0.wireOp",EDGE,"E425"),sQuery(id+"F0.wireOp",EDGE,"E426"),sQuery(id+"F0.wireOp",EDGE,"E427"),sQuery(id+"F0.wireOp",EDGE,"E428"),sQuery(id+"F0.wireOp",EDGE,"E429"),sQuery(id+"F0.wireOp",EDGE,"E430"),sQuery(id+"F0.wireOp",EDGE,"E431"),sQuery(id+"F0.wireOp",EDGE,"E432"),sQuery(id+"F0.wireOp",EDGE,"E433"),sQuery(id+"F0.wireOp",EDGE,"E434"),sQuery(id+"F0.wireOp",EDGE,"E435"),sQuery(id+"F0.wireOp",EDGE,"E436"),sQuery(id+"F0.wireOp",EDGE,"E437"),sQuery(id+"F0.wireOp",EDGE,"E438"),sQuery(id+"F0.wireOp",EDGE,"E439"),sQuery(id+"F0.wireOp",EDGE,"E440"),sQuery(id+"F0.wireOp",EDGE,"E441"),sQuery(id+"F0.wireOp",EDGE,"E442"),sQuery(id+"F0.wireOp",EDGE,"E443"),sQuery(id+"F0.wireOp",EDGE,"E444"),sQuery(id+"F0.wireOp",EDGE,"E445"),sQuery(id+"F0.wireOp",EDGE,"E446"),sQuery(id+"F0.wireOp",EDGE,"E447"),sQuery(id+"F0.wireOp",EDGE,"E448"),sQuery(id+"F0.wireOp",EDGE,"E449"),sQuery(id+"F0.wireOp",EDGE,"E450"),sQuery(id+"F0.wireOp",EDGE,"E451"),sQuery(id+"F0.wireOp",EDGE,"E452"),sQuery(id+"F0.wireOp",EDGE,"E453"),sQuery(id+"F0.wireOp",EDGE,"E454"),sQuery(id+"F0.wireOp",EDGE,"E455"),sQuery(id+"F0.wireOp",EDGE,"E456"),sQuery(id+"F0.wireOp",EDGE,"E457"),sQuery(id+"F0.wireOp",EDGE,"E458"),sQuery(id+"F0.wireOp",EDGE,"E459"),sQuery(id+"F0.wireOp",EDGE,"E460"),sQuery(id+"F0.wireOp",EDGE,"E461"),sQuery(id+"F0.wireOp",EDGE,"E462"),sQuery(id+"F0.wireOp",EDGE,"E463"),sQuery(id+"F0.wireOp",EDGE,"E464"),sQuery(id+"F0.wireOp",EDGE,"E465"),sQuery(id+"F0.wireOp",EDGE,"E466"),sQuery(id+"F0.wireOp",EDGE,"E467"),sQuery(id+"F0.wireOp",EDGE,"E468"),sQuery(id+"F0.wireOp",EDGE,"E469"),sQuery(id+"F0.wireOp",EDGE,"E470"),sQuery(id+"F0.wireOp",EDGE,"E471"),sQuery(id+"F0.wireOp",EDGE,"E472"),sQuery(id+"F0.wireOp",EDGE,"E473"),sQuery(id+"F0.wireOp",EDGE,"E474"),sQuery(id+"F0.wireOp",EDGE,"E475"),sQuery(id+"F0.wireOp",EDGE,"E476"),sQuery(id+"F0.wireOp",EDGE,"E477"),sQuery(id+"F0.wireOp",EDGE,"E478"),sQuery(id+"F0.wireOp",EDGE,"E479"),sQuery(id+"F0.wireOp",EDGE,"E480"),sQuery(id+"F0.wireOp",EDGE,"E481"),sQuery(id+"F0.wireOp",EDGE,"E482"),sQuery(id+"F0.wireOp",EDGE,"E483"),sQuery(id+"F0.wireOp",EDGE,"E484"),sQuery(id+"F0.wireOp",EDGE,"E485"),sQuery(id+"F0.wireOp",EDGE,"E486"),sQuery(id+"F0.wireOp",EDGE,"E487"),sQuery(id+"F0.wireOp",EDGE,"E488"),sQuery(id+"F0.wireOp",EDGE,"E489"),sQuery(id+"F0.wireOp",EDGE,"E490"),sQuery(id+"F0.wireOp",EDGE,"E491"),sQuery(id+"F0.wireOp",EDGE,"E492"),sQuery(id+"F0.wireOp",EDGE,"E493"),sQuery(id+"F0.wireOp",EDGE,"E494"),sQuery(id+"F0.wireOp",EDGE,"E495"),sQuery(id+"F0.wireOp",EDGE,"E496"),sQuery(id+"F0.wireOp",EDGE,"E497"),sQuery(id+"F0.wireOp",EDGE,"E498"),sQuery(id+"F0.wireOp",EDGE,"E499"),sQuery(id+"F0.wireOp",EDGE,"E500"),sQuery(id+"F0.wireOp",EDGE,"E501"),sQuery(id+"F0.wireOp",EDGE,"E502"),sQuery(id+"F0.wireOp",EDGE,"E503"),sQuery(id+"F0.wireOp",EDGE,"E504"),sQuery(id+"F0.wireOp",EDGE,"E505"),sQuery(id+"F0.wireOp",EDGE,"E506"),sQuery(id+"F0.wireOp",EDGE,"E507"),sQuery(id+"F0.wireOp",EDGE,"E508"),sQuery(id+"F0.wireOp",EDGE,"E509"),sQuery(id+"F0.wireOp",EDGE,"E510"),sQuery(id+"F0.wireOp",EDGE,"E511"),sQuery(id+"F0.wireOp",EDGE,"E512"),sQuery(id+"F0.wireOp",EDGE,"E513"),sQuery(id+"F0.wireOp",EDGE,"E514"),sQuery(id+"F0.wireOp",EDGE,"E515"),sQuery(id+"F0.wireOp",EDGE,"E516"),sQuery(id+"F0.wireOp",EDGE,"E517"),sQuery(id+"F0.wireOp",EDGE,"E518"),sQuery(id+"F0.wireOp",EDGE,"E519"),sQuery(id+"F0.wireOp",EDGE,"E520"),sQuery(id+"F0.wireOp",EDGE,"E521"),sQuery(id+"F0.wireOp",EDGE,"E522"),sQuery(id+"F0.wireOp",EDGE,"E523"),sQuery(id+"F0.wireOp",EDGE,"E524"),sQuery(id+"F0.wireOp",EDGE,"E525"),sQuery(id+"F0.wireOp",EDGE,"E526"),sQuery(id+"F0.wireOp",EDGE,"E527"),sQuery(id+"F0.wireOp",EDGE,"E528"),sQuery(id+"F0.wireOp",EDGE,"E529"),sQuery(id+"F0.wireOp",EDGE,"E530"),sQuery(id+"F0.wireOp",EDGE,"E531"),sQuery(id+"F0.wireOp",EDGE,"E532"),sQuery(id+"F0.wireOp",EDGE,"E533"),sQuery(id+"F0.wireOp",EDGE,"E534"),sQuery(id+"F0.wireOp",EDGE,"E535"),sQuery(id+"F0.wireOp",EDGE,"E536"),sQuery(id+"F0.wireOp",EDGE,"E537"),sQuery(id+"F0.wireOp",EDGE,"E538"),sQuery(id+"F0.wireOp",EDGE,"E539"),sQuery(id+"F0.wireOp",EDGE,"E540"),sQuery(id+"F0.wireOp",EDGE,"E541"),sQuery(id+"F0.wireOp",EDGE,"E542"),sQuery(id+"F0.wireOp",EDGE,"E543"),sQuery(id+"F0.wireOp",EDGE,"E544"),sQuery(id+"F0.wireOp",EDGE,"E545"),sQuery(id+"F0.wireOp",EDGE,"E546"),sQuery(id+"F0.wireOp",EDGE,"E547"),sQuery(id+"F0.wireOp",EDGE,"E548"),sQuery(id+"F0.wireOp",EDGE,"E549"),sQuery(id+"F0.wireOp",EDGE,"E550"),sQuery(id+"F0.wireOp",EDGE,"E551"),sQuery(id+"F0.wireOp",EDGE,"E552"),sQuery(id+"F0.wireOp",EDGE,"E553"),sQuery(id+"F0.wireOp",EDGE,"E554"),sQuery(id+"F0.wireOp",EDGE,"E555"),sQuery(id+"F0.wireOp",EDGE,"E556"),sQuery(id+"F0.wireOp",EDGE,"E557"),sQuery(id+"F0.wireOp",EDGE,"E558"),sQuery(id+"F0.wireOp",EDGE,"E559"),sQuery(id+"F0.wireOp",EDGE,"E560"),sQuery(id+"F0.wireOp",EDGE,"E561"),sQuery(id+"F0.wireOp",EDGE,"E562"),sQuery(id+"F0.wireOp",EDGE,"E563"),sQuery(id+"F0.wireOp",EDGE,"E564"),sQuery(id+"F0.wireOp",EDGE,"E565"),sQuery(id+"F0.wireOp",EDGE,"E566"),sQuery(id+"F0.wireOp",EDGE,"E567"),sQuery(id+"F0.wireOp",EDGE,"E568"),sQuery(id+"F0.wireOp",EDGE,"E569"),sQuery(id+"F0.wireOp",EDGE,"E570"),sQuery(id+"F0.wireOp",EDGE,"E571"),sQuery(id+"F0.wireOp",EDGE,"E572"),sQuery(id+"F0.wireOp",EDGE,"E573"),sQuery(id+"F0.wireOp",EDGE,"E574"),sQuery(id+"F0.wireOp",EDGE,"E575"),sQuery(id+"F0.wireOp",EDGE,"E576"),sQuery(id+"F0.wireOp",EDGE,"E577"),sQuery(id+"F0.wireOp",EDGE,"E578"),sQuery(id+"F0.wireOp",EDGE,"E579"),sQuery(id+"F0.wireOp",EDGE,"E580"),sQuery(id+"F0.wireOp",EDGE,"E581"),sQuery(id+"F0.wireOp",EDGE,"E582"),sQuery(id+"F0.wireOp",EDGE,"E583"),sQuery(id+"F0.wireOp",EDGE,"E584"),sQuery(id+"F0.wireOp",EDGE,"E585"),sQuery(id+"F0.wireOp",EDGE,"E586"),sQuery(id+"F0.wireOp",EDGE,"E587"),sQuery(id+"F0.wireOp",EDGE,"E588"),sQuery(id+"F0.wireOp",EDGE,"E589"),sQuery(id+"F0.wireOp",EDGE,"E590"),sQuery(id+"F0.wireOp",EDGE,"E591"),sQuery(id+"F0.wireOp",EDGE,"E592"),sQuery(id+"F0.wireOp",EDGE,"E593"),sQuery(id+"F0.wireOp",EDGE,"E594"),sQuery(id+"F0.wireOp",EDGE,"E595"),sQuery(id+"F0.wireOp",EDGE,"E596"),sQuery(id+"F0.wireOp",EDGE,"E597"),sQuery(id+"F0.wireOp",EDGE,"E598"),sQuery(id+"F0.wireOp",EDGE,"E599"),sQuery(id+"F0.wireOp",EDGE,"E600"),sQuery(id+"F0.wireOp",EDGE,"E601"),sQuery(id+"F0.wireOp",EDGE,"E602"),sQuery(id+"F0.wireOp",EDGE,"E603"),sQuery(id+"F0.wireOp",EDGE,"E604"),sQuery(id+"F0.wireOp",EDGE,"E605"),sQuery(id+"F0.wireOp",EDGE,"E606"),sQuery(id+"F0.wireOp",EDGE,"E607"),sQuery(id+"F0.wireOp",EDGE,"E608"),sQuery(id+"F0.wireOp",EDGE,"E609"),sQuery(id+"F0.wireOp",EDGE,"E610"),sQuery(id+"F0.wireOp",EDGE,"E611"),sQuery(id+"F0.wireOp",EDGE,"E612"),sQuery(id+"F0.wireOp",EDGE,"E613"),sQuery(id+"F0.wireOp",EDGE,"E614"),sQuery(id+"F0.wireOp",EDGE,"E615"),sQuery(id+"F0.wireOp",EDGE,"E616"),sQuery(id+"F0.wireOp",EDGE,"E617"),sQuery(id+"F0.wireOp",EDGE,"E618"),sQuery(id+"F0.wireOp",EDGE,"E619"),sQuery(id+"F0.wireOp",EDGE,"E620"),sQuery(id+"F0.wireOp",EDGE,"E621"),sQuery(id+"F0.wireOp",EDGE,"E622"),sQuery(id+"F0.wireOp",EDGE,"E623"),sQuery(id+"F0.wireOp",EDGE,"E624"),sQuery(id+"F0.wireOp",EDGE,"E625"),sQuery(id+"F0.wireOp",EDGE,"E626"),sQuery(id+"F0.wireOp",EDGE,"E627"),sQuery(id+"F0.wireOp",EDGE,"E628"),sQuery(id+"F0.wireOp",EDGE,"E629"),sQuery(id+"F0.wireOp",EDGE,"E630"),sQuery(id+"F0.wireOp",EDGE,"E631"),sQuery(id+"F0.wireOp",EDGE,"E632"),sQuery(id+"F0.wireOp",EDGE,"E633"),sQuery(id+"F0.wireOp",EDGE,"E634"),sQuery(id+"F0.wireOp",EDGE,"E635"),sQuery(id+"F0.wireOp",EDGE,"E636"),sQuery(id+"F0.wireOp",EDGE,"E637"),sQuery(id+"F0.wireOp",EDGE,"E638"),sQuery(id+"F0.wireOp",EDGE,"E639"),sQuery(id+"F0.wireOp",EDGE,"E640"),sQuery(id+"F0.wireOp",EDGE,"E641"),sQuery(id+"F0.wireOp",EDGE,"E642"),sQuery(id+"F0.wireOp",EDGE,"E643"),sQuery(id+"F0.wireOp",EDGE,"E644"),sQuery(id+"F0.wireOp",EDGE,"E645"),sQuery(id+"F0.wireOp",EDGE,"E646"),sQuery(id+"F0.wireOp",EDGE,"E647"),sQuery(id+"F0.wireOp",EDGE,"E648"),sQuery(id+"F0.wireOp",EDGE,"E649"),sQuery(id+"F0.wireOp",EDGE,"E650"),sQuery(id+"F0.wireOp",EDGE,"E651"),sQuery(id+"F0.wireOp",EDGE,"E652"),sQuery(id+"F0.wireOp",EDGE,"E653"),sQuery(id+"F0.wireOp",EDGE,"E654"),sQuery(id+"F0.wireOp",EDGE,"E655"),sQuery(id+"F0.wireOp",EDGE,"E656"),sQuery(id+"F0.wireOp",EDGE,"E657"),sQuery(id+"F0.wireOp",EDGE,"E658"),sQuery(id+"F0.wireOp",EDGE,"E659"),sQuery(id+"F0.wireOp",EDGE,"E660"),sQuery(id+"F0.wireOp",EDGE,"E661"),sQuery(id+"F0.wireOp",EDGE,"E662"),sQuery(id+"F0.wireOp",EDGE,"E663"),sQuery(id+"F0.wireOp",EDGE,"E664"),sQuery(id+"F0.wireOp",EDGE,"E665"),sQuery(id+"F0.wireOp",EDGE,"E666"),sQuery(id+"F0.wireOp",EDGE,"E667"),sQuery(id+"F0.wireOp",EDGE,"E668"),sQuery(id+"F0.wireOp",EDGE,"E669"),sQuery(id+"F0.wireOp",EDGE,"E670"),sQuery(id+"F0.wireOp",EDGE,"E671"),sQuery(id+"F0.wireOp",EDGE,"E672"),sQuery(id+"F0.wireOp",EDGE,"E673"),sQuery(id+"F0.wireOp",EDGE,"E674"),sQuery(id+"F0.wireOp",EDGE,"E675"),sQuery(id+"F0.wireOp",EDGE,"E676"),sQuery(id+"F0.wireOp",EDGE,"E677"),sQuery(id+"F0.wireOp",EDGE,"E678"),sQuery(id+"F0.wireOp",EDGE,"E679"),sQuery(id+"F0.wireOp",EDGE,"E680"),sQuery(id+"F0.wireOp",EDGE,"E681"),sQuery(id+"F0.wireOp",EDGE,"E682"),sQuery(id+"F0.wireOp",EDGE,"E683"),sQuery(id+"F0.wireOp",EDGE,"E684"),sQuery(id+"F0.wireOp",EDGE,"E685"),sQuery(id+"F0.wireOp",EDGE,"E686"),sQuery(id+"F0.wireOp",EDGE,"E687"),sQuery(id+"F0.wireOp",EDGE,"E688"),sQuery(id+"F0.wireOp",EDGE,"E689"),sQuery(id+"F0.wireOp",EDGE,"E690"),sQuery(id+"F0.wireOp",EDGE,"E691"),sQuery(id+"F0.wireOp",EDGE,"E692"),sQuery(id+"F0.wireOp",EDGE,"E693"),sQuery(id+"F0.wireOp",EDGE,"E694"),sQuery(id+"F0.wireOp",EDGE,"E695"),sQuery(id+"F0.wireOp",EDGE,"E696"),sQuery(id+"F0.wireOp",EDGE,"E697"),sQuery(id+"F0.wireOp",EDGE,"E698"),sQuery(id+"F0.wireOp",EDGE,"E699"),sQuery(id+"F0.wireOp",EDGE,"E700"),sQuery(id+"F0.wireOp",EDGE,"E701"),sQuery(id+"F0.wireOp",EDGE,"E702"),sQuery(id+"F0.wireOp",EDGE,"E703"),sQuery(id+"F0.wireOp",EDGE,"E704"),sQuery(id+"F0.wireOp",EDGE,"E705"),sQuery(id+"F0.wireOp",EDGE,"E706"),sQuery(id+"F0.wireOp",EDGE,"E707"),sQuery(id+"F0.wireOp",EDGE,"E708"),sQuery(id+"F0.wireOp",EDGE,"E709"),sQuery(id+"F0.wireOp",EDGE,"E710"),sQuery(id+"F0.wireOp",EDGE,"E711"),sQuery(id+"F0.wireOp",EDGE,"E712"),sQuery(id+"F0.wireOp",EDGE,"E713"),sQuery(id+"F0.wireOp",EDGE,"E714"),sQuery(id+"F0.wireOp",EDGE,"E715"),sQuery(id+"F0.wireOp",EDGE,"E716"),sQuery(id+"F0.wireOp",EDGE,"E717"),sQuery(id+"F0.wireOp",EDGE,"E718"),sQuery(id+"F0.wireOp",EDGE,"E719"),sQuery(id+"F0.wireOp",EDGE,"E720"),sQuery(id+"F0.wireOp",EDGE,"E721"),sQuery(id+"F0.wireOp",EDGE,"E722"),sQuery(id+"F0.wireOp",EDGE,"E723"),sQuery(id+"F0.wireOp",EDGE,"E724"),sQuery(id+"F0.wireOp",EDGE,"E725"),sQuery(id+"F0.wireOp",EDGE,"E726"),sQuery(id+"F0.wireOp",EDGE,"E727"),sQuery(id+"F0.wireOp",EDGE,"E728"),sQuery(id+"F0.wireOp",EDGE,"E729"),sQuery(id+"F0.wireOp",EDGE,"E730"),sQuery(id+"F0.wireOp",EDGE,"E731"),sQuery(id+"F0.wireOp",EDGE,"E732"),sQuery(id+"F0.wireOp",EDGE,"E733"),sQuery(id+"F0.wireOp",EDGE,"E734"),sQuery(id+"F0.wireOp",EDGE,"E735"),sQuery(id+"F0.wireOp",EDGE,"E736"),sQuery(id+"F0.wireOp",EDGE,"E737"),sQuery(id+"F0.wireOp",EDGE,"E738"),sQuery(id+"F0.wireOp",EDGE,"E739"),sQuery(id+"F0.wireOp",EDGE,"E740"),sQuery(id+"F0.wireOp",EDGE,"E741"),sQuery(id+"F0.wireOp",EDGE,"E742"),sQuery(id+"F0.wireOp",EDGE,"E743"),sQuery(id+"F0.wireOp",EDGE,"E744"),sQuery(id+"F0.wireOp",EDGE,"E745"),sQuery(id+"F0.wireOp",EDGE,"E746"),sQuery(id+"F0.wireOp",EDGE,"E747"),sQuery(id+"F0.wireOp",EDGE,"E748"),sQuery(id+"F0.wireOp",EDGE,"E749"),sQuery(id+"F0.wireOp",EDGE,"E750"),sQuery(id+"F0.wireOp",EDGE,"E751"),sQuery(id+"F0.wireOp",EDGE,"E752"),sQuery(id+"F0.wireOp",EDGE,"E753"),sQuery(id+"F0.wireOp",EDGE,"E754"),sQuery(id+"F0.wireOp",EDGE,"E755"),sQuery(id+"F0.wireOp",EDGE,"E756"),sQuery(id+"F0.wireOp",EDGE,"E757"),sQuery(id+"F0.wireOp",EDGE,"E758"),sQuery(id+"F0.wireOp",EDGE,"E759"),sQuery(id+"F0.wireOp",EDGE,"E760"),sQuery(id+"F0.wireOp",EDGE,"E761"),sQuery(id+"F0.wireOp",EDGE,"E762"),sQuery(id+"F0.wireOp",EDGE,"E763"),sQuery(id+"F0.wireOp",EDGE,"E764"),sQuery(id+"F0.wireOp",EDGE,"E765"),sQuery(id+"F0.wireOp",EDGE,"E766"),sQuery(id+"F0.wireOp",EDGE,"E767"),sQuery(id+"F0.wireOp",EDGE,"E768"),sQuery(id+"F0.wireOp",EDGE,"E769"),sQuery(id+"F0.wireOp",EDGE,"E770"),sQuery(id+"F0.wireOp",EDGE,"E771"),sQuery(id+"F0.wireOp",EDGE,"E772"),sQuery(id+"F0.wireOp",EDGE,"E773"),sQuery(id+"F0.wireOp",EDGE,"E774"),sQuery(id+"F0.wireOp",EDGE,"E775"),sQuery(id+"F0.wireOp",EDGE,"E776"),sQuery(id+"F0.wireOp",EDGE,"E777"),sQuery(id+"F0.wireOp",EDGE,"E778"),sQuery(id+"F0.wireOp",EDGE,"E779"),sQuery(id+"F0.wireOp",EDGE,"E780"),sQuery(id+"F0.wireOp",EDGE,"E781"),sQuery(id+"F0.wireOp",EDGE,"E782"),sQuery(id+"F0.wireOp",EDGE,"E783"),sQuery(id+"F0.wireOp",EDGE,"E784"),sQuery(id+"F0.wireOp",EDGE,"E785"),sQuery(id+"F0.wireOp",EDGE,"E786"),sQuery(id+"F0.wireOp",EDGE,"E787"),sQuery(id+"F0.wireOp",EDGE,"E788"),sQuery(id+"F0.wireOp",EDGE,"E789"),sQuery(id+"F0.wireOp",EDGE,"E790"),sQuery(id+"F0.wireOp",EDGE,"E791"),sQuery(id+"F0.wireOp",EDGE,"E792"),sQuery(id+"F0.wireOp",EDGE,"E793"),sQuery(id+"F0.wireOp",EDGE,"E794"),sQuery(id+"F0.wireOp",EDGE,"E795"),sQuery(id+"F0.wireOp",EDGE,"E796"),sQuery(id+"F0.wireOp",EDGE,"E797"),sQuery(id+"F0.wireOp",EDGE,"E798"),sQuery(id+"F0.wireOp",EDGE,"E799"),sQuery(id+"F0.wireOp",EDGE,"E800"),sQuery(id+"F0.wireOp",EDGE,"E801"),sQuery(id+"F0.wireOp",EDGE,"E802"),sQuery(id+"F0.wireOp",EDGE,"E803"),sQuery(id+"F0.wireOp",EDGE,"E804"),sQuery(id+"F0.wireOp",EDGE,"E805"),sQuery(id+"F0.wireOp",EDGE,"E806"),sQuery(id+"F0.wireOp",EDGE,"E807"),sQuery(id+"F0.wireOp",EDGE,"E808"),sQuery(id+"F0.wireOp",EDGE,"E809"),sQuery(id+"F0.wireOp",EDGE,"E810"),sQuery(id+"F0.wireOp",EDGE,"E811"),sQuery(id+"F0.wireOp",EDGE,"E812"),sQuery(id+"F0.wireOp",EDGE,"E813"),sQuery(id+"F0.wireOp",EDGE,"E814"),sQuery(id+"F0.wireOp",EDGE,"E815"),sQuery(id+"F0.wireOp",EDGE,"E816"),sQuery(id+"F0.wireOp",EDGE,"E817"),sQuery(id+"F0.wireOp",EDGE,"E818"),sQuery(id+"F0.wireOp",EDGE,"E819"),sQuery(id+"F0.wireOp",EDGE,"E820"),sQuery(id+"F0.wireOp",EDGE,"E821"),sQuery(id+"F0.wireOp",EDGE,"E822"),sQuery(id+"F0.wireOp",EDGE,"E823"),sQuery(id+"F0.wireOp",EDGE,"E824"),sQuery(id+"F0.wireOp",EDGE,"E825"),sQuery(id+"F0.wireOp",EDGE,"E826"),sQuery(id+"F0.wireOp",EDGE,"E827"),sQuery(id+"F0.wireOp",EDGE,"E828"),sQuery(id+"F0.wireOp",EDGE,"E829"),sQuery(id+"F0.wireOp",EDGE,"E830"),sQuery(id+"F0.wireOp",EDGE,"E831"),sQuery(id+"F0.wireOp",EDGE,"E832"),sQuery(id+"F0.wireOp",EDGE,"E833"),sQuery(id+"F0.wireOp",EDGE,"E834"),sQuery(id+"F0.wireOp",EDGE,"E835"),sQuery(id+"F0.wireOp",EDGE,"E836"),sQuery(id+"F0.wireOp",EDGE,"E837"),sQuery(id+"F0.wireOp",EDGE,"E838"),sQuery(id+"F0.wireOp",EDGE,"E839"),sQuery(id+"F0.wireOp",EDGE,"E840"),sQuery(id+"F0.wireOp",EDGE,"E841"),sQuery(id+"F0.wireOp",EDGE,"E842"),sQuery(id+"F0.wireOp",EDGE,"E843"),sQuery(id+"F0.wireOp",EDGE,"E844"),sQuery(id+"F0.wireOp",EDGE,"E845"),sQuery(id+"F0.wireOp",EDGE,"E846"),sQuery(id+"F0.wireOp",EDGE,"E847"),sQuery(id+"F0.wireOp",EDGE,"E848"),sQuery(id+"F0.wireOp",EDGE,"E849"),sQuery(id+"F0.wireOp",EDGE,"E850"),sQuery(id+"F0.wireOp",EDGE,"E851"),sQuery(id+"F0.wireOp",EDGE,"E852"),sQuery(id+"F0.wireOp",EDGE,"E853"),sQuery(id+"F0.wireOp",EDGE,"E854"),sQuery(id+"F0.wireOp",EDGE,"E855"),sQuery(id+"F0.wireOp",EDGE,"E856"),sQuery(id+"F0.wireOp",EDGE,"E857"),sQuery(id+"F0.wireOp",EDGE,"E858"),sQuery(id+"F0.wireOp",EDGE,"E859"),sQuery(id+"F0.wireOp",EDGE,"E860"),sQuery(id+"F0.wireOp",EDGE,"E861"),sQuery(id+"F0.wireOp",EDGE,"E862"),sQuery(id+"F0.wireOp",EDGE,"E863"),sQuery(id+"F0.wireOp",EDGE,"E864"),sQuery(id+"F0.wireOp",EDGE,"E865"),sQuery(id+"F0.wireOp",EDGE,"E866"),sQuery(id+"F0.wireOp",EDGE,"E867"),sQuery(id+"F0.wireOp",EDGE,"E868"),sQuery(id+"F0.wireOp",EDGE,"E869"),sQuery(id+"F0.wireOp",EDGE,"E870"),sQuery(id+"F0.wireOp",EDGE,"E871"),sQuery(id+"F0.wireOp",EDGE,"E872"),sQuery(id+"F0.wireOp",EDGE,"E873"),sQuery(id+"F0.wireOp",EDGE,"E874"),sQuery(id+"F0.wireOp",EDGE,"E875"),sQuery(id+"F0.wireOp",EDGE,"E876"),sQuery(id+"F0.wireOp",EDGE,"E877"),sQuery(id+"F0.wireOp",EDGE,"E878"),sQuery(id+"F0.wireOp",EDGE,"E879"),sQuery(id+"F0.wireOp",EDGE,"E880"),sQuery(id+"F0.wireOp",EDGE,"E881"),sQuery(id+"F0.wireOp",EDGE,"E882"),sQuery(id+"F0.wireOp",EDGE,"E883"),sQuery(id+"F0.wireOp",EDGE,"E884"),sQuery(id+"F0.wireOp",EDGE,"E885"),sQuery(id+"F0.wireOp",EDGE,"E886"),sQuery(id+"F0.wireOp",EDGE,"E887"),sQuery(id+"F0.wireOp",EDGE,"E888"),sQuery(id+"F0.wireOp",EDGE,"E889"),sQuery(id+"F0.wireOp",EDGE,"E890"),sQuery(id+"F0.wireOp",EDGE,"E891"),sQuery(id+"F0.wireOp",EDGE,"E892"),sQuery(id+"F0.wireOp",EDGE,"E893"),sQuery(id+"F0.wireOp",EDGE,"E894"),sQuery(id+"F0.wireOp",EDGE,"E895"),sQuery(id+"F0.wireOp",EDGE,"E896"),sQuery(id+"F0.wireOp",EDGE,"E897"),sQuery(id+"F0.wireOp",EDGE,"E898"),sQuery(id+"F0.wireOp",EDGE,"E899"),sQuery(id+"F0.wireOp",EDGE,"E900"),sQuery(id+"F0.wireOp",EDGE,"E901"),sQuery(id+"F0.wireOp",EDGE,"E902"),sQuery(id+"F0.wireOp",EDGE,"E903"),sQuery(id+"F0.wireOp",EDGE,"E904"),sQuery(id+"F0.wireOp",EDGE,"E905"),sQuery(id+"F0.wireOp",EDGE,"E906"),sQuery(id+"F0.wireOp",EDGE,"E907"),sQuery(id+"F0.wireOp",EDGE,"E908"),sQuery(id+"F0.wireOp",EDGE,"E909"),sQuery(id+"F0.wireOp",EDGE,"E910"),sQuery(id+"F0.wireOp",EDGE,"E911"),sQuery(id+"F0.wireOp",EDGE,"E912"),sQuery(id+"F0.wireOp",EDGE,"E913"),sQuery(id+"F0.wireOp",EDGE,"E914"),sQuery(id+"F0.wireOp",EDGE,"E915"),sQuery(id+"F0.wireOp",EDGE,"E916"),sQuery(id+"F0.wireOp",EDGE,"E917"),sQuery(id+"F0.wireOp",EDGE,"E918"),sQuery(id+"F0.wireOp",EDGE,"E919"),sQuery(id+"F0.wireOp",EDGE,"E920"),sQuery(id+"F0.wireOp",EDGE,"E921"),sQuery(id+"F0.wireOp",EDGE,"E922"),sQuery(id+"F0.wireOp",EDGE,"E923"),sQuery(id+"F0.wireOp",EDGE,"E924"),sQuery(id+"F0.wireOp",EDGE,"E925"),sQuery(id+"F0.wireOp",EDGE,"E926"),sQuery(id+"F0.wireOp",EDGE,"E927"),sQuery(id+"F0.wireOp",EDGE,"E928"),sQuery(id+"F0.wireOp",EDGE,"E929"),sQuery(id+"F0.wireOp",EDGE,"E930"),sQuery(id+"F0.wireOp",EDGE,"E931"),sQuery(id+"F0.wireOp",EDGE,"E932"),sQuery(id+"F0.wireOp",EDGE,"E933"),sQuery(id+"F0.wireOp",EDGE,"E934"),sQuery(id+"F0.wireOp",EDGE,"E935"),sQuery(id+"F0.wireOp",EDGE,"E936"),sQuery(id+"F0.wireOp",EDGE,"E937"),sQuery(id+"F0.wireOp",EDGE,"E938"),sQuery(id+"F0.wireOp",EDGE,"E939"),sQuery(id+"F0.wireOp",EDGE,"E940"),sQuery(id+"F0.wireOp",EDGE,"E941"),sQuery(id+"F0.wireOp",EDGE,"E942"),sQuery(id+"F0.wireOp",EDGE,"E943"),sQuery(id+"F0.wireOp",EDGE,"E944"),sQuery(id+"F0.wireOp",EDGE,"E945"),sQuery(id+"F0.wireOp",EDGE,"E946"),sQuery(id+"F0.wireOp",EDGE,"E947"),sQuery(id+"F0.wireOp",EDGE,"E948"),sQuery(id+"F0.wireOp",EDGE,"E949"),sQuery(id+"F0.wireOp",EDGE,"E950"),sQuery(id+"F0.wireOp",EDGE,"E951"),sQuery(id+"F0.wireOp",EDGE,"E952"),sQuery(id+"F0.wireOp",EDGE,"E953"),sQuery(id+"F0.wireOp",EDGE,"E954"),sQuery(id+"F0.wireOp",EDGE,"E955"),sQuery(id+"F0.wireOp",EDGE,"E956"),sQuery(id+"F0.wireOp",EDGE,"E957"),sQuery(id+"F0.wireOp",EDGE,"E958"),sQuery(id+"F0.wireOp",EDGE,"E959"),sQuery(id+"F0.wireOp",EDGE,"E960"),sQuery(id+"F0.wireOp",EDGE,"E961"),sQuery(id+"F0.wireOp",EDGE,"E962"),sQuery(id+"F0.wireOp",EDGE,"E963"),sQuery(id+"F0.wireOp",EDGE,"E964"),sQuery(id+"F0.wireOp",EDGE,"E965"),sQuery(id+"F0.wireOp",EDGE,"E966"),sQuery(id+"F0.wireOp",EDGE,"E967"),sQuery(id+"F0.wireOp",EDGE,"E968"),sQuery(id+"F0.wireOp",EDGE,"E969"),sQuery(id+"F0.wireOp",EDGE,"E970"),sQuery(id+"F0.wireOp",EDGE,"E971"),sQuery(id+"F0.wireOp",EDGE,"E972"),sQuery(id+"F0.wireOp",EDGE,"E973"),sQuery(id+"F0.wireOp",EDGE,"E974"),sQuery(id+"F0.wireOp",EDGE,"E975"),sQuery(id+"F0.wireOp",EDGE,"E976"),sQuery(id+"F0.wireOp",EDGE,"E977"),sQuery(id+"F0.wireOp",EDGE,"E978"),sQuery(id+"F0.wireOp",EDGE,"E979"),sQuery(id+"F0.wireOp",EDGE,"E980"),sQuery(id+"F0.wireOp",EDGE,"E981"),sQuery(id+"F0.wireOp",EDGE,"E982"),sQuery(id+"F0.wireOp",EDGE,"E983"),sQuery(id+"F0.wireOp",EDGE,"E984"),sQuery(id+"F0.wireOp",EDGE,"E985"),sQuery(id+"F0.wireOp",EDGE,"E986"),sQuery(id+"F0.wireOp",EDGE,"E987"),sQuery(id+"F0.wireOp",EDGE,"E988"),sQuery(id+"F0.wireOp",EDGE,"E989"),sQuery(id+"F0.wireOp",EDGE,"E990"),sQuery(id+"F0.wireOp",EDGE,"E991"),sQuery(id+"F0.wireOp",EDGE,"E992"),sQuery(id+"F0.wireOp",EDGE,"E993"),sQuery(id+"F0.wireOp",EDGE,"E994"),sQuery(id+"F0.wireOp",EDGE,"E995"),sQuery(id+"F0.wireOp",EDGE,"E996"),sQuery(id+"F0.wireOp",EDGE,"E997"),sQuery(id+"F0.wireOp",EDGE,"E998"),sQuery(id+"F0.wireOp",EDGE,"E999"),sQuery(id+"F0.wireOp",EDGE,"E1000"),sQuery(id+"F0.wireOp",EDGE,"E1001"),sQuery(id+"F0.wireOp",EDGE,"E1002"),sQuery(id+"F0.wireOp",EDGE,"E1003"),sQuery(id+"F0.wireOp",EDGE,"E1004"),sQuery(id+"F0.wireOp",EDGE,"E1005"),sQuery(id+"F0.wireOp",EDGE,"E1006"),sQuery(id+"F0.wireOp",EDGE,"E1007"),sQuery(id+"F0.wireOp",EDGE,"E1008"),sQuery(id+"F0.wireOp",EDGE,"E1009"),sQuery(id+"F0.wireOp",EDGE,"E1010"),sQuery(id+"F0.wireOp",EDGE,"E1011"),sQuery(id+"F0.wireOp",EDGE,"E1012"),sQuery(id+"F0.wireOp",EDGE,"E1013"),sQuery(id+"F0.wireOp",EDGE,"E1014"),sQuery(id+"F0.wireOp",EDGE,"E1015"),sQuery(id+"F0.wireOp",EDGE,"E1016"),sQuery(id+"F0.wireOp",EDGE,"E1017"),sQuery(id+"F0.wireOp",EDGE,"E1018"),sQuery(id+"F0.wireOp",EDGE,"E1019"),sQuery(id+"F0.wireOp",EDGE,"E1020"),sQuery(id+"F0.wireOp",EDGE,"E1021"),sQuery(id+"F0.wireOp",EDGE,"E1022"),sQuery(id+"F0.wireOp",EDGE,"E1023"),sQuery(id+"F0.wireOp",EDGE,"E1024"),sQuery(id+"F0.wireOp",EDGE,"E1025"),sQuery(id+"F0.wireOp",EDGE,"E1026"),sQuery(id+"F0.wireOp",EDGE,"E1027"),sQuery(id+"F0.wireOp",EDGE,"E1028"),sQuery(id+"F0.wireOp",EDGE,"E1029"),sQuery(id+"F0.wireOp",EDGE,"E1030"),sQuery(id+"F0.wireOp",EDGE,"E1031"),sQuery(id+"F0.wireOp",EDGE,"E1032"),sQuery(id+"F0.wireOp",EDGE,"E1033"),sQuery(id+"F0.wireOp",EDGE,"E1034"),sQuery(id+"F0.wireOp",EDGE,"E1035"),sQuery(id+"F0.wireOp",EDGE,"E1036"),sQuery(id+"F0.wireOp",EDGE,"E1037"),sQuery(id+"F0.wireOp",EDGE,"E1038"),sQuery(id+"F0.wireOp",EDGE,"E1039"),sQuery(id+"F0.wireOp",EDGE,"E1040"),sQuery(id+"F0.wireOp",EDGE,"E1041"),sQuery(id+"F0.wireOp",EDGE,"E1042"),sQuery(id+"F0.wireOp",EDGE,"E1043"),sQuery(id+"F0.wireOp",EDGE,"E1044"),sQuery(id+"F0.wireOp",EDGE,"E1045"),sQuery(id+"F0.wireOp",EDGE,"E1046"),sQuery(id+"F0.wireOp",EDGE,"E1047"),sQuery(id+"F0.wireOp",EDGE,"E1048"),sQuery(id+"F0.wireOp",EDGE,"E1049"),sQuery(id+"F0.wireOp",EDGE,"E1050"),sQuery(id+"F0.wireOp",EDGE,"E1051"),sQuery(id+"F0.wireOp",EDGE,"E1052"),sQuery(id+"F0.wireOp",EDGE,"E1053"),sQuery(id+"F0.wireOp",EDGE,"E1054"),sQuery(id+"F0.wireOp",EDGE,"E1055"),sQuery(id+"F0.wireOp",EDGE,"E1056"),sQuery(id+"F0.wireOp",EDGE,"E1057"),sQuery(id+"F0.wireOp",EDGE,"E1058"),sQuery(id+"F0.wireOp",EDGE,"E1059"),sQuery(id+"F0.wireOp",EDGE,"E1060"),sQuery(id+"F0.wireOp",EDGE,"E1061"),sQuery(id+"F0.wireOp",EDGE,"E1062"),sQuery(id+"F0.wireOp",EDGE,"E1063"),sQuery(id+"F0.wireOp",EDGE,"E1064"),sQuery(id+"F0.wireOp",EDGE,"E1065"),sQuery(id+"F0.wireOp",EDGE,"E1066"),sQuery(id+"F0.wireOp",EDGE,"E1067"),sQuery(id+"F0.wireOp",EDGE,"E1068"),sQuery(id+"F0.wireOp",EDGE,"E1069"),sQuery(id+"F0.wireOp",EDGE,"E1070"),sQuery(id+"F0.wireOp",EDGE,"E1071"),sQuery(id+"F0.wireOp",EDGE,"E1072"),sQuery(id+"F0.wireOp",EDGE,"E1073"),sQuery(id+"F0.wireOp",EDGE,"E1074"),sQuery(id+"F0.wireOp",EDGE,"E1075"),sQuery(id+"F0.wireOp",EDGE,"E1076"),sQuery(id+"F0.wireOp",EDGE,"E1077"),sQuery(id+"F0.wireOp",EDGE,"E1078"),sQuery(id+"F0.wireOp",EDGE,"E1079"),sQuery(id+"F0.wireOp",EDGE,"E1080"),sQuery(id+"F0.wireOp",EDGE,"E1081"),sQuery(id+"F0.wireOp",EDGE,"E1082"),sQuery(id+"F0.wireOp",EDGE,"E1083"),sQuery(id+"F0.wireOp",EDGE,"E1084"),sQuery(id+"F0.wireOp",EDGE,"E1085"),sQuery(id+"F0.wireOp",EDGE,"E1086"),sQuery(id+"F0.wireOp",EDGE,"E1087"),sQuery(id+"F0.wireOp",EDGE,"E1088"),sQuery(id+"F0.wireOp",EDGE,"E1089"),sQuery(id+"F0.wireOp",EDGE,"E1090"),sQuery(id+"F0.wireOp",EDGE,"E1091"),sQuery(id+"F0.wireOp",EDGE,"E1092"),sQuery(id+"F0.wireOp",EDGE,"E1093"),sQuery(id+"F0.wireOp",EDGE,"E1094"),sQuery(id+"F0.wireOp",EDGE,"E1095"),sQuery(id+"F0.wireOp",EDGE,"E1096"),sQuery(id+"F0.wireOp",EDGE,"E1097"),sQuery(id+"F0.wireOp",EDGE,"E1098"),sQuery(id+"F0.wireOp",EDGE,"E1099"),sQuery(id+"F0.wireOp",EDGE,"E1100"),sQuery(id+"F0.wireOp",EDGE,"E1101"),sQuery(id+"F0.wireOp",EDGE,"E1102"),sQuery(id+"F0.wireOp",EDGE,"E1103"),sQuery(id+"F0.wireOp",EDGE,"E1104"),sQuery(id+"F0.wireOp",EDGE,"E1105"),sQuery(id+"F0.wireOp",EDGE,"E1106"),sQuery(id+"F0.wireOp",EDGE,"E1107"),sQuery(id+"F0.wireOp",EDGE,"E1108"),sQuery(id+"F0.wireOp",EDGE,"E1109"),sQuery(id+"F0.wireOp",EDGE,"E1110"),sQuery(id+"F0.wireOp",EDGE,"E1111"),sQuery(id+"F0.wireOp",EDGE,"E1112"),sQuery(id+"F0.wireOp",EDGE,"E1113"),sQuery(id+"F0.wireOp",EDGE,"E1114"),sQuery(id+"F0.wireOp",EDGE,"E1115"),sQuery(id+"F0.wireOp",EDGE,"E1116"),sQuery(id+"F0.wireOp",EDGE,"E1117"),sQuery(id+"F0.wireOp",EDGE,"E1118"),sQuery(id+"F0.wireOp",EDGE,"E1119"),sQuery(id+"F0.wireOp",EDGE,"E1120"),sQuery(id+"F0.wireOp",EDGE,"E1121"),sQuery(id+"F0.wireOp",EDGE,"E1122"),sQuery(id+"F0.wireOp",EDGE,"E1123"),sQuery(id+"F0.wireOp",EDGE,"E1124"),sQuery(id+"F0.wireOp",EDGE,"E1125"),sQuery(id+"F0.wireOp",EDGE,"E1126"),sQuery(id+"F0.wireOp",EDGE,"E1127"),sQuery(id+"F0.wireOp",EDGE,"E1128"),sQuery(id+"F0.wireOp",EDGE,"E1129"),sQuery(id+"F0.wireOp",EDGE,"E1130"),sQuery(id+"F0.wireOp",EDGE,"E1131"),sQuery(id+"F0.wireOp",EDGE,"E1132"),sQuery(id+"F0.wireOp",EDGE,"E1133"),sQuery(id+"F0.wireOp",EDGE,"E1134"),sQuery(id+"F0.wireOp",EDGE,"E1135"),sQuery(id+"F0.wireOp",EDGE,"E1136"),sQuery(id+"F0.wireOp",EDGE,"E1137"),sQuery(id+"F0.wireOp",EDGE,"E1138"),sQuery(id+"F0.wireOp",EDGE,"E1139"),sQuery(id+"F0.wireOp",EDGE,"E1140"),sQuery(id+"F0.wireOp",EDGE,"E1141"),sQuery(id+"F0.wireOp",EDGE,"E1142"),sQuery(id+"F0.wireOp",EDGE,"E1143"),sQuery(id+"F0.wireOp",EDGE,"E1144"),sQuery(id+"F0.wireOp",EDGE,"E1145"),sQuery(id+"F0.wireOp",EDGE,"E1146"),sQuery(id+"F0.wireOp",EDGE,"E1147"),sQuery(id+"F0.wireOp",EDGE,"E1148"),sQuery(id+"F0.wireOp",EDGE,"E1149"),sQuery(id+"F0.wireOp",EDGE,"E1150"),sQuery(id+"F0.wireOp",EDGE,"E1151"),sQuery(id+"F0.wireOp",EDGE,"E1152"),sQuery(id+"F0.wireOp",EDGE,"E1153"),sQuery(id+"F0.wireOp",EDGE,"E1154"),sQuery(id+"F0.wireOp",EDGE,"E1155"),sQuery(id+"F0.wireOp",EDGE,"E1156"),sQuery(id+"F0.wireOp",EDGE,"E1157"),sQuery(id+"F0.wireOp",EDGE,"E1158"),sQuery(id+"F0.wireOp",EDGE,"E1159"),sQuery(id+"F0.wireOp",EDGE,"E1160"),sQuery(id+"F0.wireOp",EDGE,"E1161"),sQuery(id+"F0.wireOp",EDGE,"E1162"),sQuery(id+"F0.wireOp",EDGE,"E1163"),sQuery(id+"F0.wireOp",EDGE,"E1164"),sQuery(id+"F0.wireOp",EDGE,"E1165"),sQuery(id+"F0.wireOp",EDGE,"E1166"),sQuery(id+"F0.wireOp",EDGE,"E1167"),sQuery(id+"F0.wireOp",EDGE,"E1168"),sQuery(id+"F0.wireOp",EDGE,"E1169"),sQuery(id+"F0.wireOp",EDGE,"E1170"),sQuery(id+"F0.wireOp",EDGE,"E1171"),sQuery(id+"F0.wireOp",EDGE,"E1172"),sQuery(id+"F0.wireOp",EDGE,"E1173"),sQuery(id+"F0.wireOp",EDGE,"E1174"),sQuery(id+"F0.wireOp",EDGE,"E1175"),sQuery(id+"F0.wireOp",EDGE,"E1176"),sQuery(id+"F0.wireOp",EDGE,"E1177"),sQuery(id+"F0.wireOp",EDGE,"E1178"),sQuery(id+"F0.wireOp",EDGE,"E1179"),sQuery(id+"F0.wireOp",EDGE,"E1180"),sQuery(id+"F0.wireOp",EDGE,"E1181"),sQuery(id+"F0.wireOp",EDGE,"E1182"),sQuery(id+"F0.wireOp",EDGE,"E1183"),sQuery(id+"F0.wireOp",EDGE,"E1184"),sQuery(id+"F0.wireOp",EDGE,"E1185"),sQuery(id+"F0.wireOp",EDGE,"E1186"),sQuery(id+"F0.wireOp",EDGE,"E1187"),sQuery(id+"F0.wireOp",EDGE,"E1188"),sQuery(id+"F0.wireOp",EDGE,"E1189"),sQuery(id+"F0.wireOp",EDGE,"E1190"),sQuery(id+"F0.wireOp",EDGE,"E1191"),sQuery(id+"F0.wireOp",EDGE,"E1192"),sQuery(id+"F0.wireOp",EDGE,"E1193"),sQuery(id+"F0.wireOp",EDGE,"E1194"),sQuery(id+"F0.wireOp",EDGE,"E1195"),sQuery(id+"F0.wireOp",EDGE,"E1196"),sQuery(id+"F0.wireOp",EDGE,"E1197"),sQuery(id+"F0.wireOp",EDGE,"E1198"),sQuery(id+"F0.wireOp",EDGE,"E1199"),sQuery(id+"F0.wireOp",EDGE,"E1200"),sQuery(id+"F0.wireOp",EDGE,"E1201"),sQuery(id+"F0.wireOp",EDGE,"E1202"),sQuery(id+"F0.wireOp",EDGE,"E1203"),sQuery(id+"F0.wireOp",EDGE,"E1204"),sQuery(id+"F0.wireOp",EDGE,"E1205"),sQuery(id+"F0.wireOp",EDGE,"E1206"),sQuery(id+"F0.wireOp",EDGE,"E1207"),sQuery(id+"F0.wireOp",EDGE,"E1208"),sQuery(id+"F0.wireOp",EDGE,"E1209"),sQuery(id+"F0.wireOp",EDGE,"E1210"),sQuery(id+"F0.wireOp",EDGE,"E1211"),sQuery(id+"F0.wireOp",EDGE,"E1212"),sQuery(id+"F0.wireOp",EDGE,"E1213"),sQuery(id+"F0.wireOp",EDGE,"E1214"),sQuery(id+"F0.wireOp",EDGE,"E1215"),sQuery(id+"F0.wireOp",EDGE,"E1216"),sQuery(id+"F0.wireOp",EDGE,"E1217"),sQuery(id+"F0.wireOp",EDGE,"E1218"),sQuery(id+"F0.wireOp",EDGE,"E1219"),sQuery(id+"F0.wireOp",EDGE,"E1220"),sQuery(id+"F0.wireOp",EDGE,"E1221"),sQuery(id+"F0.wireOp",EDGE,"E1222"),sQuery(id+"F0.wireOp",EDGE,"E1223"),sQuery(id+"F0.wireOp",EDGE,"E1224"),sQuery(id+"F0.wireOp",EDGE,"E1225"),sQuery(id+"F0.wireOp",EDGE,"E1226"),sQuery(id+"F0.wireOp",EDGE,"E1227"),sQuery(id+"F0.wireOp",EDGE,"E1228"),sQuery(id+"F0.wireOp",EDGE,"E1229"),sQuery(id+"F0.wireOp",EDGE,"E1230"),sQuery(id+"F0.wireOp",EDGE,"E1231"),sQuery(id+"F0.wireOp",EDGE,"E1232"),sQuery(id+"F0.wireOp",EDGE,"E1233"),sQuery(id+"F0.wireOp",EDGE,"E1234"),sQuery(id+"F0.wireOp",EDGE,"E1235"),sQuery(id+"F0.wireOp",EDGE,"E1236"),sQuery(id+"F0.wireOp",EDGE,"E1237"),sQuery(id+"F0.wireOp",EDGE,"E1238"),sQuery(id+"F0.wireOp",EDGE,"E1239"),sQuery(id+"F0.wireOp",EDGE,"E1240"),sQuery(id+"F0.wireOp",EDGE,"E1241"),sQuery(id+"F0.wireOp",EDGE,"E1242"),sQuery(id+"F0.wireOp",EDGE,"E1243"),sQuery(id+"F0.wireOp",EDGE,"E1244"),sQuery(id+"F0.wireOp",EDGE,"E1245"),sQuery(id+"F0.wireOp",EDGE,"E1246"),sQuery(id+"F0.wireOp",EDGE,"E1247"),sQuery(id+"F0.wireOp",EDGE,"E1248"),sQuery(id+"F0.wireOp",EDGE,"E1249"),sQuery(id+"F0.wireOp",EDGE,"E1250"),sQuery(id+"F0.wireOp",EDGE,"E1251"),sQuery(id+"F0.wireOp",EDGE,"E1252"),sQuery(id+"F0.wireOp",EDGE,"E1253"),sQuery(id+"F0.wireOp",EDGE,"E1254"),sQuery(id+"F0.wireOp",EDGE,"E1255"),sQuery(id+"F0.wireOp",EDGE,"E1256"),sQuery(id+"F0.wireOp",EDGE,"E1257"),sQuery(id+"F0.wireOp",EDGE,"E1258"),sQuery(id+"F0.wireOp",EDGE,"E1259"),sQuery(id+"F0.wireOp",EDGE,"E1260"),sQuery(id+"F0.wireOp",EDGE,"E1261"),sQuery(id+"F0.wireOp",EDGE,"E1262"),sQuery(id+"F0.wireOp",EDGE,"E1263"),sQuery(id+"F0.wireOp",EDGE,"E1264"),sQuery(id+"F0.wireOp",EDGE,"E1265"),sQuery(id+"F0.wireOp",EDGE,"E1266"),sQuery(id+"F0.wireOp",EDGE,"E1267"),sQuery(id+"F0.wireOp",EDGE,"E1268"),sQuery(id+"F0.wireOp",EDGE,"E1269"),sQuery(id+"F0.wireOp",EDGE,"E1270"),sQuery(id+"F0.wireOp",EDGE,"E1271"),sQuery(id+"F0.wireOp",EDGE,"E1272"),sQuery(id+"F0.wireOp",EDGE,"E1273"),sQuery(id+"F0.wireOp",EDGE,"E1274"),sQuery(id+"F0.wireOp",EDGE,"E1275"),sQuery(id+"F0.wireOp",EDGE,"E1276"),sQuery(id+"F0.wireOp",EDGE,"E1277"),sQuery(id+"F0.wireOp",EDGE,"E1278"),sQuery(id+"F0.wireOp",EDGE,"E1279"),sQuery(id+"F0.wireOp",EDGE,"E1280"),sQuery(id+"F0.wireOp",EDGE,"E1281"),sQuery(id+"F0.wireOp",EDGE,"E1282"),sQuery(id+"F0.wireOp",EDGE,"E1283"),sQuery(id+"F0.wireOp",EDGE,"E1284"),sQuery(id+"F0.wireOp",EDGE,"E1285"),sQuery(id+"F0.wireOp",EDGE,"E1286"),sQuery(id+"F0.wireOp",EDGE,"E1287"),sQuery(id+"F0.wireOp",EDGE,"E1288"),sQuery(id+"F0.wireOp",EDGE,"E1289"),sQuery(id+"F0.wireOp",EDGE,"E1290"),sQuery(id+"F0.wireOp",EDGE,"E1291"),sQuery(id+"F0.wireOp",EDGE,"E1292"),sQuery(id+"F0.wireOp",EDGE,"E1293"),sQuery(id+"F0.wireOp",EDGE,"E1294"),sQuery(id+"F0.wireOp",EDGE,"E1295"),sQuery(id+"F0.wireOp",EDGE,"E1296"),sQuery(id+"F0.wireOp",EDGE,"E1297"),sQuery(id+"F0.wireOp",EDGE,"E1298"),sQuery(id+"F0.wireOp",EDGE,"E1299"),sQuery(id+"F0.wireOp",EDGE,"E1300"),sQuery(id+"F0.wireOp",EDGE,"E1301"),sQuery(id+"F0.wireOp",EDGE,"E1302"),sQuery(id+"F0.wireOp",EDGE,"E1303"),sQuery(id+"F0.wireOp",EDGE,"E1304"),sQuery(id+"F0.wireOp",EDGE,"E1305"),sQuery(id+"F0.wireOp",EDGE,"E1306"),sQuery(id+"F0.wireOp",EDGE,"E1307"),sQuery(id+"F0.wireOp",EDGE,"E1308"),sQuery(id+"F0.wireOp",EDGE,"E1309"),sQuery(id+"F0.wireOp",EDGE,"E1310"),sQuery(id+"F0.wireOp",EDGE,"E1311"),sQuery(id+"F0.wireOp",EDGE,"E1312"),sQuery(id+"F0.wireOp",EDGE,"E1313"),sQuery(id+"F0.wireOp",EDGE,"E1314"),sQuery(id+"F0.wireOp",EDGE,"E1315"),sQuery(id+"F0.wireOp",EDGE,"E1316"),sQuery(id+"F0.wireOp",EDGE,"E1317"),sQuery(id+"F0.wireOp",EDGE,"E1318"),sQuery(id+"F0.wireOp",EDGE,"E1319"),sQuery(id+"F0.wireOp",EDGE,"E1320"),sQuery(id+"F0.wireOp",EDGE,"E1321"),sQuery(id+"F0.wireOp",EDGE,"E1322"),sQuery(id+"F0.wireOp",EDGE,"E1323"),sQuery(id+"F0.wireOp",EDGE,"E1324"),sQuery(id+"F0.wireOp",EDGE,"E1325"),sQuery(id+"F0.wireOp",EDGE,"E1326"),sQuery(id+"F0.wireOp",EDGE,"E1327"),sQuery(id+"F0.wireOp",EDGE,"E1328"),sQuery(id+"F0.wireOp",EDGE,"E1329"),sQuery(id+"F0.wireOp",EDGE,"E1330"),sQuery(id+"F0.wireOp",EDGE,"E1331"),sQuery(id+"F0.wireOp",EDGE,"E1332"),sQuery(id+"F0.wireOp",EDGE,"E1333"),sQuery(id+"F0.wireOp",EDGE,"E1334"),sQuery(id+"F0.wireOp",EDGE,"E1335"),sQuery(id+"F0.wireOp",EDGE,"E1336"),sQuery(id+"F0.wireOp",EDGE,"E1337"),sQuery(id+"F0.wireOp",EDGE,"E1338"),sQuery(id+"F0.wireOp",EDGE,"E1339"),sQuery(id+"F0.wireOp",EDGE,"E1340"),sQuery(id+"F0.wireOp",EDGE,"E1341"),sQuery(id+"F0.wireOp",EDGE,"E1342"),sQuery(id+"F0.wireOp",EDGE,"E1343"),sQuery(id+"F0.wireOp",EDGE,"E1344"),sQuery(id+"F0.wireOp",EDGE,"E1345"),sQuery(id+"F0.wireOp",EDGE,"E1346"),sQuery(id+"F0.wireOp",EDGE,"E1347"),sQuery(id+"F0.wireOp",EDGE,"E1348"),sQuery(id+"F0.wireOp",EDGE,"E1349"),sQuery(id+"F0.wireOp",EDGE,"E1350"),sQuery(id+"F0.wireOp",EDGE,"E1351"),sQuery(id+"F0.wireOp",EDGE,"E1352"),sQuery(id+"F0.wireOp",EDGE,"E1353"),sQuery(id+"F0.wireOp",EDGE,"E1354"),sQuery(id+"F0.wireOp",EDGE,"E1355"),sQuery(id+"F0.wireOp",EDGE,"E1356"),sQuery(id+"F0.wireOp",EDGE,"E1357"),sQuery(id+"F0.wireOp",EDGE,"E1358"),sQuery(id+"F0.wireOp",EDGE,"E1359"),sQuery(id+"F0.wireOp",EDGE,"E1360"),sQuery(id+"F0.wireOp",EDGE,"E1361"),sQuery(id+"F0.wireOp",EDGE,"E1362"),sQuery(id+"F0.wireOp",EDGE,"E1363"),sQuery(id+"F0.wireOp",EDGE,"E1364"),sQuery(id+"F0.wireOp",EDGE,"E1365"),sQuery(id+"F0.wireOp",EDGE,"E1366"),sQuery(id+"F0.wireOp",EDGE,"E1367"),sQuery(id+"F0.wireOp",EDGE,"E1368"),sQuery(id+"F0.wireOp",EDGE,"E1369"),sQuery(id+"F0.wireOp",EDGE,"E1370"),sQuery(id+"F0.wireOp",EDGE,"E1371"),sQuery(id+"F0.wireOp",EDGE,"E1372"),sQuery(id+"F0.wireOp",EDGE,"E1373"),sQuery(id+"F0.wireOp",EDGE,"E1374"),sQuery(id+"F0.wireOp",EDGE,"E1375"),sQuery(id+"F0.wireOp",EDGE,"E1376"),sQuery(id+"F0.wireOp",EDGE,"E1377"),sQuery(id+"F0.wireOp",EDGE,"E1378"),sQuery(id+"F0.wireOp",EDGE,"E1379"),sQuery(id+"F0.wireOp",EDGE,"E1380"),sQuery(id+"F0.wireOp",EDGE,"E1381"),sQuery(id+"F0.wireOp",EDGE,"E1382"),sQuery(id+"F0.wireOp",EDGE,"E1383"),sQuery(id+"F0.wireOp",EDGE,"E1384"),sQuery(id+"F0.wireOp",EDGE,"E1385"),sQuery(id+"F0.wireOp",EDGE,"E1386"),sQuery(id+"F0.wireOp",EDGE,"E1387"),sQuery(id+"F0.wireOp",EDGE,"E1388"),sQuery(id+"F0.wireOp",EDGE,"E1389"),sQuery(id+"F0.wireOp",EDGE,"E1390"),sQuery(id+"F0.wireOp",EDGE,"E1391"),sQuery(id+"F0.wireOp",EDGE,"E1392"),sQuery(id+"F0.wireOp",EDGE,"E1393"),sQuery(id+"F0.wireOp",EDGE,"E1394"),sQuery(id+"F0.wireOp",EDGE,"E1395"),sQuery(id+"F0.wireOp",EDGE,"E1396"),sQuery(id+"F0.wireOp",EDGE,"E1397"),sQuery(id+"F0.wireOp",EDGE,"E1398"),sQuery(id+"F0.wireOp",EDGE,"E1399"),sQuery(id+"F0.wireOp",EDGE,"E1400"),sQuery(id+"F0.wireOp",EDGE,"E1401"),sQuery(id+"F0.wireOp",EDGE,"E1402"),sQuery(id+"F0.wireOp",EDGE,"E1403"),sQuery(id+"F0.wireOp",EDGE,"E1404"),sQuery(id+"F0.wireOp",EDGE,"E1405"),sQuery(id+"F0.wireOp",EDGE,"E1406"),sQuery(id+"F0.wireOp",EDGE,"E1407"),sQuery(id+"F0.wireOp",EDGE,"E1408"),sQuery(id+"F0.wireOp",EDGE,"E1409"),sQuery(id+"F0.wireOp",EDGE,"E1410"),sQuery(id+"F0.wireOp",EDGE,"E1411"),sQuery(id+"F0.wireOp",EDGE,"E1412"),sQuery(id+"F0.wireOp",EDGE,"E1413"),sQuery(id+"F0.wireOp",EDGE,"E1414"),sQuery(id+"F0.wireOp",EDGE,"E1415"),sQuery(id+"F0.wireOp",EDGE,"E1416"),sQuery(id+"F0.wireOp",EDGE,"E1417"),sQuery(id+"F0.wireOp",EDGE,"E1418"),sQuery(id+"F0.wireOp",EDGE,"E1419"),sQuery(id+"F0.wireOp",EDGE,"E1420"),sQuery(id+"F0.wireOp",EDGE,"E1421"),sQuery(id+"F0.wireOp",EDGE,"E1422"),sQuery(id+"F0.wireOp",EDGE,"E1423"),sQuery(id+"F0.wireOp",EDGE,"E1424"),sQuery(id+"F0.wireOp",EDGE,"E1425"),sQuery(id+"F0.wireOp",EDGE,"E1426"),sQuery(id+"F0.wireOp",EDGE,"E1427"),sQuery(id+"F0.wireOp",EDGE,"E1428"),sQuery(id+"F0.wireOp",EDGE,"E1429"),sQuery(id+"F0.wireOp",EDGE,"E1430"),sQuery(id+"F0.wireOp",EDGE,"E1431"),sQuery(id+"F0.wireOp",EDGE,"E1432"),sQuery(id+"F0.wireOp",EDGE,"E1433"),sQuery(id+"F0.wireOp",EDGE,"E1434"),sQuery(id+"F0.wireOp",EDGE,"E1435"),sQuery(id+"F0.wireOp",EDGE,"E1436"),sQuery(id+"F0.wireOp",EDGE,"E1437"),sQuery(id+"F0.wireOp",EDGE,"E1438"),sQuery(id+"F0.wireOp",EDGE,"E1439"),sQuery(id+"F0.wireOp",EDGE,"E1440"),sQuery(id+"F0.wireOp",EDGE,"E1441"),sQuery(id+"F0.wireOp",EDGE,"E1442"),sQuery(id+"F0.wireOp",EDGE,"E1443")])],"isStart":false});
            var sketch = newSketch(context, id + "F2", { "sketchPlane" : qUnion([Q0])});
            skPoint(sketch, "E1444", {"position": v(-219, 43) * mm});
            skPoint(sketch, "E1445", {"position": v(-219, -43) * mm});
            skPoint(sketch, "E1446", {"position": v(-109.5, -43) * mm});
            skPoint(sketch, "E1447", {"position": v(0, -43) * mm});
            skPoint(sketch, "E1448", {"position": v(109.5, -43) * mm});
            skPoint(sketch, "E1449", {"position": v(109.5, 43) * mm});
            skPoint(sketch, "E1450", {"position": v(0, 43) * mm});
            skPoint(sketch, "E1451", {"position": v(-109.5, 43) * mm});
            skLineSegment(sketch, "E1452.bottom", {"start": v(-224, 48) * mm, "end": v(224, 48) * mm});
            skLineSegment(sketch, "E1452.top", {"start": v(-224, -48) * mm, "end": v(224, -48) * mm});
            skLineSegment(sketch, "E1452.left", {"start": v(-224, 48) * mm, "end": v(-224, -48) * mm});
            skLineSegment(sketch, "E1452.right", {"start": v(224, 48) * mm, "end": v(224, -48) * mm});
            skPoint(sketch, "E1453", {"position": v(219, 43) * mm});
            skPoint(sketch, "E1454", {"position": v(219, -43) * mm});
            skSolve(sketch);
        }
        {
            var Q0;
            Q0=makeQuery(id+"F2.imprint","IMPRINT",FACE,{"disambiguationData":[TD([[makeQuery(id+"F2.imprint","IMPRINT",EDGE,{"derivedFrom":sQuery(id+"F2.wireOp",EDGE,"E1452.bottom")}),1.0]])]});
            extrude(context, id + "F3", {"entities" : qUnion([Q0]), "operationType" : NewBodyOperationType.REMOVE, "endBound" : BoundingType.THROUGH_ALL, "oppositeDirection" : true, "depth" : 25 * mm});
        }
        {
            var Q0;
            Q0=sQuery(id+"F2.wireOp",VERTEX,"E1444");
            var Q1;
            Q1=sQuery(id+"F2.wireOp",VERTEX,"E1445");
            var Q2;
            Q2=sQuery(id+"F2.wireOp",VERTEX,"E1446");
            var Q3;
            Q3=sQuery(id+"F2.wireOp",VERTEX,"E1451");
            var Q4;
            Q4=sQuery(id+"F2.wireOp",VERTEX,"E1450");
            var Q5;
            Q5=sQuery(id+"F2.wireOp",VERTEX,"E1447");
            var Q6;
            Q6=sQuery(id+"F2.wireOp",VERTEX,"E1449");
            var Q7;
            Q7=sQuery(id+"F2.wireOp",VERTEX,"E1448");
            var Q8;
            Q8=sQuery(id+"F2.wireOp",VERTEX,"E1453");
            var Q9;
            Q9=sQuery(id+"F2.wireOp",VERTEX,"E1454");
            var Q10;
            Q10=makeQuery(id+"F1.opExtrude","SWEPT_BODY",BODY,{"disambiguationData":[OSD([sQuery(id+"F0.wireOp",EDGE,"E0"),sQuery(id+"F0.wireOp",EDGE,"E1"),sQuery(id+"F0.wireOp",EDGE,"E2"),sQuery(id+"F0.wireOp",EDGE,"E3"),sQuery(id+"F0.wireOp",EDGE,"E4"),sQuery(id+"F0.wireOp",EDGE,"E5"),sQuery(id+"F0.wireOp",EDGE,"E6"),sQuery(id+"F0.wireOp",EDGE,"E7"),sQuery(id+"F0.wireOp",EDGE,"E8"),sQuery(id+"F0.wireOp",EDGE,"E9"),sQuery(id+"F0.wireOp",EDGE,"E10"),sQuery(id+"F0.wireOp",EDGE,"E11"),sQuery(id+"F0.wireOp",EDGE,"E12"),sQuery(id+"F0.wireOp",EDGE,"E13"),sQuery(id+"F0.wireOp",EDGE,"E14"),sQuery(id+"F0.wireOp",EDGE,"E15"),sQuery(id+"F0.wireOp",EDGE,"E16"),sQuery(id+"F0.wireOp",EDGE,"E17"),sQuery(id+"F0.wireOp",EDGE,"E18"),sQuery(id+"F0.wireOp",EDGE,"E19"),sQuery(id+"F0.wireOp",EDGE,"E20"),sQuery(id+"F0.wireOp",EDGE,"E21"),sQuery(id+"F0.wireOp",EDGE,"E22"),sQuery(id+"F0.wireOp",EDGE,"E23"),sQuery(id+"F0.wireOp",EDGE,"E24"),sQuery(id+"F0.wireOp",EDGE,"E25"),sQuery(id+"F0.wireOp",EDGE,"E26"),sQuery(id+"F0.wireOp",EDGE,"E27"),sQuery(id+"F0.wireOp",EDGE,"E28"),sQuery(id+"F0.wireOp",EDGE,"E29"),sQuery(id+"F0.wireOp",EDGE,"E30"),sQuery(id+"F0.wireOp",EDGE,"E31"),sQuery(id+"F0.wireOp",EDGE,"E32"),sQuery(id+"F0.wireOp",EDGE,"E33"),sQuery(id+"F0.wireOp",EDGE,"E34"),sQuery(id+"F0.wireOp",EDGE,"E35"),sQuery(id+"F0.wireOp",EDGE,"E36"),sQuery(id+"F0.wireOp",EDGE,"E37"),sQuery(id+"F0.wireOp",EDGE,"E38"),sQuery(id+"F0.wireOp",EDGE,"E39"),sQuery(id+"F0.wireOp",EDGE,"E40"),sQuery(id+"F0.wireOp",EDGE,"E41"),sQuery(id+"F0.wireOp",EDGE,"E42"),sQuery(id+"F0.wireOp",EDGE,"E43"),sQuery(id+"F0.wireOp",EDGE,"E44"),sQuery(id+"F0.wireOp",EDGE,"E45"),sQuery(id+"F0.wireOp",EDGE,"E46"),sQuery(id+"F0.wireOp",EDGE,"E47"),sQuery(id+"F0.wireOp",EDGE,"E48"),sQuery(id+"F0.wireOp",EDGE,"E49"),sQuery(id+"F0.wireOp",EDGE,"E50"),sQuery(id+"F0.wireOp",EDGE,"E51"),sQuery(id+"F0.wireOp",EDGE,"E52"),sQuery(id+"F0.wireOp",EDGE,"E53"),sQuery(id+"F0.wireOp",EDGE,"E54"),sQuery(id+"F0.wireOp",EDGE,"E55"),sQuery(id+"F0.wireOp",EDGE,"E56"),sQuery(id+"F0.wireOp",EDGE,"E57"),sQuery(id+"F0.wireOp",EDGE,"E58"),sQuery(id+"F0.wireOp",EDGE,"E59"),sQuery(id+"F0.wireOp",EDGE,"E60"),sQuery(id+"F0.wireOp",EDGE,"E61"),sQuery(id+"F0.wireOp",EDGE,"E62"),sQuery(id+"F0.wireOp",EDGE,"E63"),sQuery(id+"F0.wireOp",EDGE,"E64"),sQuery(id+"F0.wireOp",EDGE,"E65"),sQuery(id+"F0.wireOp",EDGE,"E66"),sQuery(id+"F0.wireOp",EDGE,"E67"),sQuery(id+"F0.wireOp",EDGE,"E68"),sQuery(id+"F0.wireOp",EDGE,"E69"),sQuery(id+"F0.wireOp",EDGE,"E70"),sQuery(id+"F0.wireOp",EDGE,"E71"),sQuery(id+"F0.wireOp",EDGE,"E72"),sQuery(id+"F0.wireOp",EDGE,"E73"),sQuery(id+"F0.wireOp",EDGE,"E74"),sQuery(id+"F0.wireOp",EDGE,"E75"),sQuery(id+"F0.wireOp",EDGE,"E76"),sQuery(id+"F0.wireOp",EDGE,"E77"),sQuery(id+"F0.wireOp",EDGE,"E78"),sQuery(id+"F0.wireOp",EDGE,"E79"),sQuery(id+"F0.wireOp",EDGE,"E80"),sQuery(id+"F0.wireOp",EDGE,"E81"),sQuery(id+"F0.wireOp",EDGE,"E82"),sQuery(id+"F0.wireOp",EDGE,"E83"),sQuery(id+"F0.wireOp",EDGE,"E84"),sQuery(id+"F0.wireOp",EDGE,"E85"),sQuery(id+"F0.wireOp",EDGE,"E86"),sQuery(id+"F0.wireOp",EDGE,"E87"),sQuery(id+"F0.wireOp",EDGE,"E88"),sQuery(id+"F0.wireOp",EDGE,"E89"),sQuery(id+"F0.wireOp",EDGE,"E90"),sQuery(id+"F0.wireOp",EDGE,"E91"),sQuery(id+"F0.wireOp",EDGE,"E92"),sQuery(id+"F0.wireOp",EDGE,"E93"),sQuery(id+"F0.wireOp",EDGE,"E94"),sQuery(id+"F0.wireOp",EDGE,"E95"),sQuery(id+"F0.wireOp",EDGE,"E96"),sQuery(id+"F0.wireOp",EDGE,"E97"),sQuery(id+"F0.wireOp",EDGE,"E98"),sQuery(id+"F0.wireOp",EDGE,"E99"),sQuery(id+"F0.wireOp",EDGE,"E100"),sQuery(id+"F0.wireOp",EDGE,"E101"),sQuery(id+"F0.wireOp",EDGE,"E102"),sQuery(id+"F0.wireOp",EDGE,"E103"),sQuery(id+"F0.wireOp",EDGE,"E104"),sQuery(id+"F0.wireOp",EDGE,"E105"),sQuery(id+"F0.wireOp",EDGE,"E106"),sQuery(id+"F0.wireOp",EDGE,"E107"),sQuery(id+"F0.wireOp",EDGE,"E108"),sQuery(id+"F0.wireOp",EDGE,"E109"),sQuery(id+"F0.wireOp",EDGE,"E110"),sQuery(id+"F0.wireOp",EDGE,"E111"),sQuery(id+"F0.wireOp",EDGE,"E112"),sQuery(id+"F0.wireOp",EDGE,"E113"),sQuery(id+"F0.wireOp",EDGE,"E114"),sQuery(id+"F0.wireOp",EDGE,"E115"),sQuery(id+"F0.wireOp",EDGE,"E116"),sQuery(id+"F0.wireOp",EDGE,"E117"),sQuery(id+"F0.wireOp",EDGE,"E118"),sQuery(id+"F0.wireOp",EDGE,"E119"),sQuery(id+"F0.wireOp",EDGE,"E120"),sQuery(id+"F0.wireOp",EDGE,"E121"),sQuery(id+"F0.wireOp",EDGE,"E122"),sQuery(id+"F0.wireOp",EDGE,"E123"),sQuery(id+"F0.wireOp",EDGE,"E124"),sQuery(id+"F0.wireOp",EDGE,"E125"),sQuery(id+"F0.wireOp",EDGE,"E126"),sQuery(id+"F0.wireOp",EDGE,"E127"),sQuery(id+"F0.wireOp",EDGE,"E128"),sQuery(id+"F0.wireOp",EDGE,"E129"),sQuery(id+"F0.wireOp",EDGE,"E130"),sQuery(id+"F0.wireOp",EDGE,"E131"),sQuery(id+"F0.wireOp",EDGE,"E132"),sQuery(id+"F0.wireOp",EDGE,"E133"),sQuery(id+"F0.wireOp",EDGE,"E134"),sQuery(id+"F0.wireOp",EDGE,"E135"),sQuery(id+"F0.wireOp",EDGE,"E136"),sQuery(id+"F0.wireOp",EDGE,"E137"),sQuery(id+"F0.wireOp",EDGE,"E138"),sQuery(id+"F0.wireOp",EDGE,"E139"),sQuery(id+"F0.wireOp",EDGE,"E140"),sQuery(id+"F0.wireOp",EDGE,"E141"),sQuery(id+"F0.wireOp",EDGE,"E142"),sQuery(id+"F0.wireOp",EDGE,"E143"),sQuery(id+"F0.wireOp",EDGE,"E144"),sQuery(id+"F0.wireOp",EDGE,"E145"),sQuery(id+"F0.wireOp",EDGE,"E146"),sQuery(id+"F0.wireOp",EDGE,"E147"),sQuery(id+"F0.wireOp",EDGE,"E148"),sQuery(id+"F0.wireOp",EDGE,"E149"),sQuery(id+"F0.wireOp",EDGE,"E150"),sQuery(id+"F0.wireOp",EDGE,"E151"),sQuery(id+"F0.wireOp",EDGE,"E152"),sQuery(id+"F0.wireOp",EDGE,"E153"),sQuery(id+"F0.wireOp",EDGE,"E154"),sQuery(id+"F0.wireOp",EDGE,"E155"),sQuery(id+"F0.wireOp",EDGE,"E156"),sQuery(id+"F0.wireOp",EDGE,"E157"),sQuery(id+"F0.wireOp",EDGE,"E158"),sQuery(id+"F0.wireOp",EDGE,"E159"),sQuery(id+"F0.wireOp",EDGE,"E160"),sQuery(id+"F0.wireOp",EDGE,"E161"),sQuery(id+"F0.wireOp",EDGE,"E162"),sQuery(id+"F0.wireOp",EDGE,"E163"),sQuery(id+"F0.wireOp",EDGE,"E164"),sQuery(id+"F0.wireOp",EDGE,"E165"),sQuery(id+"F0.wireOp",EDGE,"E166"),sQuery(id+"F0.wireOp",EDGE,"E167"),sQuery(id+"F0.wireOp",EDGE,"E168"),sQuery(id+"F0.wireOp",EDGE,"E169"),sQuery(id+"F0.wireOp",EDGE,"E170"),sQuery(id+"F0.wireOp",EDGE,"E171"),sQuery(id+"F0.wireOp",EDGE,"E172"),sQuery(id+"F0.wireOp",EDGE,"E173"),sQuery(id+"F0.wireOp",EDGE,"E174"),sQuery(id+"F0.wireOp",EDGE,"E175"),sQuery(id+"F0.wireOp",EDGE,"E176"),sQuery(id+"F0.wireOp",EDGE,"E177"),sQuery(id+"F0.wireOp",EDGE,"E178"),sQuery(id+"F0.wireOp",EDGE,"E179"),sQuery(id+"F0.wireOp",EDGE,"E180"),sQuery(id+"F0.wireOp",EDGE,"E181"),sQuery(id+"F0.wireOp",EDGE,"E182"),sQuery(id+"F0.wireOp",EDGE,"E183"),sQuery(id+"F0.wireOp",EDGE,"E184"),sQuery(id+"F0.wireOp",EDGE,"E185"),sQuery(id+"F0.wireOp",EDGE,"E186"),sQuery(id+"F0.wireOp",EDGE,"E187"),sQuery(id+"F0.wireOp",EDGE,"E188"),sQuery(id+"F0.wireOp",EDGE,"E189"),sQuery(id+"F0.wireOp",EDGE,"E190"),sQuery(id+"F0.wireOp",EDGE,"E191"),sQuery(id+"F0.wireOp",EDGE,"E192"),sQuery(id+"F0.wireOp",EDGE,"E193"),sQuery(id+"F0.wireOp",EDGE,"E194"),sQuery(id+"F0.wireOp",EDGE,"E195"),sQuery(id+"F0.wireOp",EDGE,"E196"),sQuery(id+"F0.wireOp",EDGE,"E197"),sQuery(id+"F0.wireOp",EDGE,"E198"),sQuery(id+"F0.wireOp",EDGE,"E199"),sQuery(id+"F0.wireOp",EDGE,"E200"),sQuery(id+"F0.wireOp",EDGE,"E201"),sQuery(id+"F0.wireOp",EDGE,"E202"),sQuery(id+"F0.wireOp",EDGE,"E203"),sQuery(id+"F0.wireOp",EDGE,"E204"),sQuery(id+"F0.wireOp",EDGE,"E205"),sQuery(id+"F0.wireOp",EDGE,"E206"),sQuery(id+"F0.wireOp",EDGE,"E207"),sQuery(id+"F0.wireOp",EDGE,"E208"),sQuery(id+"F0.wireOp",EDGE,"E209"),sQuery(id+"F0.wireOp",EDGE,"E210"),sQuery(id+"F0.wireOp",EDGE,"E211"),sQuery(id+"F0.wireOp",EDGE,"E212"),sQuery(id+"F0.wireOp",EDGE,"E213"),sQuery(id+"F0.wireOp",EDGE,"E214"),sQuery(id+"F0.wireOp",EDGE,"E215"),sQuery(id+"F0.wireOp",EDGE,"E216"),sQuery(id+"F0.wireOp",EDGE,"E217"),sQuery(id+"F0.wireOp",EDGE,"E218"),sQuery(id+"F0.wireOp",EDGE,"E219"),sQuery(id+"F0.wireOp",EDGE,"E220"),sQuery(id+"F0.wireOp",EDGE,"E221"),sQuery(id+"F0.wireOp",EDGE,"E222"),sQuery(id+"F0.wireOp",EDGE,"E223"),sQuery(id+"F0.wireOp",EDGE,"E224"),sQuery(id+"F0.wireOp",EDGE,"E225"),sQuery(id+"F0.wireOp",EDGE,"E226"),sQuery(id+"F0.wireOp",EDGE,"E227"),sQuery(id+"F0.wireOp",EDGE,"E228"),sQuery(id+"F0.wireOp",EDGE,"E229"),sQuery(id+"F0.wireOp",EDGE,"E230"),sQuery(id+"F0.wireOp",EDGE,"E231"),sQuery(id+"F0.wireOp",EDGE,"E232"),sQuery(id+"F0.wireOp",EDGE,"E233"),sQuery(id+"F0.wireOp",EDGE,"E234"),sQuery(id+"F0.wireOp",EDGE,"E235"),sQuery(id+"F0.wireOp",EDGE,"E236"),sQuery(id+"F0.wireOp",EDGE,"E237"),sQuery(id+"F0.wireOp",EDGE,"E238"),sQuery(id+"F0.wireOp",EDGE,"E239"),sQuery(id+"F0.wireOp",EDGE,"E240"),sQuery(id+"F0.wireOp",EDGE,"E241"),sQuery(id+"F0.wireOp",EDGE,"E242"),sQuery(id+"F0.wireOp",EDGE,"E243"),sQuery(id+"F0.wireOp",EDGE,"E244"),sQuery(id+"F0.wireOp",EDGE,"E245"),sQuery(id+"F0.wireOp",EDGE,"E246"),sQuery(id+"F0.wireOp",EDGE,"E247"),sQuery(id+"F0.wireOp",EDGE,"E248"),sQuery(id+"F0.wireOp",EDGE,"E249"),sQuery(id+"F0.wireOp",EDGE,"E250"),sQuery(id+"F0.wireOp",EDGE,"E251"),sQuery(id+"F0.wireOp",EDGE,"E252"),sQuery(id+"F0.wireOp",EDGE,"E253"),sQuery(id+"F0.wireOp",EDGE,"E254"),sQuery(id+"F0.wireOp",EDGE,"E255"),sQuery(id+"F0.wireOp",EDGE,"E256"),sQuery(id+"F0.wireOp",EDGE,"E257"),sQuery(id+"F0.wireOp",EDGE,"E258"),sQuery(id+"F0.wireOp",EDGE,"E259"),sQuery(id+"F0.wireOp",EDGE,"E260"),sQuery(id+"F0.wireOp",EDGE,"E261"),sQuery(id+"F0.wireOp",EDGE,"E262"),sQuery(id+"F0.wireOp",EDGE,"E263"),sQuery(id+"F0.wireOp",EDGE,"E264"),sQuery(id+"F0.wireOp",EDGE,"E265"),sQuery(id+"F0.wireOp",EDGE,"E266"),sQuery(id+"F0.wireOp",EDGE,"E267"),sQuery(id+"F0.wireOp",EDGE,"E268"),sQuery(id+"F0.wireOp",EDGE,"E269"),sQuery(id+"F0.wireOp",EDGE,"E270"),sQuery(id+"F0.wireOp",EDGE,"E271"),sQuery(id+"F0.wireOp",EDGE,"E272"),sQuery(id+"F0.wireOp",EDGE,"E273"),sQuery(id+"F0.wireOp",EDGE,"E274"),sQuery(id+"F0.wireOp",EDGE,"E275"),sQuery(id+"F0.wireOp",EDGE,"E276"),sQuery(id+"F0.wireOp",EDGE,"E277"),sQuery(id+"F0.wireOp",EDGE,"E278"),sQuery(id+"F0.wireOp",EDGE,"E279"),sQuery(id+"F0.wireOp",EDGE,"E280"),sQuery(id+"F0.wireOp",EDGE,"E281"),sQuery(id+"F0.wireOp",EDGE,"E282"),sQuery(id+"F0.wireOp",EDGE,"E283"),sQuery(id+"F0.wireOp",EDGE,"E284"),sQuery(id+"F0.wireOp",EDGE,"E285"),sQuery(id+"F0.wireOp",EDGE,"E286"),sQuery(id+"F0.wireOp",EDGE,"E287"),sQuery(id+"F0.wireOp",EDGE,"E288"),sQuery(id+"F0.wireOp",EDGE,"E289"),sQuery(id+"F0.wireOp",EDGE,"E290"),sQuery(id+"F0.wireOp",EDGE,"E291"),sQuery(id+"F0.wireOp",EDGE,"E292"),sQuery(id+"F0.wireOp",EDGE,"E293"),sQuery(id+"F0.wireOp",EDGE,"E294"),sQuery(id+"F0.wireOp",EDGE,"E295"),sQuery(id+"F0.wireOp",EDGE,"E296"),sQuery(id+"F0.wireOp",EDGE,"E297"),sQuery(id+"F0.wireOp",EDGE,"E298"),sQuery(id+"F0.wireOp",EDGE,"E299"),sQuery(id+"F0.wireOp",EDGE,"E300"),sQuery(id+"F0.wireOp",EDGE,"E301"),sQuery(id+"F0.wireOp",EDGE,"E302"),sQuery(id+"F0.wireOp",EDGE,"E303"),sQuery(id+"F0.wireOp",EDGE,"E304"),sQuery(id+"F0.wireOp",EDGE,"E305"),sQuery(id+"F0.wireOp",EDGE,"E306"),sQuery(id+"F0.wireOp",EDGE,"E307"),sQuery(id+"F0.wireOp",EDGE,"E308"),sQuery(id+"F0.wireOp",EDGE,"E309"),sQuery(id+"F0.wireOp",EDGE,"E310"),sQuery(id+"F0.wireOp",EDGE,"E311"),sQuery(id+"F0.wireOp",EDGE,"E312"),sQuery(id+"F0.wireOp",EDGE,"E313"),sQuery(id+"F0.wireOp",EDGE,"E314"),sQuery(id+"F0.wireOp",EDGE,"E315"),sQuery(id+"F0.wireOp",EDGE,"E316"),sQuery(id+"F0.wireOp",EDGE,"E317"),sQuery(id+"F0.wireOp",EDGE,"E318"),sQuery(id+"F0.wireOp",EDGE,"E319"),sQuery(id+"F0.wireOp",EDGE,"E320"),sQuery(id+"F0.wireOp",EDGE,"E321"),sQuery(id+"F0.wireOp",EDGE,"E322"),sQuery(id+"F0.wireOp",EDGE,"E323"),sQuery(id+"F0.wireOp",EDGE,"E324"),sQuery(id+"F0.wireOp",EDGE,"E325"),sQuery(id+"F0.wireOp",EDGE,"E326"),sQuery(id+"F0.wireOp",EDGE,"E327"),sQuery(id+"F0.wireOp",EDGE,"E328"),sQuery(id+"F0.wireOp",EDGE,"E329"),sQuery(id+"F0.wireOp",EDGE,"E330"),sQuery(id+"F0.wireOp",EDGE,"E331"),sQuery(id+"F0.wireOp",EDGE,"E332"),sQuery(id+"F0.wireOp",EDGE,"E333"),sQuery(id+"F0.wireOp",EDGE,"E334"),sQuery(id+"F0.wireOp",EDGE,"E335"),sQuery(id+"F0.wireOp",EDGE,"E336"),sQuery(id+"F0.wireOp",EDGE,"E337"),sQuery(id+"F0.wireOp",EDGE,"E338"),sQuery(id+"F0.wireOp",EDGE,"E339"),sQuery(id+"F0.wireOp",EDGE,"E340"),sQuery(id+"F0.wireOp",EDGE,"E341"),sQuery(id+"F0.wireOp",EDGE,"E342"),sQuery(id+"F0.wireOp",EDGE,"E343"),sQuery(id+"F0.wireOp",EDGE,"E344"),sQuery(id+"F0.wireOp",EDGE,"E345"),sQuery(id+"F0.wireOp",EDGE,"E346"),sQuery(id+"F0.wireOp",EDGE,"E347"),sQuery(id+"F0.wireOp",EDGE,"E348"),sQuery(id+"F0.wireOp",EDGE,"E349"),sQuery(id+"F0.wireOp",EDGE,"E350"),sQuery(id+"F0.wireOp",EDGE,"E351"),sQuery(id+"F0.wireOp",EDGE,"E352"),sQuery(id+"F0.wireOp",EDGE,"E353"),sQuery(id+"F0.wireOp",EDGE,"E354"),sQuery(id+"F0.wireOp",EDGE,"E355"),sQuery(id+"F0.wireOp",EDGE,"E356"),sQuery(id+"F0.wireOp",EDGE,"E357"),sQuery(id+"F0.wireOp",EDGE,"E358"),sQuery(id+"F0.wireOp",EDGE,"E359"),sQuery(id+"F0.wireOp",EDGE,"E360"),sQuery(id+"F0.wireOp",EDGE,"E361"),sQuery(id+"F0.wireOp",EDGE,"E362"),sQuery(id+"F0.wireOp",EDGE,"E363"),sQuery(id+"F0.wireOp",EDGE,"E364"),sQuery(id+"F0.wireOp",EDGE,"E365"),sQuery(id+"F0.wireOp",EDGE,"E366"),sQuery(id+"F0.wireOp",EDGE,"E367"),sQuery(id+"F0.wireOp",EDGE,"E368"),sQuery(id+"F0.wireOp",EDGE,"E369"),sQuery(id+"F0.wireOp",EDGE,"E370"),sQuery(id+"F0.wireOp",EDGE,"E371"),sQuery(id+"F0.wireOp",EDGE,"E372"),sQuery(id+"F0.wireOp",EDGE,"E373"),sQuery(id+"F0.wireOp",EDGE,"E374"),sQuery(id+"F0.wireOp",EDGE,"E375"),sQuery(id+"F0.wireOp",EDGE,"E376"),sQuery(id+"F0.wireOp",EDGE,"E377"),sQuery(id+"F0.wireOp",EDGE,"E378"),sQuery(id+"F0.wireOp",EDGE,"E379"),sQuery(id+"F0.wireOp",EDGE,"E380"),sQuery(id+"F0.wireOp",EDGE,"E381"),sQuery(id+"F0.wireOp",EDGE,"E382"),sQuery(id+"F0.wireOp",EDGE,"E383"),sQuery(id+"F0.wireOp",EDGE,"E384"),sQuery(id+"F0.wireOp",EDGE,"E385"),sQuery(id+"F0.wireOp",EDGE,"E386"),sQuery(id+"F0.wireOp",EDGE,"E387"),sQuery(id+"F0.wireOp",EDGE,"E388"),sQuery(id+"F0.wireOp",EDGE,"E389"),sQuery(id+"F0.wireOp",EDGE,"E390"),sQuery(id+"F0.wireOp",EDGE,"E391"),sQuery(id+"F0.wireOp",EDGE,"E392"),sQuery(id+"F0.wireOp",EDGE,"E393"),sQuery(id+"F0.wireOp",EDGE,"E394"),sQuery(id+"F0.wireOp",EDGE,"E395"),sQuery(id+"F0.wireOp",EDGE,"E396"),sQuery(id+"F0.wireOp",EDGE,"E397"),sQuery(id+"F0.wireOp",EDGE,"E398"),sQuery(id+"F0.wireOp",EDGE,"E399"),sQuery(id+"F0.wireOp",EDGE,"E400"),sQuery(id+"F0.wireOp",EDGE,"E401"),sQuery(id+"F0.wireOp",EDGE,"E402"),sQuery(id+"F0.wireOp",EDGE,"E403"),sQuery(id+"F0.wireOp",EDGE,"E404"),sQuery(id+"F0.wireOp",EDGE,"E405"),sQuery(id+"F0.wireOp",EDGE,"E406"),sQuery(id+"F0.wireOp",EDGE,"E407"),sQuery(id+"F0.wireOp",EDGE,"E408"),sQuery(id+"F0.wireOp",EDGE,"E409"),sQuery(id+"F0.wireOp",EDGE,"E410"),sQuery(id+"F0.wireOp",EDGE,"E411"),sQuery(id+"F0.wireOp",EDGE,"E412"),sQuery(id+"F0.wireOp",EDGE,"E413"),sQuery(id+"F0.wireOp",EDGE,"E414"),sQuery(id+"F0.wireOp",EDGE,"E415"),sQuery(id+"F0.wireOp",EDGE,"E416"),sQuery(id+"F0.wireOp",EDGE,"E417"),sQuery(id+"F0.wireOp",EDGE,"E418"),sQuery(id+"F0.wireOp",EDGE,"E419"),sQuery(id+"F0.wireOp",EDGE,"E420"),sQuery(id+"F0.wireOp",EDGE,"E421"),sQuery(id+"F0.wireOp",EDGE,"E422"),sQuery(id+"F0.wireOp",EDGE,"E423"),sQuery(id+"F0.wireOp",EDGE,"E424"),sQuery(id+"F0.wireOp",EDGE,"E425"),sQuery(id+"F0.wireOp",EDGE,"E426"),sQuery(id+"F0.wireOp",EDGE,"E427"),sQuery(id+"F0.wireOp",EDGE,"E428"),sQuery(id+"F0.wireOp",EDGE,"E429"),sQuery(id+"F0.wireOp",EDGE,"E430"),sQuery(id+"F0.wireOp",EDGE,"E431"),sQuery(id+"F0.wireOp",EDGE,"E432"),sQuery(id+"F0.wireOp",EDGE,"E433"),sQuery(id+"F0.wireOp",EDGE,"E434"),sQuery(id+"F0.wireOp",EDGE,"E435"),sQuery(id+"F0.wireOp",EDGE,"E436"),sQuery(id+"F0.wireOp",EDGE,"E437"),sQuery(id+"F0.wireOp",EDGE,"E438"),sQuery(id+"F0.wireOp",EDGE,"E439"),sQuery(id+"F0.wireOp",EDGE,"E440"),sQuery(id+"F0.wireOp",EDGE,"E441"),sQuery(id+"F0.wireOp",EDGE,"E442"),sQuery(id+"F0.wireOp",EDGE,"E443"),sQuery(id+"F0.wireOp",EDGE,"E444"),sQuery(id+"F0.wireOp",EDGE,"E445"),sQuery(id+"F0.wireOp",EDGE,"E446"),sQuery(id+"F0.wireOp",EDGE,"E447"),sQuery(id+"F0.wireOp",EDGE,"E448"),sQuery(id+"F0.wireOp",EDGE,"E449"),sQuery(id+"F0.wireOp",EDGE,"E450"),sQuery(id+"F0.wireOp",EDGE,"E451"),sQuery(id+"F0.wireOp",EDGE,"E452"),sQuery(id+"F0.wireOp",EDGE,"E453"),sQuery(id+"F0.wireOp",EDGE,"E454"),sQuery(id+"F0.wireOp",EDGE,"E455"),sQuery(id+"F0.wireOp",EDGE,"E456"),sQuery(id+"F0.wireOp",EDGE,"E457"),sQuery(id+"F0.wireOp",EDGE,"E458"),sQuery(id+"F0.wireOp",EDGE,"E459"),sQuery(id+"F0.wireOp",EDGE,"E460"),sQuery(id+"F0.wireOp",EDGE,"E461"),sQuery(id+"F0.wireOp",EDGE,"E462"),sQuery(id+"F0.wireOp",EDGE,"E463"),sQuery(id+"F0.wireOp",EDGE,"E464"),sQuery(id+"F0.wireOp",EDGE,"E465"),sQuery(id+"F0.wireOp",EDGE,"E466"),sQuery(id+"F0.wireOp",EDGE,"E467"),sQuery(id+"F0.wireOp",EDGE,"E468"),sQuery(id+"F0.wireOp",EDGE,"E469"),sQuery(id+"F0.wireOp",EDGE,"E470"),sQuery(id+"F0.wireOp",EDGE,"E471"),sQuery(id+"F0.wireOp",EDGE,"E472"),sQuery(id+"F0.wireOp",EDGE,"E473"),sQuery(id+"F0.wireOp",EDGE,"E474"),sQuery(id+"F0.wireOp",EDGE,"E475"),sQuery(id+"F0.wireOp",EDGE,"E476"),sQuery(id+"F0.wireOp",EDGE,"E477"),sQuery(id+"F0.wireOp",EDGE,"E478"),sQuery(id+"F0.wireOp",EDGE,"E479"),sQuery(id+"F0.wireOp",EDGE,"E480"),sQuery(id+"F0.wireOp",EDGE,"E481"),sQuery(id+"F0.wireOp",EDGE,"E482"),sQuery(id+"F0.wireOp",EDGE,"E483"),sQuery(id+"F0.wireOp",EDGE,"E484"),sQuery(id+"F0.wireOp",EDGE,"E485"),sQuery(id+"F0.wireOp",EDGE,"E486"),sQuery(id+"F0.wireOp",EDGE,"E487"),sQuery(id+"F0.wireOp",EDGE,"E488"),sQuery(id+"F0.wireOp",EDGE,"E489"),sQuery(id+"F0.wireOp",EDGE,"E490"),sQuery(id+"F0.wireOp",EDGE,"E491"),sQuery(id+"F0.wireOp",EDGE,"E492"),sQuery(id+"F0.wireOp",EDGE,"E493"),sQuery(id+"F0.wireOp",EDGE,"E494"),sQuery(id+"F0.wireOp",EDGE,"E495"),sQuery(id+"F0.wireOp",EDGE,"E496"),sQuery(id+"F0.wireOp",EDGE,"E497"),sQuery(id+"F0.wireOp",EDGE,"E498"),sQuery(id+"F0.wireOp",EDGE,"E499"),sQuery(id+"F0.wireOp",EDGE,"E500"),sQuery(id+"F0.wireOp",EDGE,"E501"),sQuery(id+"F0.wireOp",EDGE,"E502"),sQuery(id+"F0.wireOp",EDGE,"E503"),sQuery(id+"F0.wireOp",EDGE,"E504"),sQuery(id+"F0.wireOp",EDGE,"E505"),sQuery(id+"F0.wireOp",EDGE,"E506"),sQuery(id+"F0.wireOp",EDGE,"E507"),sQuery(id+"F0.wireOp",EDGE,"E508"),sQuery(id+"F0.wireOp",EDGE,"E509"),sQuery(id+"F0.wireOp",EDGE,"E510"),sQuery(id+"F0.wireOp",EDGE,"E511"),sQuery(id+"F0.wireOp",EDGE,"E512"),sQuery(id+"F0.wireOp",EDGE,"E513"),sQuery(id+"F0.wireOp",EDGE,"E514"),sQuery(id+"F0.wireOp",EDGE,"E515"),sQuery(id+"F0.wireOp",EDGE,"E516"),sQuery(id+"F0.wireOp",EDGE,"E517"),sQuery(id+"F0.wireOp",EDGE,"E518"),sQuery(id+"F0.wireOp",EDGE,"E519"),sQuery(id+"F0.wireOp",EDGE,"E520"),sQuery(id+"F0.wireOp",EDGE,"E521"),sQuery(id+"F0.wireOp",EDGE,"E522"),sQuery(id+"F0.wireOp",EDGE,"E523"),sQuery(id+"F0.wireOp",EDGE,"E524"),sQuery(id+"F0.wireOp",EDGE,"E525"),sQuery(id+"F0.wireOp",EDGE,"E526"),sQuery(id+"F0.wireOp",EDGE,"E527"),sQuery(id+"F0.wireOp",EDGE,"E528"),sQuery(id+"F0.wireOp",EDGE,"E529"),sQuery(id+"F0.wireOp",EDGE,"E530"),sQuery(id+"F0.wireOp",EDGE,"E531"),sQuery(id+"F0.wireOp",EDGE,"E532"),sQuery(id+"F0.wireOp",EDGE,"E533"),sQuery(id+"F0.wireOp",EDGE,"E534"),sQuery(id+"F0.wireOp",EDGE,"E535"),sQuery(id+"F0.wireOp",EDGE,"E536"),sQuery(id+"F0.wireOp",EDGE,"E537"),sQuery(id+"F0.wireOp",EDGE,"E538"),sQuery(id+"F0.wireOp",EDGE,"E539"),sQuery(id+"F0.wireOp",EDGE,"E540"),sQuery(id+"F0.wireOp",EDGE,"E541"),sQuery(id+"F0.wireOp",EDGE,"E542"),sQuery(id+"F0.wireOp",EDGE,"E543"),sQuery(id+"F0.wireOp",EDGE,"E544"),sQuery(id+"F0.wireOp",EDGE,"E545"),sQuery(id+"F0.wireOp",EDGE,"E546"),sQuery(id+"F0.wireOp",EDGE,"E547"),sQuery(id+"F0.wireOp",EDGE,"E548"),sQuery(id+"F0.wireOp",EDGE,"E549"),sQuery(id+"F0.wireOp",EDGE,"E550"),sQuery(id+"F0.wireOp",EDGE,"E551"),sQuery(id+"F0.wireOp",EDGE,"E552"),sQuery(id+"F0.wireOp",EDGE,"E553"),sQuery(id+"F0.wireOp",EDGE,"E554"),sQuery(id+"F0.wireOp",EDGE,"E555"),sQuery(id+"F0.wireOp",EDGE,"E556"),sQuery(id+"F0.wireOp",EDGE,"E557"),sQuery(id+"F0.wireOp",EDGE,"E558"),sQuery(id+"F0.wireOp",EDGE,"E559"),sQuery(id+"F0.wireOp",EDGE,"E560"),sQuery(id+"F0.wireOp",EDGE,"E561"),sQuery(id+"F0.wireOp",EDGE,"E562"),sQuery(id+"F0.wireOp",EDGE,"E563"),sQuery(id+"F0.wireOp",EDGE,"E564"),sQuery(id+"F0.wireOp",EDGE,"E565"),sQuery(id+"F0.wireOp",EDGE,"E566"),sQuery(id+"F0.wireOp",EDGE,"E567"),sQuery(id+"F0.wireOp",EDGE,"E568"),sQuery(id+"F0.wireOp",EDGE,"E569"),sQuery(id+"F0.wireOp",EDGE,"E570"),sQuery(id+"F0.wireOp",EDGE,"E571"),sQuery(id+"F0.wireOp",EDGE,"E572"),sQuery(id+"F0.wireOp",EDGE,"E573"),sQuery(id+"F0.wireOp",EDGE,"E574"),sQuery(id+"F0.wireOp",EDGE,"E575"),sQuery(id+"F0.wireOp",EDGE,"E576"),sQuery(id+"F0.wireOp",EDGE,"E577"),sQuery(id+"F0.wireOp",EDGE,"E578"),sQuery(id+"F0.wireOp",EDGE,"E579"),sQuery(id+"F0.wireOp",EDGE,"E580"),sQuery(id+"F0.wireOp",EDGE,"E581"),sQuery(id+"F0.wireOp",EDGE,"E582"),sQuery(id+"F0.wireOp",EDGE,"E583"),sQuery(id+"F0.wireOp",EDGE,"E584"),sQuery(id+"F0.wireOp",EDGE,"E585"),sQuery(id+"F0.wireOp",EDGE,"E586"),sQuery(id+"F0.wireOp",EDGE,"E587"),sQuery(id+"F0.wireOp",EDGE,"E588"),sQuery(id+"F0.wireOp",EDGE,"E589"),sQuery(id+"F0.wireOp",EDGE,"E590"),sQuery(id+"F0.wireOp",EDGE,"E591"),sQuery(id+"F0.wireOp",EDGE,"E592"),sQuery(id+"F0.wireOp",EDGE,"E593"),sQuery(id+"F0.wireOp",EDGE,"E594"),sQuery(id+"F0.wireOp",EDGE,"E595"),sQuery(id+"F0.wireOp",EDGE,"E596"),sQuery(id+"F0.wireOp",EDGE,"E597"),sQuery(id+"F0.wireOp",EDGE,"E598"),sQuery(id+"F0.wireOp",EDGE,"E599"),sQuery(id+"F0.wireOp",EDGE,"E600"),sQuery(id+"F0.wireOp",EDGE,"E601"),sQuery(id+"F0.wireOp",EDGE,"E602"),sQuery(id+"F0.wireOp",EDGE,"E603"),sQuery(id+"F0.wireOp",EDGE,"E604"),sQuery(id+"F0.wireOp",EDGE,"E605"),sQuery(id+"F0.wireOp",EDGE,"E606"),sQuery(id+"F0.wireOp",EDGE,"E607"),sQuery(id+"F0.wireOp",EDGE,"E608"),sQuery(id+"F0.wireOp",EDGE,"E609"),sQuery(id+"F0.wireOp",EDGE,"E610"),sQuery(id+"F0.wireOp",EDGE,"E611"),sQuery(id+"F0.wireOp",EDGE,"E612"),sQuery(id+"F0.wireOp",EDGE,"E613"),sQuery(id+"F0.wireOp",EDGE,"E614"),sQuery(id+"F0.wireOp",EDGE,"E615"),sQuery(id+"F0.wireOp",EDGE,"E616"),sQuery(id+"F0.wireOp",EDGE,"E617"),sQuery(id+"F0.wireOp",EDGE,"E618"),sQuery(id+"F0.wireOp",EDGE,"E619"),sQuery(id+"F0.wireOp",EDGE,"E620"),sQuery(id+"F0.wireOp",EDGE,"E621"),sQuery(id+"F0.wireOp",EDGE,"E622"),sQuery(id+"F0.wireOp",EDGE,"E623"),sQuery(id+"F0.wireOp",EDGE,"E624"),sQuery(id+"F0.wireOp",EDGE,"E625"),sQuery(id+"F0.wireOp",EDGE,"E626"),sQuery(id+"F0.wireOp",EDGE,"E627"),sQuery(id+"F0.wireOp",EDGE,"E628"),sQuery(id+"F0.wireOp",EDGE,"E629"),sQuery(id+"F0.wireOp",EDGE,"E630"),sQuery(id+"F0.wireOp",EDGE,"E631"),sQuery(id+"F0.wireOp",EDGE,"E632"),sQuery(id+"F0.wireOp",EDGE,"E633"),sQuery(id+"F0.wireOp",EDGE,"E634"),sQuery(id+"F0.wireOp",EDGE,"E635"),sQuery(id+"F0.wireOp",EDGE,"E636"),sQuery(id+"F0.wireOp",EDGE,"E637"),sQuery(id+"F0.wireOp",EDGE,"E638"),sQuery(id+"F0.wireOp",EDGE,"E639"),sQuery(id+"F0.wireOp",EDGE,"E640"),sQuery(id+"F0.wireOp",EDGE,"E641"),sQuery(id+"F0.wireOp",EDGE,"E642"),sQuery(id+"F0.wireOp",EDGE,"E643"),sQuery(id+"F0.wireOp",EDGE,"E644"),sQuery(id+"F0.wireOp",EDGE,"E645"),sQuery(id+"F0.wireOp",EDGE,"E646"),sQuery(id+"F0.wireOp",EDGE,"E647"),sQuery(id+"F0.wireOp",EDGE,"E648"),sQuery(id+"F0.wireOp",EDGE,"E649"),sQuery(id+"F0.wireOp",EDGE,"E650"),sQuery(id+"F0.wireOp",EDGE,"E651"),sQuery(id+"F0.wireOp",EDGE,"E652"),sQuery(id+"F0.wireOp",EDGE,"E653"),sQuery(id+"F0.wireOp",EDGE,"E654"),sQuery(id+"F0.wireOp",EDGE,"E655"),sQuery(id+"F0.wireOp",EDGE,"E656"),sQuery(id+"F0.wireOp",EDGE,"E657"),sQuery(id+"F0.wireOp",EDGE,"E658"),sQuery(id+"F0.wireOp",EDGE,"E659"),sQuery(id+"F0.wireOp",EDGE,"E660"),sQuery(id+"F0.wireOp",EDGE,"E661"),sQuery(id+"F0.wireOp",EDGE,"E662"),sQuery(id+"F0.wireOp",EDGE,"E663"),sQuery(id+"F0.wireOp",EDGE,"E664"),sQuery(id+"F0.wireOp",EDGE,"E665"),sQuery(id+"F0.wireOp",EDGE,"E666"),sQuery(id+"F0.wireOp",EDGE,"E667"),sQuery(id+"F0.wireOp",EDGE,"E668"),sQuery(id+"F0.wireOp",EDGE,"E669"),sQuery(id+"F0.wireOp",EDGE,"E670"),sQuery(id+"F0.wireOp",EDGE,"E671"),sQuery(id+"F0.wireOp",EDGE,"E672"),sQuery(id+"F0.wireOp",EDGE,"E673"),sQuery(id+"F0.wireOp",EDGE,"E674"),sQuery(id+"F0.wireOp",EDGE,"E675"),sQuery(id+"F0.wireOp",EDGE,"E676"),sQuery(id+"F0.wireOp",EDGE,"E677"),sQuery(id+"F0.wireOp",EDGE,"E678"),sQuery(id+"F0.wireOp",EDGE,"E679"),sQuery(id+"F0.wireOp",EDGE,"E680"),sQuery(id+"F0.wireOp",EDGE,"E681"),sQuery(id+"F0.wireOp",EDGE,"E682"),sQuery(id+"F0.wireOp",EDGE,"E683"),sQuery(id+"F0.wireOp",EDGE,"E684"),sQuery(id+"F0.wireOp",EDGE,"E685"),sQuery(id+"F0.wireOp",EDGE,"E686"),sQuery(id+"F0.wireOp",EDGE,"E687"),sQuery(id+"F0.wireOp",EDGE,"E688"),sQuery(id+"F0.wireOp",EDGE,"E689"),sQuery(id+"F0.wireOp",EDGE,"E690"),sQuery(id+"F0.wireOp",EDGE,"E691"),sQuery(id+"F0.wireOp",EDGE,"E692"),sQuery(id+"F0.wireOp",EDGE,"E693"),sQuery(id+"F0.wireOp",EDGE,"E694"),sQuery(id+"F0.wireOp",EDGE,"E695"),sQuery(id+"F0.wireOp",EDGE,"E696"),sQuery(id+"F0.wireOp",EDGE,"E697"),sQuery(id+"F0.wireOp",EDGE,"E698"),sQuery(id+"F0.wireOp",EDGE,"E699"),sQuery(id+"F0.wireOp",EDGE,"E700"),sQuery(id+"F0.wireOp",EDGE,"E701"),sQuery(id+"F0.wireOp",EDGE,"E702"),sQuery(id+"F0.wireOp",EDGE,"E703"),sQuery(id+"F0.wireOp",EDGE,"E704"),sQuery(id+"F0.wireOp",EDGE,"E705"),sQuery(id+"F0.wireOp",EDGE,"E706"),sQuery(id+"F0.wireOp",EDGE,"E707"),sQuery(id+"F0.wireOp",EDGE,"E708"),sQuery(id+"F0.wireOp",EDGE,"E709"),sQuery(id+"F0.wireOp",EDGE,"E710"),sQuery(id+"F0.wireOp",EDGE,"E711"),sQuery(id+"F0.wireOp",EDGE,"E712"),sQuery(id+"F0.wireOp",EDGE,"E713"),sQuery(id+"F0.wireOp",EDGE,"E714"),sQuery(id+"F0.wireOp",EDGE,"E715"),sQuery(id+"F0.wireOp",EDGE,"E716"),sQuery(id+"F0.wireOp",EDGE,"E717"),sQuery(id+"F0.wireOp",EDGE,"E718"),sQuery(id+"F0.wireOp",EDGE,"E719"),sQuery(id+"F0.wireOp",EDGE,"E720"),sQuery(id+"F0.wireOp",EDGE,"E721"),sQuery(id+"F0.wireOp",EDGE,"E722"),sQuery(id+"F0.wireOp",EDGE,"E723"),sQuery(id+"F0.wireOp",EDGE,"E724"),sQuery(id+"F0.wireOp",EDGE,"E725"),sQuery(id+"F0.wireOp",EDGE,"E726"),sQuery(id+"F0.wireOp",EDGE,"E727"),sQuery(id+"F0.wireOp",EDGE,"E728"),sQuery(id+"F0.wireOp",EDGE,"E729"),sQuery(id+"F0.wireOp",EDGE,"E730"),sQuery(id+"F0.wireOp",EDGE,"E731"),sQuery(id+"F0.wireOp",EDGE,"E732"),sQuery(id+"F0.wireOp",EDGE,"E733"),sQuery(id+"F0.wireOp",EDGE,"E734"),sQuery(id+"F0.wireOp",EDGE,"E735"),sQuery(id+"F0.wireOp",EDGE,"E736"),sQuery(id+"F0.wireOp",EDGE,"E737"),sQuery(id+"F0.wireOp",EDGE,"E738"),sQuery(id+"F0.wireOp",EDGE,"E739"),sQuery(id+"F0.wireOp",EDGE,"E740"),sQuery(id+"F0.wireOp",EDGE,"E741"),sQuery(id+"F0.wireOp",EDGE,"E742"),sQuery(id+"F0.wireOp",EDGE,"E743"),sQuery(id+"F0.wireOp",EDGE,"E744"),sQuery(id+"F0.wireOp",EDGE,"E745"),sQuery(id+"F0.wireOp",EDGE,"E746"),sQuery(id+"F0.wireOp",EDGE,"E747"),sQuery(id+"F0.wireOp",EDGE,"E748"),sQuery(id+"F0.wireOp",EDGE,"E749"),sQuery(id+"F0.wireOp",EDGE,"E750"),sQuery(id+"F0.wireOp",EDGE,"E751"),sQuery(id+"F0.wireOp",EDGE,"E752"),sQuery(id+"F0.wireOp",EDGE,"E753"),sQuery(id+"F0.wireOp",EDGE,"E754"),sQuery(id+"F0.wireOp",EDGE,"E755"),sQuery(id+"F0.wireOp",EDGE,"E756"),sQuery(id+"F0.wireOp",EDGE,"E757"),sQuery(id+"F0.wireOp",EDGE,"E758"),sQuery(id+"F0.wireOp",EDGE,"E759"),sQuery(id+"F0.wireOp",EDGE,"E760"),sQuery(id+"F0.wireOp",EDGE,"E761"),sQuery(id+"F0.wireOp",EDGE,"E762"),sQuery(id+"F0.wireOp",EDGE,"E763"),sQuery(id+"F0.wireOp",EDGE,"E764"),sQuery(id+"F0.wireOp",EDGE,"E765"),sQuery(id+"F0.wireOp",EDGE,"E766"),sQuery(id+"F0.wireOp",EDGE,"E767"),sQuery(id+"F0.wireOp",EDGE,"E768"),sQuery(id+"F0.wireOp",EDGE,"E769"),sQuery(id+"F0.wireOp",EDGE,"E770"),sQuery(id+"F0.wireOp",EDGE,"E771"),sQuery(id+"F0.wireOp",EDGE,"E772"),sQuery(id+"F0.wireOp",EDGE,"E773"),sQuery(id+"F0.wireOp",EDGE,"E774"),sQuery(id+"F0.wireOp",EDGE,"E775"),sQuery(id+"F0.wireOp",EDGE,"E776"),sQuery(id+"F0.wireOp",EDGE,"E777"),sQuery(id+"F0.wireOp",EDGE,"E778"),sQuery(id+"F0.wireOp",EDGE,"E779"),sQuery(id+"F0.wireOp",EDGE,"E780"),sQuery(id+"F0.wireOp",EDGE,"E781"),sQuery(id+"F0.wireOp",EDGE,"E782"),sQuery(id+"F0.wireOp",EDGE,"E783"),sQuery(id+"F0.wireOp",EDGE,"E784"),sQuery(id+"F0.wireOp",EDGE,"E785"),sQuery(id+"F0.wireOp",EDGE,"E786"),sQuery(id+"F0.wireOp",EDGE,"E787"),sQuery(id+"F0.wireOp",EDGE,"E788"),sQuery(id+"F0.wireOp",EDGE,"E789"),sQuery(id+"F0.wireOp",EDGE,"E790"),sQuery(id+"F0.wireOp",EDGE,"E791"),sQuery(id+"F0.wireOp",EDGE,"E792"),sQuery(id+"F0.wireOp",EDGE,"E793"),sQuery(id+"F0.wireOp",EDGE,"E794"),sQuery(id+"F0.wireOp",EDGE,"E795"),sQuery(id+"F0.wireOp",EDGE,"E796"),sQuery(id+"F0.wireOp",EDGE,"E797"),sQuery(id+"F0.wireOp",EDGE,"E798"),sQuery(id+"F0.wireOp",EDGE,"E799"),sQuery(id+"F0.wireOp",EDGE,"E800"),sQuery(id+"F0.wireOp",EDGE,"E801"),sQuery(id+"F0.wireOp",EDGE,"E802"),sQuery(id+"F0.wireOp",EDGE,"E803"),sQuery(id+"F0.wireOp",EDGE,"E804"),sQuery(id+"F0.wireOp",EDGE,"E805"),sQuery(id+"F0.wireOp",EDGE,"E806"),sQuery(id+"F0.wireOp",EDGE,"E807"),sQuery(id+"F0.wireOp",EDGE,"E808"),sQuery(id+"F0.wireOp",EDGE,"E809"),sQuery(id+"F0.wireOp",EDGE,"E810"),sQuery(id+"F0.wireOp",EDGE,"E811"),sQuery(id+"F0.wireOp",EDGE,"E812"),sQuery(id+"F0.wireOp",EDGE,"E813"),sQuery(id+"F0.wireOp",EDGE,"E814"),sQuery(id+"F0.wireOp",EDGE,"E815"),sQuery(id+"F0.wireOp",EDGE,"E816"),sQuery(id+"F0.wireOp",EDGE,"E817"),sQuery(id+"F0.wireOp",EDGE,"E818"),sQuery(id+"F0.wireOp",EDGE,"E819"),sQuery(id+"F0.wireOp",EDGE,"E820"),sQuery(id+"F0.wireOp",EDGE,"E821"),sQuery(id+"F0.wireOp",EDGE,"E822"),sQuery(id+"F0.wireOp",EDGE,"E823"),sQuery(id+"F0.wireOp",EDGE,"E824"),sQuery(id+"F0.wireOp",EDGE,"E825"),sQuery(id+"F0.wireOp",EDGE,"E826"),sQuery(id+"F0.wireOp",EDGE,"E827"),sQuery(id+"F0.wireOp",EDGE,"E828"),sQuery(id+"F0.wireOp",EDGE,"E829"),sQuery(id+"F0.wireOp",EDGE,"E830"),sQuery(id+"F0.wireOp",EDGE,"E831"),sQuery(id+"F0.wireOp",EDGE,"E832"),sQuery(id+"F0.wireOp",EDGE,"E833"),sQuery(id+"F0.wireOp",EDGE,"E834"),sQuery(id+"F0.wireOp",EDGE,"E835"),sQuery(id+"F0.wireOp",EDGE,"E836"),sQuery(id+"F0.wireOp",EDGE,"E837"),sQuery(id+"F0.wireOp",EDGE,"E838"),sQuery(id+"F0.wireOp",EDGE,"E839"),sQuery(id+"F0.wireOp",EDGE,"E840"),sQuery(id+"F0.wireOp",EDGE,"E841"),sQuery(id+"F0.wireOp",EDGE,"E842"),sQuery(id+"F0.wireOp",EDGE,"E843"),sQuery(id+"F0.wireOp",EDGE,"E844"),sQuery(id+"F0.wireOp",EDGE,"E845"),sQuery(id+"F0.wireOp",EDGE,"E846"),sQuery(id+"F0.wireOp",EDGE,"E847"),sQuery(id+"F0.wireOp",EDGE,"E848"),sQuery(id+"F0.wireOp",EDGE,"E849"),sQuery(id+"F0.wireOp",EDGE,"E850"),sQuery(id+"F0.wireOp",EDGE,"E851"),sQuery(id+"F0.wireOp",EDGE,"E852"),sQuery(id+"F0.wireOp",EDGE,"E853"),sQuery(id+"F0.wireOp",EDGE,"E854"),sQuery(id+"F0.wireOp",EDGE,"E855"),sQuery(id+"F0.wireOp",EDGE,"E856"),sQuery(id+"F0.wireOp",EDGE,"E857"),sQuery(id+"F0.wireOp",EDGE,"E858"),sQuery(id+"F0.wireOp",EDGE,"E859"),sQuery(id+"F0.wireOp",EDGE,"E860"),sQuery(id+"F0.wireOp",EDGE,"E861"),sQuery(id+"F0.wireOp",EDGE,"E862"),sQuery(id+"F0.wireOp",EDGE,"E863"),sQuery(id+"F0.wireOp",EDGE,"E864"),sQuery(id+"F0.wireOp",EDGE,"E865"),sQuery(id+"F0.wireOp",EDGE,"E866"),sQuery(id+"F0.wireOp",EDGE,"E867"),sQuery(id+"F0.wireOp",EDGE,"E868"),sQuery(id+"F0.wireOp",EDGE,"E869"),sQuery(id+"F0.wireOp",EDGE,"E870"),sQuery(id+"F0.wireOp",EDGE,"E871"),sQuery(id+"F0.wireOp",EDGE,"E872"),sQuery(id+"F0.wireOp",EDGE,"E873"),sQuery(id+"F0.wireOp",EDGE,"E874"),sQuery(id+"F0.wireOp",EDGE,"E875"),sQuery(id+"F0.wireOp",EDGE,"E876"),sQuery(id+"F0.wireOp",EDGE,"E877"),sQuery(id+"F0.wireOp",EDGE,"E878"),sQuery(id+"F0.wireOp",EDGE,"E879"),sQuery(id+"F0.wireOp",EDGE,"E880"),sQuery(id+"F0.wireOp",EDGE,"E881"),sQuery(id+"F0.wireOp",EDGE,"E882"),sQuery(id+"F0.wireOp",EDGE,"E883"),sQuery(id+"F0.wireOp",EDGE,"E884"),sQuery(id+"F0.wireOp",EDGE,"E885"),sQuery(id+"F0.wireOp",EDGE,"E886"),sQuery(id+"F0.wireOp",EDGE,"E887"),sQuery(id+"F0.wireOp",EDGE,"E888"),sQuery(id+"F0.wireOp",EDGE,"E889"),sQuery(id+"F0.wireOp",EDGE,"E890"),sQuery(id+"F0.wireOp",EDGE,"E891"),sQuery(id+"F0.wireOp",EDGE,"E892"),sQuery(id+"F0.wireOp",EDGE,"E893"),sQuery(id+"F0.wireOp",EDGE,"E894"),sQuery(id+"F0.wireOp",EDGE,"E895"),sQuery(id+"F0.wireOp",EDGE,"E896"),sQuery(id+"F0.wireOp",EDGE,"E897"),sQuery(id+"F0.wireOp",EDGE,"E898"),sQuery(id+"F0.wireOp",EDGE,"E899"),sQuery(id+"F0.wireOp",EDGE,"E900"),sQuery(id+"F0.wireOp",EDGE,"E901"),sQuery(id+"F0.wireOp",EDGE,"E902"),sQuery(id+"F0.wireOp",EDGE,"E903"),sQuery(id+"F0.wireOp",EDGE,"E904"),sQuery(id+"F0.wireOp",EDGE,"E905"),sQuery(id+"F0.wireOp",EDGE,"E906"),sQuery(id+"F0.wireOp",EDGE,"E907"),sQuery(id+"F0.wireOp",EDGE,"E908"),sQuery(id+"F0.wireOp",EDGE,"E909"),sQuery(id+"F0.wireOp",EDGE,"E910"),sQuery(id+"F0.wireOp",EDGE,"E911"),sQuery(id+"F0.wireOp",EDGE,"E912"),sQuery(id+"F0.wireOp",EDGE,"E913"),sQuery(id+"F0.wireOp",EDGE,"E914"),sQuery(id+"F0.wireOp",EDGE,"E915"),sQuery(id+"F0.wireOp",EDGE,"E916"),sQuery(id+"F0.wireOp",EDGE,"E917"),sQuery(id+"F0.wireOp",EDGE,"E918"),sQuery(id+"F0.wireOp",EDGE,"E919"),sQuery(id+"F0.wireOp",EDGE,"E920"),sQuery(id+"F0.wireOp",EDGE,"E921"),sQuery(id+"F0.wireOp",EDGE,"E922"),sQuery(id+"F0.wireOp",EDGE,"E923"),sQuery(id+"F0.wireOp",EDGE,"E924"),sQuery(id+"F0.wireOp",EDGE,"E925"),sQuery(id+"F0.wireOp",EDGE,"E926"),sQuery(id+"F0.wireOp",EDGE,"E927"),sQuery(id+"F0.wireOp",EDGE,"E928"),sQuery(id+"F0.wireOp",EDGE,"E929"),sQuery(id+"F0.wireOp",EDGE,"E930"),sQuery(id+"F0.wireOp",EDGE,"E931"),sQuery(id+"F0.wireOp",EDGE,"E932"),sQuery(id+"F0.wireOp",EDGE,"E933"),sQuery(id+"F0.wireOp",EDGE,"E934"),sQuery(id+"F0.wireOp",EDGE,"E935"),sQuery(id+"F0.wireOp",EDGE,"E936"),sQuery(id+"F0.wireOp",EDGE,"E937"),sQuery(id+"F0.wireOp",EDGE,"E938"),sQuery(id+"F0.wireOp",EDGE,"E939"),sQuery(id+"F0.wireOp",EDGE,"E940"),sQuery(id+"F0.wireOp",EDGE,"E941"),sQuery(id+"F0.wireOp",EDGE,"E942"),sQuery(id+"F0.wireOp",EDGE,"E943"),sQuery(id+"F0.wireOp",EDGE,"E944"),sQuery(id+"F0.wireOp",EDGE,"E945"),sQuery(id+"F0.wireOp",EDGE,"E946"),sQuery(id+"F0.wireOp",EDGE,"E947"),sQuery(id+"F0.wireOp",EDGE,"E948"),sQuery(id+"F0.wireOp",EDGE,"E949"),sQuery(id+"F0.wireOp",EDGE,"E950"),sQuery(id+"F0.wireOp",EDGE,"E951"),sQuery(id+"F0.wireOp",EDGE,"E952"),sQuery(id+"F0.wireOp",EDGE,"E953"),sQuery(id+"F0.wireOp",EDGE,"E954"),sQuery(id+"F0.wireOp",EDGE,"E955"),sQuery(id+"F0.wireOp",EDGE,"E956"),sQuery(id+"F0.wireOp",EDGE,"E957"),sQuery(id+"F0.wireOp",EDGE,"E958"),sQuery(id+"F0.wireOp",EDGE,"E959"),sQuery(id+"F0.wireOp",EDGE,"E960"),sQuery(id+"F0.wireOp",EDGE,"E961"),sQuery(id+"F0.wireOp",EDGE,"E962"),sQuery(id+"F0.wireOp",EDGE,"E963"),sQuery(id+"F0.wireOp",EDGE,"E964"),sQuery(id+"F0.wireOp",EDGE,"E965"),sQuery(id+"F0.wireOp",EDGE,"E966"),sQuery(id+"F0.wireOp",EDGE,"E967"),sQuery(id+"F0.wireOp",EDGE,"E968"),sQuery(id+"F0.wireOp",EDGE,"E969"),sQuery(id+"F0.wireOp",EDGE,"E970"),sQuery(id+"F0.wireOp",EDGE,"E971"),sQuery(id+"F0.wireOp",EDGE,"E972"),sQuery(id+"F0.wireOp",EDGE,"E973"),sQuery(id+"F0.wireOp",EDGE,"E974"),sQuery(id+"F0.wireOp",EDGE,"E975"),sQuery(id+"F0.wireOp",EDGE,"E976"),sQuery(id+"F0.wireOp",EDGE,"E977"),sQuery(id+"F0.wireOp",EDGE,"E978"),sQuery(id+"F0.wireOp",EDGE,"E979"),sQuery(id+"F0.wireOp",EDGE,"E980"),sQuery(id+"F0.wireOp",EDGE,"E981"),sQuery(id+"F0.wireOp",EDGE,"E982"),sQuery(id+"F0.wireOp",EDGE,"E983"),sQuery(id+"F0.wireOp",EDGE,"E984"),sQuery(id+"F0.wireOp",EDGE,"E985"),sQuery(id+"F0.wireOp",EDGE,"E986"),sQuery(id+"F0.wireOp",EDGE,"E987"),sQuery(id+"F0.wireOp",EDGE,"E988"),sQuery(id+"F0.wireOp",EDGE,"E989"),sQuery(id+"F0.wireOp",EDGE,"E990"),sQuery(id+"F0.wireOp",EDGE,"E991"),sQuery(id+"F0.wireOp",EDGE,"E992"),sQuery(id+"F0.wireOp",EDGE,"E993"),sQuery(id+"F0.wireOp",EDGE,"E994"),sQuery(id+"F0.wireOp",EDGE,"E995"),sQuery(id+"F0.wireOp",EDGE,"E996"),sQuery(id+"F0.wireOp",EDGE,"E997"),sQuery(id+"F0.wireOp",EDGE,"E998"),sQuery(id+"F0.wireOp",EDGE,"E999"),sQuery(id+"F0.wireOp",EDGE,"E1000"),sQuery(id+"F0.wireOp",EDGE,"E1001"),sQuery(id+"F0.wireOp",EDGE,"E1002"),sQuery(id+"F0.wireOp",EDGE,"E1003"),sQuery(id+"F0.wireOp",EDGE,"E1004"),sQuery(id+"F0.wireOp",EDGE,"E1005"),sQuery(id+"F0.wireOp",EDGE,"E1006"),sQuery(id+"F0.wireOp",EDGE,"E1007"),sQuery(id+"F0.wireOp",EDGE,"E1008"),sQuery(id+"F0.wireOp",EDGE,"E1009"),sQuery(id+"F0.wireOp",EDGE,"E1010"),sQuery(id+"F0.wireOp",EDGE,"E1011"),sQuery(id+"F0.wireOp",EDGE,"E1012"),sQuery(id+"F0.wireOp",EDGE,"E1013"),sQuery(id+"F0.wireOp",EDGE,"E1014"),sQuery(id+"F0.wireOp",EDGE,"E1015"),sQuery(id+"F0.wireOp",EDGE,"E1016"),sQuery(id+"F0.wireOp",EDGE,"E1017"),sQuery(id+"F0.wireOp",EDGE,"E1018"),sQuery(id+"F0.wireOp",EDGE,"E1019"),sQuery(id+"F0.wireOp",EDGE,"E1020"),sQuery(id+"F0.wireOp",EDGE,"E1021"),sQuery(id+"F0.wireOp",EDGE,"E1022"),sQuery(id+"F0.wireOp",EDGE,"E1023"),sQuery(id+"F0.wireOp",EDGE,"E1024"),sQuery(id+"F0.wireOp",EDGE,"E1025"),sQuery(id+"F0.wireOp",EDGE,"E1026"),sQuery(id+"F0.wireOp",EDGE,"E1027"),sQuery(id+"F0.wireOp",EDGE,"E1028"),sQuery(id+"F0.wireOp",EDGE,"E1029"),sQuery(id+"F0.wireOp",EDGE,"E1030"),sQuery(id+"F0.wireOp",EDGE,"E1031"),sQuery(id+"F0.wireOp",EDGE,"E1032"),sQuery(id+"F0.wireOp",EDGE,"E1033"),sQuery(id+"F0.wireOp",EDGE,"E1034"),sQuery(id+"F0.wireOp",EDGE,"E1035"),sQuery(id+"F0.wireOp",EDGE,"E1036"),sQuery(id+"F0.wireOp",EDGE,"E1037"),sQuery(id+"F0.wireOp",EDGE,"E1038"),sQuery(id+"F0.wireOp",EDGE,"E1039"),sQuery(id+"F0.wireOp",EDGE,"E1040"),sQuery(id+"F0.wireOp",EDGE,"E1041"),sQuery(id+"F0.wireOp",EDGE,"E1042"),sQuery(id+"F0.wireOp",EDGE,"E1043"),sQuery(id+"F0.wireOp",EDGE,"E1044"),sQuery(id+"F0.wireOp",EDGE,"E1045"),sQuery(id+"F0.wireOp",EDGE,"E1046"),sQuery(id+"F0.wireOp",EDGE,"E1047"),sQuery(id+"F0.wireOp",EDGE,"E1048"),sQuery(id+"F0.wireOp",EDGE,"E1049"),sQuery(id+"F0.wireOp",EDGE,"E1050"),sQuery(id+"F0.wireOp",EDGE,"E1051"),sQuery(id+"F0.wireOp",EDGE,"E1052"),sQuery(id+"F0.wireOp",EDGE,"E1053"),sQuery(id+"F0.wireOp",EDGE,"E1054"),sQuery(id+"F0.wireOp",EDGE,"E1055"),sQuery(id+"F0.wireOp",EDGE,"E1056"),sQuery(id+"F0.wireOp",EDGE,"E1057"),sQuery(id+"F0.wireOp",EDGE,"E1058"),sQuery(id+"F0.wireOp",EDGE,"E1059"),sQuery(id+"F0.wireOp",EDGE,"E1060"),sQuery(id+"F0.wireOp",EDGE,"E1061"),sQuery(id+"F0.wireOp",EDGE,"E1062"),sQuery(id+"F0.wireOp",EDGE,"E1063"),sQuery(id+"F0.wireOp",EDGE,"E1064"),sQuery(id+"F0.wireOp",EDGE,"E1065"),sQuery(id+"F0.wireOp",EDGE,"E1066"),sQuery(id+"F0.wireOp",EDGE,"E1067"),sQuery(id+"F0.wireOp",EDGE,"E1068"),sQuery(id+"F0.wireOp",EDGE,"E1069"),sQuery(id+"F0.wireOp",EDGE,"E1070"),sQuery(id+"F0.wireOp",EDGE,"E1071"),sQuery(id+"F0.wireOp",EDGE,"E1072"),sQuery(id+"F0.wireOp",EDGE,"E1073"),sQuery(id+"F0.wireOp",EDGE,"E1074"),sQuery(id+"F0.wireOp",EDGE,"E1075"),sQuery(id+"F0.wireOp",EDGE,"E1076"),sQuery(id+"F0.wireOp",EDGE,"E1077"),sQuery(id+"F0.wireOp",EDGE,"E1078"),sQuery(id+"F0.wireOp",EDGE,"E1079"),sQuery(id+"F0.wireOp",EDGE,"E1080"),sQuery(id+"F0.wireOp",EDGE,"E1081"),sQuery(id+"F0.wireOp",EDGE,"E1082"),sQuery(id+"F0.wireOp",EDGE,"E1083"),sQuery(id+"F0.wireOp",EDGE,"E1084"),sQuery(id+"F0.wireOp",EDGE,"E1085"),sQuery(id+"F0.wireOp",EDGE,"E1086"),sQuery(id+"F0.wireOp",EDGE,"E1087"),sQuery(id+"F0.wireOp",EDGE,"E1088"),sQuery(id+"F0.wireOp",EDGE,"E1089"),sQuery(id+"F0.wireOp",EDGE,"E1090"),sQuery(id+"F0.wireOp",EDGE,"E1091"),sQuery(id+"F0.wireOp",EDGE,"E1092"),sQuery(id+"F0.wireOp",EDGE,"E1093"),sQuery(id+"F0.wireOp",EDGE,"E1094"),sQuery(id+"F0.wireOp",EDGE,"E1095"),sQuery(id+"F0.wireOp",EDGE,"E1096"),sQuery(id+"F0.wireOp",EDGE,"E1097"),sQuery(id+"F0.wireOp",EDGE,"E1098"),sQuery(id+"F0.wireOp",EDGE,"E1099"),sQuery(id+"F0.wireOp",EDGE,"E1100"),sQuery(id+"F0.wireOp",EDGE,"E1101"),sQuery(id+"F0.wireOp",EDGE,"E1102"),sQuery(id+"F0.wireOp",EDGE,"E1103"),sQuery(id+"F0.wireOp",EDGE,"E1104"),sQuery(id+"F0.wireOp",EDGE,"E1105"),sQuery(id+"F0.wireOp",EDGE,"E1106"),sQuery(id+"F0.wireOp",EDGE,"E1107"),sQuery(id+"F0.wireOp",EDGE,"E1108"),sQuery(id+"F0.wireOp",EDGE,"E1109"),sQuery(id+"F0.wireOp",EDGE,"E1110"),sQuery(id+"F0.wireOp",EDGE,"E1111"),sQuery(id+"F0.wireOp",EDGE,"E1112"),sQuery(id+"F0.wireOp",EDGE,"E1113"),sQuery(id+"F0.wireOp",EDGE,"E1114"),sQuery(id+"F0.wireOp",EDGE,"E1115"),sQuery(id+"F0.wireOp",EDGE,"E1116"),sQuery(id+"F0.wireOp",EDGE,"E1117"),sQuery(id+"F0.wireOp",EDGE,"E1118"),sQuery(id+"F0.wireOp",EDGE,"E1119"),sQuery(id+"F0.wireOp",EDGE,"E1120"),sQuery(id+"F0.wireOp",EDGE,"E1121"),sQuery(id+"F0.wireOp",EDGE,"E1122"),sQuery(id+"F0.wireOp",EDGE,"E1123"),sQuery(id+"F0.wireOp",EDGE,"E1124"),sQuery(id+"F0.wireOp",EDGE,"E1125"),sQuery(id+"F0.wireOp",EDGE,"E1126"),sQuery(id+"F0.wireOp",EDGE,"E1127"),sQuery(id+"F0.wireOp",EDGE,"E1128"),sQuery(id+"F0.wireOp",EDGE,"E1129"),sQuery(id+"F0.wireOp",EDGE,"E1130"),sQuery(id+"F0.wireOp",EDGE,"E1131"),sQuery(id+"F0.wireOp",EDGE,"E1132"),sQuery(id+"F0.wireOp",EDGE,"E1133"),sQuery(id+"F0.wireOp",EDGE,"E1134"),sQuery(id+"F0.wireOp",EDGE,"E1135"),sQuery(id+"F0.wireOp",EDGE,"E1136"),sQuery(id+"F0.wireOp",EDGE,"E1137"),sQuery(id+"F0.wireOp",EDGE,"E1138"),sQuery(id+"F0.wireOp",EDGE,"E1139"),sQuery(id+"F0.wireOp",EDGE,"E1140"),sQuery(id+"F0.wireOp",EDGE,"E1141"),sQuery(id+"F0.wireOp",EDGE,"E1142"),sQuery(id+"F0.wireOp",EDGE,"E1143"),sQuery(id+"F0.wireOp",EDGE,"E1144"),sQuery(id+"F0.wireOp",EDGE,"E1145"),sQuery(id+"F0.wireOp",EDGE,"E1146"),sQuery(id+"F0.wireOp",EDGE,"E1147"),sQuery(id+"F0.wireOp",EDGE,"E1148"),sQuery(id+"F0.wireOp",EDGE,"E1149"),sQuery(id+"F0.wireOp",EDGE,"E1150"),sQuery(id+"F0.wireOp",EDGE,"E1151"),sQuery(id+"F0.wireOp",EDGE,"E1152"),sQuery(id+"F0.wireOp",EDGE,"E1153"),sQuery(id+"F0.wireOp",EDGE,"E1154"),sQuery(id+"F0.wireOp",EDGE,"E1155"),sQuery(id+"F0.wireOp",EDGE,"E1156"),sQuery(id+"F0.wireOp",EDGE,"E1157"),sQuery(id+"F0.wireOp",EDGE,"E1158"),sQuery(id+"F0.wireOp",EDGE,"E1159"),sQuery(id+"F0.wireOp",EDGE,"E1160"),sQuery(id+"F0.wireOp",EDGE,"E1161"),sQuery(id+"F0.wireOp",EDGE,"E1162"),sQuery(id+"F0.wireOp",EDGE,"E1163"),sQuery(id+"F0.wireOp",EDGE,"E1164"),sQuery(id+"F0.wireOp",EDGE,"E1165"),sQuery(id+"F0.wireOp",EDGE,"E1166"),sQuery(id+"F0.wireOp",EDGE,"E1167"),sQuery(id+"F0.wireOp",EDGE,"E1168"),sQuery(id+"F0.wireOp",EDGE,"E1169"),sQuery(id+"F0.wireOp",EDGE,"E1170"),sQuery(id+"F0.wireOp",EDGE,"E1171"),sQuery(id+"F0.wireOp",EDGE,"E1172"),sQuery(id+"F0.wireOp",EDGE,"E1173"),sQuery(id+"F0.wireOp",EDGE,"E1174"),sQuery(id+"F0.wireOp",EDGE,"E1175"),sQuery(id+"F0.wireOp",EDGE,"E1176"),sQuery(id+"F0.wireOp",EDGE,"E1177"),sQuery(id+"F0.wireOp",EDGE,"E1178"),sQuery(id+"F0.wireOp",EDGE,"E1179"),sQuery(id+"F0.wireOp",EDGE,"E1180"),sQuery(id+"F0.wireOp",EDGE,"E1181"),sQuery(id+"F0.wireOp",EDGE,"E1182"),sQuery(id+"F0.wireOp",EDGE,"E1183"),sQuery(id+"F0.wireOp",EDGE,"E1184"),sQuery(id+"F0.wireOp",EDGE,"E1185"),sQuery(id+"F0.wireOp",EDGE,"E1186"),sQuery(id+"F0.wireOp",EDGE,"E1187"),sQuery(id+"F0.wireOp",EDGE,"E1188"),sQuery(id+"F0.wireOp",EDGE,"E1189"),sQuery(id+"F0.wireOp",EDGE,"E1190"),sQuery(id+"F0.wireOp",EDGE,"E1191"),sQuery(id+"F0.wireOp",EDGE,"E1192"),sQuery(id+"F0.wireOp",EDGE,"E1193"),sQuery(id+"F0.wireOp",EDGE,"E1194"),sQuery(id+"F0.wireOp",EDGE,"E1195"),sQuery(id+"F0.wireOp",EDGE,"E1196"),sQuery(id+"F0.wireOp",EDGE,"E1197"),sQuery(id+"F0.wireOp",EDGE,"E1198"),sQuery(id+"F0.wireOp",EDGE,"E1199"),sQuery(id+"F0.wireOp",EDGE,"E1200"),sQuery(id+"F0.wireOp",EDGE,"E1201"),sQuery(id+"F0.wireOp",EDGE,"E1202"),sQuery(id+"F0.wireOp",EDGE,"E1203"),sQuery(id+"F0.wireOp",EDGE,"E1204"),sQuery(id+"F0.wireOp",EDGE,"E1205"),sQuery(id+"F0.wireOp",EDGE,"E1206"),sQuery(id+"F0.wireOp",EDGE,"E1207"),sQuery(id+"F0.wireOp",EDGE,"E1208"),sQuery(id+"F0.wireOp",EDGE,"E1209"),sQuery(id+"F0.wireOp",EDGE,"E1210"),sQuery(id+"F0.wireOp",EDGE,"E1211"),sQuery(id+"F0.wireOp",EDGE,"E1212"),sQuery(id+"F0.wireOp",EDGE,"E1213"),sQuery(id+"F0.wireOp",EDGE,"E1214"),sQuery(id+"F0.wireOp",EDGE,"E1215"),sQuery(id+"F0.wireOp",EDGE,"E1216"),sQuery(id+"F0.wireOp",EDGE,"E1217"),sQuery(id+"F0.wireOp",EDGE,"E1218"),sQuery(id+"F0.wireOp",EDGE,"E1219"),sQuery(id+"F0.wireOp",EDGE,"E1220"),sQuery(id+"F0.wireOp",EDGE,"E1221"),sQuery(id+"F0.wireOp",EDGE,"E1222"),sQuery(id+"F0.wireOp",EDGE,"E1223"),sQuery(id+"F0.wireOp",EDGE,"E1224"),sQuery(id+"F0.wireOp",EDGE,"E1225"),sQuery(id+"F0.wireOp",EDGE,"E1226"),sQuery(id+"F0.wireOp",EDGE,"E1227"),sQuery(id+"F0.wireOp",EDGE,"E1228"),sQuery(id+"F0.wireOp",EDGE,"E1229"),sQuery(id+"F0.wireOp",EDGE,"E1230"),sQuery(id+"F0.wireOp",EDGE,"E1231"),sQuery(id+"F0.wireOp",EDGE,"E1232"),sQuery(id+"F0.wireOp",EDGE,"E1233"),sQuery(id+"F0.wireOp",EDGE,"E1234"),sQuery(id+"F0.wireOp",EDGE,"E1235"),sQuery(id+"F0.wireOp",EDGE,"E1236"),sQuery(id+"F0.wireOp",EDGE,"E1237"),sQuery(id+"F0.wireOp",EDGE,"E1238"),sQuery(id+"F0.wireOp",EDGE,"E1239"),sQuery(id+"F0.wireOp",EDGE,"E1240"),sQuery(id+"F0.wireOp",EDGE,"E1241"),sQuery(id+"F0.wireOp",EDGE,"E1242"),sQuery(id+"F0.wireOp",EDGE,"E1243"),sQuery(id+"F0.wireOp",EDGE,"E1244"),sQuery(id+"F0.wireOp",EDGE,"E1245"),sQuery(id+"F0.wireOp",EDGE,"E1246"),sQuery(id+"F0.wireOp",EDGE,"E1247"),sQuery(id+"F0.wireOp",EDGE,"E1248"),sQuery(id+"F0.wireOp",EDGE,"E1249"),sQuery(id+"F0.wireOp",EDGE,"E1250"),sQuery(id+"F0.wireOp",EDGE,"E1251"),sQuery(id+"F0.wireOp",EDGE,"E1252"),sQuery(id+"F0.wireOp",EDGE,"E1253"),sQuery(id+"F0.wireOp",EDGE,"E1254"),sQuery(id+"F0.wireOp",EDGE,"E1255"),sQuery(id+"F0.wireOp",EDGE,"E1256"),sQuery(id+"F0.wireOp",EDGE,"E1257"),sQuery(id+"F0.wireOp",EDGE,"E1258"),sQuery(id+"F0.wireOp",EDGE,"E1259"),sQuery(id+"F0.wireOp",EDGE,"E1260"),sQuery(id+"F0.wireOp",EDGE,"E1261"),sQuery(id+"F0.wireOp",EDGE,"E1262"),sQuery(id+"F0.wireOp",EDGE,"E1263"),sQuery(id+"F0.wireOp",EDGE,"E1264"),sQuery(id+"F0.wireOp",EDGE,"E1265"),sQuery(id+"F0.wireOp",EDGE,"E1266"),sQuery(id+"F0.wireOp",EDGE,"E1267"),sQuery(id+"F0.wireOp",EDGE,"E1268"),sQuery(id+"F0.wireOp",EDGE,"E1269"),sQuery(id+"F0.wireOp",EDGE,"E1270"),sQuery(id+"F0.wireOp",EDGE,"E1271"),sQuery(id+"F0.wireOp",EDGE,"E1272"),sQuery(id+"F0.wireOp",EDGE,"E1273"),sQuery(id+"F0.wireOp",EDGE,"E1274"),sQuery(id+"F0.wireOp",EDGE,"E1275"),sQuery(id+"F0.wireOp",EDGE,"E1276"),sQuery(id+"F0.wireOp",EDGE,"E1277"),sQuery(id+"F0.wireOp",EDGE,"E1278"),sQuery(id+"F0.wireOp",EDGE,"E1279"),sQuery(id+"F0.wireOp",EDGE,"E1280"),sQuery(id+"F0.wireOp",EDGE,"E1281"),sQuery(id+"F0.wireOp",EDGE,"E1282"),sQuery(id+"F0.wireOp",EDGE,"E1283"),sQuery(id+"F0.wireOp",EDGE,"E1284"),sQuery(id+"F0.wireOp",EDGE,"E1285"),sQuery(id+"F0.wireOp",EDGE,"E1286"),sQuery(id+"F0.wireOp",EDGE,"E1287"),sQuery(id+"F0.wireOp",EDGE,"E1288"),sQuery(id+"F0.wireOp",EDGE,"E1289"),sQuery(id+"F0.wireOp",EDGE,"E1290"),sQuery(id+"F0.wireOp",EDGE,"E1291"),sQuery(id+"F0.wireOp",EDGE,"E1292"),sQuery(id+"F0.wireOp",EDGE,"E1293"),sQuery(id+"F0.wireOp",EDGE,"E1294"),sQuery(id+"F0.wireOp",EDGE,"E1295"),sQuery(id+"F0.wireOp",EDGE,"E1296"),sQuery(id+"F0.wireOp",EDGE,"E1297"),sQuery(id+"F0.wireOp",EDGE,"E1298"),sQuery(id+"F0.wireOp",EDGE,"E1299"),sQuery(id+"F0.wireOp",EDGE,"E1300"),sQuery(id+"F0.wireOp",EDGE,"E1301"),sQuery(id+"F0.wireOp",EDGE,"E1302"),sQuery(id+"F0.wireOp",EDGE,"E1303"),sQuery(id+"F0.wireOp",EDGE,"E1304"),sQuery(id+"F0.wireOp",EDGE,"E1305"),sQuery(id+"F0.wireOp",EDGE,"E1306"),sQuery(id+"F0.wireOp",EDGE,"E1307"),sQuery(id+"F0.wireOp",EDGE,"E1308"),sQuery(id+"F0.wireOp",EDGE,"E1309"),sQuery(id+"F0.wireOp",EDGE,"E1310"),sQuery(id+"F0.wireOp",EDGE,"E1311"),sQuery(id+"F0.wireOp",EDGE,"E1312"),sQuery(id+"F0.wireOp",EDGE,"E1313"),sQuery(id+"F0.wireOp",EDGE,"E1314"),sQuery(id+"F0.wireOp",EDGE,"E1315"),sQuery(id+"F0.wireOp",EDGE,"E1316"),sQuery(id+"F0.wireOp",EDGE,"E1317"),sQuery(id+"F0.wireOp",EDGE,"E1318"),sQuery(id+"F0.wireOp",EDGE,"E1319"),sQuery(id+"F0.wireOp",EDGE,"E1320"),sQuery(id+"F0.wireOp",EDGE,"E1321"),sQuery(id+"F0.wireOp",EDGE,"E1322"),sQuery(id+"F0.wireOp",EDGE,"E1323"),sQuery(id+"F0.wireOp",EDGE,"E1324"),sQuery(id+"F0.wireOp",EDGE,"E1325"),sQuery(id+"F0.wireOp",EDGE,"E1326"),sQuery(id+"F0.wireOp",EDGE,"E1327"),sQuery(id+"F0.wireOp",EDGE,"E1328"),sQuery(id+"F0.wireOp",EDGE,"E1329"),sQuery(id+"F0.wireOp",EDGE,"E1330"),sQuery(id+"F0.wireOp",EDGE,"E1331"),sQuery(id+"F0.wireOp",EDGE,"E1332"),sQuery(id+"F0.wireOp",EDGE,"E1333"),sQuery(id+"F0.wireOp",EDGE,"E1334"),sQuery(id+"F0.wireOp",EDGE,"E1335"),sQuery(id+"F0.wireOp",EDGE,"E1336"),sQuery(id+"F0.wireOp",EDGE,"E1337"),sQuery(id+"F0.wireOp",EDGE,"E1338"),sQuery(id+"F0.wireOp",EDGE,"E1339"),sQuery(id+"F0.wireOp",EDGE,"E1340"),sQuery(id+"F0.wireOp",EDGE,"E1341"),sQuery(id+"F0.wireOp",EDGE,"E1342"),sQuery(id+"F0.wireOp",EDGE,"E1343"),sQuery(id+"F0.wireOp",EDGE,"E1344"),sQuery(id+"F0.wireOp",EDGE,"E1345"),sQuery(id+"F0.wireOp",EDGE,"E1346"),sQuery(id+"F0.wireOp",EDGE,"E1347"),sQuery(id+"F0.wireOp",EDGE,"E1348"),sQuery(id+"F0.wireOp",EDGE,"E1349"),sQuery(id+"F0.wireOp",EDGE,"E1350"),sQuery(id+"F0.wireOp",EDGE,"E1351"),sQuery(id+"F0.wireOp",EDGE,"E1352"),sQuery(id+"F0.wireOp",EDGE,"E1353"),sQuery(id+"F0.wireOp",EDGE,"E1354"),sQuery(id+"F0.wireOp",EDGE,"E1355"),sQuery(id+"F0.wireOp",EDGE,"E1356"),sQuery(id+"F0.wireOp",EDGE,"E1357"),sQuery(id+"F0.wireOp",EDGE,"E1358"),sQuery(id+"F0.wireOp",EDGE,"E1359"),sQuery(id+"F0.wireOp",EDGE,"E1360"),sQuery(id+"F0.wireOp",EDGE,"E1361"),sQuery(id+"F0.wireOp",EDGE,"E1362"),sQuery(id+"F0.wireOp",EDGE,"E1363"),sQuery(id+"F0.wireOp",EDGE,"E1364"),sQuery(id+"F0.wireOp",EDGE,"E1365"),sQuery(id+"F0.wireOp",EDGE,"E1366"),sQuery(id+"F0.wireOp",EDGE,"E1367"),sQuery(id+"F0.wireOp",EDGE,"E1368"),sQuery(id+"F0.wireOp",EDGE,"E1369"),sQuery(id+"F0.wireOp",EDGE,"E1370"),sQuery(id+"F0.wireOp",EDGE,"E1371"),sQuery(id+"F0.wireOp",EDGE,"E1372"),sQuery(id+"F0.wireOp",EDGE,"E1373"),sQuery(id+"F0.wireOp",EDGE,"E1374"),sQuery(id+"F0.wireOp",EDGE,"E1375"),sQuery(id+"F0.wireOp",EDGE,"E1376"),sQuery(id+"F0.wireOp",EDGE,"E1377"),sQuery(id+"F0.wireOp",EDGE,"E1378"),sQuery(id+"F0.wireOp",EDGE,"E1379"),sQuery(id+"F0.wireOp",EDGE,"E1380"),sQuery(id+"F0.wireOp",EDGE,"E1381"),sQuery(id+"F0.wireOp",EDGE,"E1382"),sQuery(id+"F0.wireOp",EDGE,"E1383"),sQuery(id+"F0.wireOp",EDGE,"E1384"),sQuery(id+"F0.wireOp",EDGE,"E1385"),sQuery(id+"F0.wireOp",EDGE,"E1386"),sQuery(id+"F0.wireOp",EDGE,"E1387"),sQuery(id+"F0.wireOp",EDGE,"E1388"),sQuery(id+"F0.wireOp",EDGE,"E1389"),sQuery(id+"F0.wireOp",EDGE,"E1390"),sQuery(id+"F0.wireOp",EDGE,"E1391"),sQuery(id+"F0.wireOp",EDGE,"E1392"),sQuery(id+"F0.wireOp",EDGE,"E1393"),sQuery(id+"F0.wireOp",EDGE,"E1394"),sQuery(id+"F0.wireOp",EDGE,"E1395"),sQuery(id+"F0.wireOp",EDGE,"E1396"),sQuery(id+"F0.wireOp",EDGE,"E1397"),sQuery(id+"F0.wireOp",EDGE,"E1398"),sQuery(id+"F0.wireOp",EDGE,"E1399"),sQuery(id+"F0.wireOp",EDGE,"E1400"),sQuery(id+"F0.wireOp",EDGE,"E1401"),sQuery(id+"F0.wireOp",EDGE,"E1402"),sQuery(id+"F0.wireOp",EDGE,"E1403"),sQuery(id+"F0.wireOp",EDGE,"E1404"),sQuery(id+"F0.wireOp",EDGE,"E1405"),sQuery(id+"F0.wireOp",EDGE,"E1406"),sQuery(id+"F0.wireOp",EDGE,"E1407"),sQuery(id+"F0.wireOp",EDGE,"E1408"),sQuery(id+"F0.wireOp",EDGE,"E1409"),sQuery(id+"F0.wireOp",EDGE,"E1410"),sQuery(id+"F0.wireOp",EDGE,"E1411"),sQuery(id+"F0.wireOp",EDGE,"E1412"),sQuery(id+"F0.wireOp",EDGE,"E1413"),sQuery(id+"F0.wireOp",EDGE,"E1414"),sQuery(id+"F0.wireOp",EDGE,"E1415"),sQuery(id+"F0.wireOp",EDGE,"E1416"),sQuery(id+"F0.wireOp",EDGE,"E1417"),sQuery(id+"F0.wireOp",EDGE,"E1418"),sQuery(id+"F0.wireOp",EDGE,"E1419"),sQuery(id+"F0.wireOp",EDGE,"E1420"),sQuery(id+"F0.wireOp",EDGE,"E1421"),sQuery(id+"F0.wireOp",EDGE,"E1422"),sQuery(id+"F0.wireOp",EDGE,"E1423"),sQuery(id+"F0.wireOp",EDGE,"E1424"),sQuery(id+"F0.wireOp",EDGE,"E1425"),sQuery(id+"F0.wireOp",EDGE,"E1426"),sQuery(id+"F0.wireOp",EDGE,"E1427"),sQuery(id+"F0.wireOp",EDGE,"E1428"),sQuery(id+"F0.wireOp",EDGE,"E1429"),sQuery(id+"F0.wireOp",EDGE,"E1430"),sQuery(id+"F0.wireOp",EDGE,"E1431"),sQuery(id+"F0.wireOp",EDGE,"E1432"),sQuery(id+"F0.wireOp",EDGE,"E1433"),sQuery(id+"F0.wireOp",EDGE,"E1434"),sQuery(id+"F0.wireOp",EDGE,"E1435"),sQuery(id+"F0.wireOp",EDGE,"E1436"),sQuery(id+"F0.wireOp",EDGE,"E1437"),sQuery(id+"F0.wireOp",EDGE,"E1438"),sQuery(id+"F0.wireOp",EDGE,"E1439"),sQuery(id+"F0.wireOp",EDGE,"E1440"),sQuery(id+"F0.wireOp",EDGE,"E1441"),sQuery(id+"F0.wireOp",EDGE,"E1442"),sQuery(id+"F0.wireOp",EDGE,"E1443")])]});
            hole(context, id + "F4", {"style" : HoleStyle.SIMPLE, "endStyle" : HoleEndStyle.THROUGH, "standardTappedOrClearance" : lookupTablePath({ "standard" : "ISO", "size" : "3.3", "type" : "Drilled" }), "standardBlindInLast" : lookupTablePath({ "standard" : "ISO", "size" : "3.3", "type" : "Drilled" }), "holeDiameter" : 3.3 * mm, "isTappedThrough" : true, "tappedDepth" : 4.2 * mm, "tapClearance" : 3, "locations" : qUnion([Q0, Q1, Q2, Q3, Q4, Q5, Q6, Q7, Q8, Q9]), "scope" : qUnion([Q10]), "startStyle" : HoleStartStyle.PART});
        }
        {
            var Q0;
            Q0=makeQuery(id+"F3.boolean.opBoolean","COPY",EDGE,{"derivedFrom":makeQuery(id+"F3.opExtrude","SWEPT_EDGE",EDGE,{"disambiguationData":[OSD([sQuery(id+"F2.wireOp",EDGE,"E1452.bottom"),sQuery(id+"F2.wireOp",EDGE,"E1452.left")])]})});
            var Q1;
            Q1=makeQuery(id+"F3.boolean.opBoolean","COPY",EDGE,{"derivedFrom":makeQuery(id+"F3.opExtrude","SWEPT_EDGE",EDGE,{"disambiguationData":[OSD([sQuery(id+"F2.wireOp",EDGE,"E1452.top"),sQuery(id+"F2.wireOp",EDGE,"E1452.left")])]})});
            var Q2;
            Q2=makeQuery(id+"F3.boolean.opBoolean","COPY",EDGE,{"derivedFrom":makeQuery(id+"F3.opExtrude","SWEPT_EDGE",EDGE,{"disambiguationData":[OSD([sQuery(id+"F2.wireOp",EDGE,"E1452.top"),sQuery(id+"F2.wireOp",EDGE,"E1452.right")])]})});
            var Q3;
            Q3=makeQuery(id+"F3.boolean.opBoolean","COPY",EDGE,{"derivedFrom":makeQuery(id+"F3.opExtrude","SWEPT_EDGE",EDGE,{"disambiguationData":[OSD([sQuery(id+"F2.wireOp",EDGE,"E1452.bottom"),sQuery(id+"F2.wireOp",EDGE,"E1452.right")])]})});
            fillet(context, id + "F5", {"entities" : qUnion([Q0, Q1, Q2, Q3]), "radius" : 3 * mm, "tangentPropagation" : true, "allowEdgeOverflow" : false});
        }
    });
